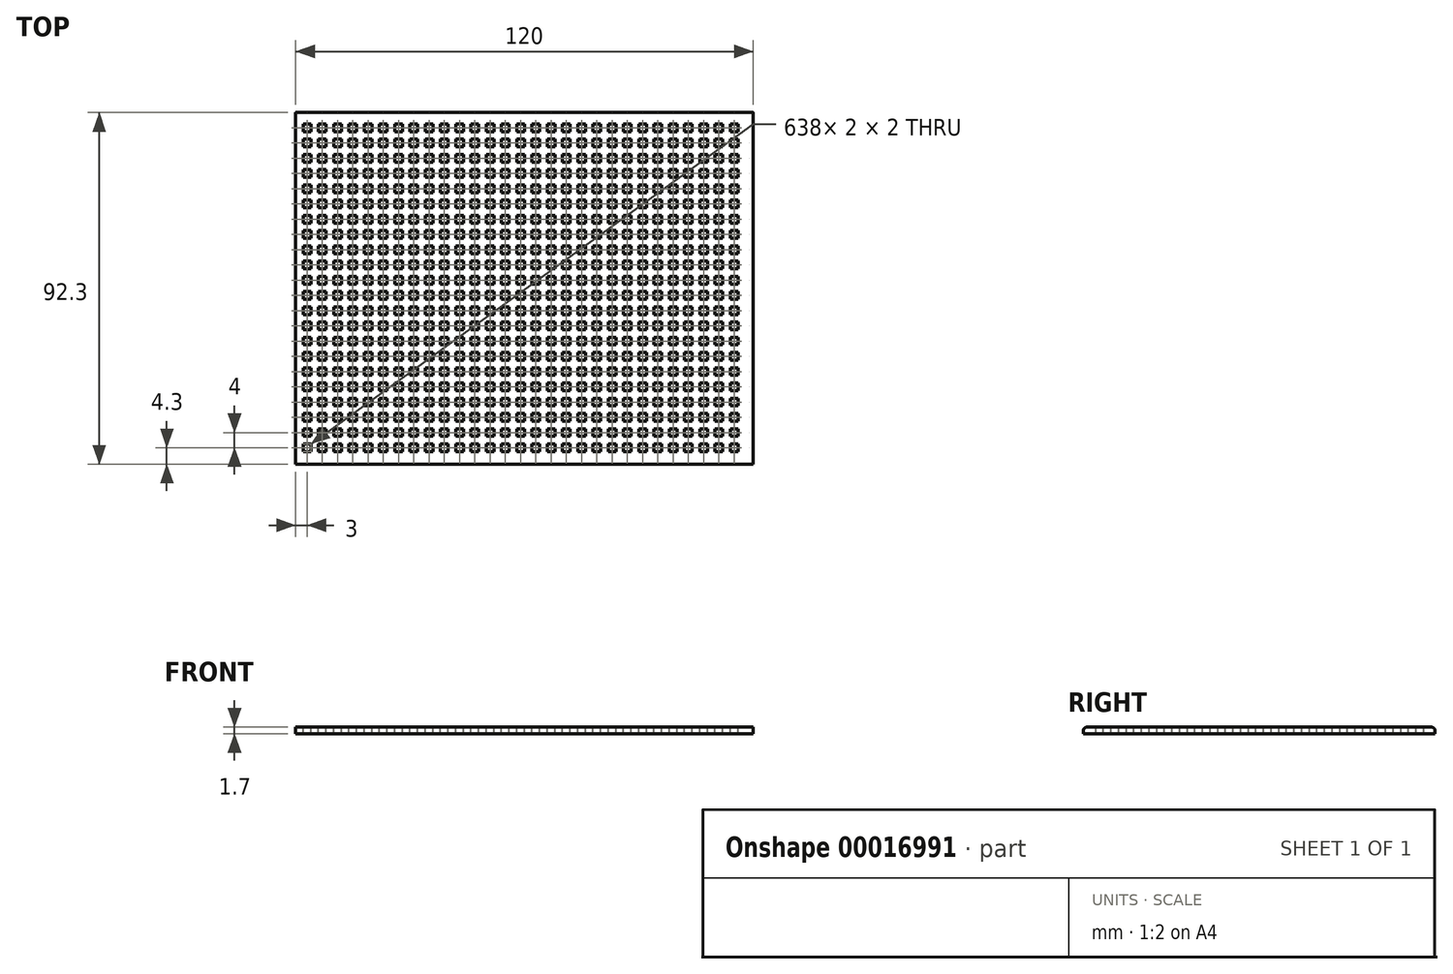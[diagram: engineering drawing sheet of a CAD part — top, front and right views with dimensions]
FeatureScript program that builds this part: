
annotation { "Feature Type Name" : "Feature", "Feature Type Description" : "" }
export const myFeature = defineFeature(function(context is Context, id is Id, definition is map)
    precondition{}
    {
        {
            var Q0;
            Q0=qCreatedBy(makeId("Right.planeOp"),FACE);
            var sketch = newSketch(context, id + "F0", { "sketchPlane" : qUnion([Q0])});
            skLineSegment(sketch, "E0", {"start": v(0, 0) * mm, "end": v(46.15, 0) * mm});
            skLineSegment(sketch, "E1", {"start": v(0, 0) * mm, "end": v(0, 1.7) * mm});
            skLineSegment(sketch, "E2", {"start": v(46.15, 0) * mm, "end": v(46.15, 1.7) * mm});
            skLineSegment(sketch, "E3", {"start": v(0, 1.7) * mm, "end": v(46.15, 1.7) * mm});
            skLineSegment(sketch, "E4.MirrorCS", {"start": v(-46.15, 0) * mm, "end": v(-46.15, 1.7) * mm});
            skLineSegment(sketch, "E5.MirrorCS", {"start": v(0, 1.7) * mm, "end": v(-46.15, 1.7) * mm});
            skLineSegment(sketch, "E6.MirrorCS", {"start": v(0, 0) * mm, "end": v(-46.15, 0) * mm});
            skSolve(sketch);
        }
        {
            var Q0;
            Q0=makeQuery(id+"F0.imprint","IMPRINT",FACE,{"disambiguationData":[TD([[makeQuery(id+"F0.imprint","IMPRINT",EDGE,{"derivedFrom":sQuery(id+"F0.wireOp",EDGE,"E0")}),1.0]])]});
            var Q1;
            Q1=makeQuery(id+"F0.imprint","IMPRINT",FACE,{"disambiguationData":[TD([[makeQuery(id+"F0.imprint","IMPRINT",EDGE,{"derivedFrom":sQuery(id+"F0.wireOp",EDGE,"E1")}),1.0]])]});
            extrude(context, id + "F1", {"entities" : qUnion([Q0, Q1]), "depth" : 60 * mm, "hasSecondDirection" : true, "secondDirectionOppositeDirection" : true, "secondDirectionDepth" : 60 * mm});
        }
        {
            var Q0;
            Q0=makeQuery(id+"F1.opExtrude","SWEPT_EDGE",EDGE,{"disambiguationData":[OSD([sQuery(id+"F0.wireOp",EDGE,"E2"),sQuery(id+"F0.wireOp",EDGE,"E3")])]});
            var Q1;
            Q1=makeQuery(id+"F1.opExtrude","SWEPT_EDGE",EDGE,{"disambiguationData":[OSD([sQuery(id+"F0.wireOp",EDGE,"E4.MirrorCS"),sQuery(id+"F0.wireOp",EDGE,"E5.MirrorCS")])]});
            fillet(context, id + "F2", {"entities" : qUnion([Q0, Q1]), "radius" : 1 * mm, "tangentPropagation" : true, "allowEdgeOverflow" : false});
        }
        {
            var Q0;
            Q0=makeQuery(id+"F1.opExtrude","SWEPT_FACE",FACE,{"disambiguationData":[OSD([sQuery(id+"F0.wireOp",EDGE,"E3"),sQuery(id+"F0.wireOp",EDGE,"E5.MirrorCS")])]});
            var sketch = newSketch(context, id + "F3", { "sketchPlane" : qUnion([Q0])});
            skLineSegment(sketch, "E7.bottom", {"start": v(-58, 43.15) * mm, "end": v(-56, 43.15) * mm});
            skLineSegment(sketch, "E7.top", {"start": v(-58, 41.15) * mm, "end": v(-56, 41.15) * mm});
            skLineSegment(sketch, "E7.left", {"start": v(-58, 43.15) * mm, "end": v(-58, 41.15) * mm});
            skLineSegment(sketch, "E7.right", {"start": v(-56, 43.15) * mm, "end": v(-56, 41.15) * mm});
            skLineSegment(sketch, "E8.0.1.0", {"start": v(-56, 39.15) * mm, "end": v(-56, 37.15) * mm});
            skLineSegment(sketch, "E8.0.1.1", {"start": v(-58, 39.15) * mm, "end": v(-58, 37.15) * mm});
            skLineSegment(sketch, "E8.0.1.2", {"start": v(-58, 37.15) * mm, "end": v(-56, 37.15) * mm});
            skLineSegment(sketch, "E8.0.1.3", {"start": v(-58, 39.15) * mm, "end": v(-56, 39.15) * mm});
            skLineSegment(sketch, "E8.0.2.0", {"start": v(-56, 35.15) * mm, "end": v(-56, 33.15) * mm});
            skLineSegment(sketch, "E8.0.2.1", {"start": v(-58, 35.15) * mm, "end": v(-58, 33.15) * mm});
            skLineSegment(sketch, "E8.0.2.2", {"start": v(-58, 33.15) * mm, "end": v(-56, 33.15) * mm});
            skLineSegment(sketch, "E8.0.2.3", {"start": v(-58, 35.15) * mm, "end": v(-56, 35.15) * mm});
            skLineSegment(sketch, "E8.0.3.0", {"start": v(-56, 31.15) * mm, "end": v(-56, 29.15) * mm});
            skLineSegment(sketch, "E8.0.3.1", {"start": v(-58, 31.15) * mm, "end": v(-58, 29.15) * mm});
            skLineSegment(sketch, "E8.0.3.2", {"start": v(-58, 29.15) * mm, "end": v(-56, 29.15) * mm});
            skLineSegment(sketch, "E8.0.3.3", {"start": v(-58, 31.15) * mm, "end": v(-56, 31.15) * mm});
            skLineSegment(sketch, "E8.0.4.0", {"start": v(-56, 27.15) * mm, "end": v(-56, 25.15) * mm});
            skLineSegment(sketch, "E8.0.4.1", {"start": v(-58, 27.15) * mm, "end": v(-58, 25.15) * mm});
            skLineSegment(sketch, "E8.0.4.2", {"start": v(-58, 25.15) * mm, "end": v(-56, 25.15) * mm});
            skLineSegment(sketch, "E8.0.4.3", {"start": v(-58, 27.15) * mm, "end": v(-56, 27.15) * mm});
            skLineSegment(sketch, "E8.0.5.0", {"start": v(-56, 23.15) * mm, "end": v(-56, 21.15) * mm});
            skLineSegment(sketch, "E8.0.5.1", {"start": v(-58, 23.15) * mm, "end": v(-58, 21.15) * mm});
            skLineSegment(sketch, "E8.0.5.2", {"start": v(-58, 21.15) * mm, "end": v(-56, 21.15) * mm});
            skLineSegment(sketch, "E8.0.5.3", {"start": v(-58, 23.15) * mm, "end": v(-56, 23.15) * mm});
            skLineSegment(sketch, "E8.0.6.0", {"start": v(-56, 19.15) * mm, "end": v(-56, 17.15) * mm});
            skLineSegment(sketch, "E8.0.6.1", {"start": v(-58, 19.15) * mm, "end": v(-58, 17.15) * mm});
            skLineSegment(sketch, "E8.0.6.2", {"start": v(-58, 17.15) * mm, "end": v(-56, 17.15) * mm});
            skLineSegment(sketch, "E8.0.6.3", {"start": v(-58, 19.15) * mm, "end": v(-56, 19.15) * mm});
            skLineSegment(sketch, "E8.0.7.0", {"start": v(-56, 15.15) * mm, "end": v(-56, 13.15) * mm});
            skLineSegment(sketch, "E8.0.7.1", {"start": v(-58, 15.15) * mm, "end": v(-58, 13.15) * mm});
            skLineSegment(sketch, "E8.0.7.2", {"start": v(-58, 13.15) * mm, "end": v(-56, 13.15) * mm});
            skLineSegment(sketch, "E8.0.7.3", {"start": v(-58, 15.15) * mm, "end": v(-56, 15.15) * mm});
            skLineSegment(sketch, "E8.0.8.0", {"start": v(-56, 11.15) * mm, "end": v(-56, 9.15) * mm});
            skLineSegment(sketch, "E8.0.8.1", {"start": v(-58, 11.15) * mm, "end": v(-58, 9.15) * mm});
            skLineSegment(sketch, "E8.0.8.2", {"start": v(-58, 9.15) * mm, "end": v(-56, 9.15) * mm});
            skLineSegment(sketch, "E8.0.8.3", {"start": v(-58, 11.15) * mm, "end": v(-56, 11.15) * mm});
            skLineSegment(sketch, "E8.0.9.0", {"start": v(-56, 7.15) * mm, "end": v(-56, 5.15) * mm});
            skLineSegment(sketch, "E8.0.9.1", {"start": v(-58, 7.15) * mm, "end": v(-58, 5.15) * mm});
            skLineSegment(sketch, "E8.0.9.2", {"start": v(-58, 5.15) * mm, "end": v(-56, 5.15) * mm});
            skLineSegment(sketch, "E8.0.9.3", {"start": v(-58, 7.15) * mm, "end": v(-56, 7.15) * mm});
            skLineSegment(sketch, "E8.0.10.0", {"start": v(-56, 3.15) * mm, "end": v(-56, 1.15) * mm});
            skLineSegment(sketch, "E8.0.10.1", {"start": v(-58, 3.15) * mm, "end": v(-58, 1.15) * mm});
            skLineSegment(sketch, "E8.0.10.2", {"start": v(-58, 1.15) * mm, "end": v(-56, 1.15) * mm});
            skLineSegment(sketch, "E8.0.10.3", {"start": v(-58, 3.15) * mm, "end": v(-56, 3.15) * mm});
            skLineSegment(sketch, "E8.0.11.0", {"start": v(-56, -0.85) * mm, "end": v(-56, -2.85) * mm});
            skLineSegment(sketch, "E8.0.11.1", {"start": v(-58, -0.85) * mm, "end": v(-58, -2.85) * mm});
            skLineSegment(sketch, "E8.0.11.2", {"start": v(-58, -2.85) * mm, "end": v(-56, -2.85) * mm});
            skLineSegment(sketch, "E8.0.11.3", {"start": v(-58, -0.85) * mm, "end": v(-56, -0.85) * mm});
            skLineSegment(sketch, "E8.0.12.0", {"start": v(-56, -4.85) * mm, "end": v(-56, -6.85) * mm});
            skLineSegment(sketch, "E8.0.12.1", {"start": v(-58, -4.85) * mm, "end": v(-58, -6.85) * mm});
            skLineSegment(sketch, "E8.0.12.2", {"start": v(-58, -6.85) * mm, "end": v(-56, -6.85) * mm});
            skLineSegment(sketch, "E8.0.12.3", {"start": v(-58, -4.85) * mm, "end": v(-56, -4.85) * mm});
            skLineSegment(sketch, "E8.0.13.0", {"start": v(-56, -8.85) * mm, "end": v(-56, -10.85) * mm});
            skLineSegment(sketch, "E8.0.13.1", {"start": v(-58, -8.85) * mm, "end": v(-58, -10.85) * mm});
            skLineSegment(sketch, "E8.0.13.2", {"start": v(-58, -10.85) * mm, "end": v(-56, -10.85) * mm});
            skLineSegment(sketch, "E8.0.13.3", {"start": v(-58, -8.85) * mm, "end": v(-56, -8.85) * mm});
            skLineSegment(sketch, "E8.0.14.0", {"start": v(-56, -12.85) * mm, "end": v(-56, -14.85) * mm});
            skLineSegment(sketch, "E8.0.14.1", {"start": v(-58, -12.85) * mm, "end": v(-58, -14.85) * mm});
            skLineSegment(sketch, "E8.0.14.2", {"start": v(-58, -14.85) * mm, "end": v(-56, -14.85) * mm});
            skLineSegment(sketch, "E8.0.14.3", {"start": v(-58, -12.85) * mm, "end": v(-56, -12.85) * mm});
            skLineSegment(sketch, "E8.0.15.0", {"start": v(-56, -16.85) * mm, "end": v(-56, -18.85) * mm});
            skLineSegment(sketch, "E8.0.15.1", {"start": v(-58, -16.85) * mm, "end": v(-58, -18.85) * mm});
            skLineSegment(sketch, "E8.0.15.2", {"start": v(-58, -18.85) * mm, "end": v(-56, -18.85) * mm});
            skLineSegment(sketch, "E8.0.15.3", {"start": v(-58, -16.85) * mm, "end": v(-56, -16.85) * mm});
            skLineSegment(sketch, "E8.0.16.0", {"start": v(-56, -20.85) * mm, "end": v(-56, -22.85) * mm});
            skLineSegment(sketch, "E8.0.16.1", {"start": v(-58, -20.85) * mm, "end": v(-58, -22.85) * mm});
            skLineSegment(sketch, "E8.0.16.2", {"start": v(-58, -22.85) * mm, "end": v(-56, -22.85) * mm});
            skLineSegment(sketch, "E8.0.16.3", {"start": v(-58, -20.85) * mm, "end": v(-56, -20.85) * mm});
            skLineSegment(sketch, "E8.0.17.0", {"start": v(-56, -24.85) * mm, "end": v(-56, -26.85) * mm});
            skLineSegment(sketch, "E8.0.17.1", {"start": v(-58, -24.85) * mm, "end": v(-58, -26.85) * mm});
            skLineSegment(sketch, "E8.0.17.2", {"start": v(-58, -26.85) * mm, "end": v(-56, -26.85) * mm});
            skLineSegment(sketch, "E8.0.17.3", {"start": v(-58, -24.85) * mm, "end": v(-56, -24.85) * mm});
            skLineSegment(sketch, "E8.0.18.0", {"start": v(-56, -28.85) * mm, "end": v(-56, -30.85) * mm});
            skLineSegment(sketch, "E8.0.18.1", {"start": v(-58, -28.85) * mm, "end": v(-58, -30.85) * mm});
            skLineSegment(sketch, "E8.0.18.2", {"start": v(-58, -30.85) * mm, "end": v(-56, -30.85) * mm});
            skLineSegment(sketch, "E8.0.18.3", {"start": v(-58, -28.85) * mm, "end": v(-56, -28.85) * mm});
            skLineSegment(sketch, "E8.0.19.0", {"start": v(-56, -32.85) * mm, "end": v(-56, -34.85) * mm});
            skLineSegment(sketch, "E8.0.19.1", {"start": v(-58, -32.85) * mm, "end": v(-58, -34.85) * mm});
            skLineSegment(sketch, "E8.0.19.2", {"start": v(-58, -34.85) * mm, "end": v(-56, -34.85) * mm});
            skLineSegment(sketch, "E8.0.19.3", {"start": v(-58, -32.85) * mm, "end": v(-56, -32.85) * mm});
            skLineSegment(sketch, "E8.0.20.0", {"start": v(-56, -36.85) * mm, "end": v(-56, -38.85) * mm});
            skLineSegment(sketch, "E8.0.20.1", {"start": v(-58, -36.85) * mm, "end": v(-58, -38.85) * mm});
            skLineSegment(sketch, "E8.0.20.2", {"start": v(-58, -38.85) * mm, "end": v(-56, -38.85) * mm});
            skLineSegment(sketch, "E8.0.20.3", {"start": v(-58, -36.85) * mm, "end": v(-56, -36.85) * mm});
            skLineSegment(sketch, "E8.0.21.0", {"start": v(-56, -40.85) * mm, "end": v(-56, -42.85) * mm});
            skLineSegment(sketch, "E8.0.21.1", {"start": v(-58, -40.85) * mm, "end": v(-58, -42.85) * mm});
            skLineSegment(sketch, "E8.0.21.2", {"start": v(-58, -42.85) * mm, "end": v(-56, -42.85) * mm});
            skLineSegment(sketch, "E8.0.21.3", {"start": v(-58, -40.85) * mm, "end": v(-56, -40.85) * mm});
            skLineSegment(sketch, "E8.1.0.0", {"start": v(-52, 43.15) * mm, "end": v(-52, 41.15) * mm});
            skLineSegment(sketch, "E8.1.0.1", {"start": v(-54, 43.15) * mm, "end": v(-54, 41.15) * mm});
            skLineSegment(sketch, "E8.1.0.2", {"start": v(-54, 41.15) * mm, "end": v(-52, 41.15) * mm});
            skLineSegment(sketch, "E8.1.0.3", {"start": v(-54, 43.15) * mm, "end": v(-52, 43.15) * mm});
            skLineSegment(sketch, "E8.1.1.0", {"start": v(-52, 39.15) * mm, "end": v(-52, 37.15) * mm});
            skLineSegment(sketch, "E8.1.1.1", {"start": v(-54, 39.15) * mm, "end": v(-54, 37.15) * mm});
            skLineSegment(sketch, "E8.1.1.2", {"start": v(-54, 37.15) * mm, "end": v(-52, 37.15) * mm});
            skLineSegment(sketch, "E8.1.1.3", {"start": v(-54, 39.15) * mm, "end": v(-52, 39.15) * mm});
            skLineSegment(sketch, "E8.1.2.0", {"start": v(-52, 35.15) * mm, "end": v(-52, 33.15) * mm});
            skLineSegment(sketch, "E8.1.2.1", {"start": v(-54, 35.15) * mm, "end": v(-54, 33.15) * mm});
            skLineSegment(sketch, "E8.1.2.2", {"start": v(-54, 33.15) * mm, "end": v(-52, 33.15) * mm});
            skLineSegment(sketch, "E8.1.2.3", {"start": v(-54, 35.15) * mm, "end": v(-52, 35.15) * mm});
            skLineSegment(sketch, "E8.1.3.0", {"start": v(-52, 31.15) * mm, "end": v(-52, 29.15) * mm});
            skLineSegment(sketch, "E8.1.3.1", {"start": v(-54, 31.15) * mm, "end": v(-54, 29.15) * mm});
            skLineSegment(sketch, "E8.1.3.2", {"start": v(-54, 29.15) * mm, "end": v(-52, 29.15) * mm});
            skLineSegment(sketch, "E8.1.3.3", {"start": v(-54, 31.15) * mm, "end": v(-52, 31.15) * mm});
            skLineSegment(sketch, "E8.1.4.0", {"start": v(-52, 27.15) * mm, "end": v(-52, 25.15) * mm});
            skLineSegment(sketch, "E8.1.4.1", {"start": v(-54, 27.15) * mm, "end": v(-54, 25.15) * mm});
            skLineSegment(sketch, "E8.1.4.2", {"start": v(-54, 25.15) * mm, "end": v(-52, 25.15) * mm});
            skLineSegment(sketch, "E8.1.4.3", {"start": v(-54, 27.15) * mm, "end": v(-52, 27.15) * mm});
            skLineSegment(sketch, "E8.1.5.0", {"start": v(-52, 23.15) * mm, "end": v(-52, 21.15) * mm});
            skLineSegment(sketch, "E8.1.5.1", {"start": v(-54, 23.15) * mm, "end": v(-54, 21.15) * mm});
            skLineSegment(sketch, "E8.1.5.2", {"start": v(-54, 21.15) * mm, "end": v(-52, 21.15) * mm});
            skLineSegment(sketch, "E8.1.5.3", {"start": v(-54, 23.15) * mm, "end": v(-52, 23.15) * mm});
            skLineSegment(sketch, "E8.1.6.0", {"start": v(-52, 19.15) * mm, "end": v(-52, 17.15) * mm});
            skLineSegment(sketch, "E8.1.6.1", {"start": v(-54, 19.15) * mm, "end": v(-54, 17.15) * mm});
            skLineSegment(sketch, "E8.1.6.2", {"start": v(-54, 17.15) * mm, "end": v(-52, 17.15) * mm});
            skLineSegment(sketch, "E8.1.6.3", {"start": v(-54, 19.15) * mm, "end": v(-52, 19.15) * mm});
            skLineSegment(sketch, "E8.1.7.0", {"start": v(-52, 15.15) * mm, "end": v(-52, 13.15) * mm});
            skLineSegment(sketch, "E8.1.7.1", {"start": v(-54, 15.15) * mm, "end": v(-54, 13.15) * mm});
            skLineSegment(sketch, "E8.1.7.2", {"start": v(-54, 13.15) * mm, "end": v(-52, 13.15) * mm});
            skLineSegment(sketch, "E8.1.7.3", {"start": v(-54, 15.15) * mm, "end": v(-52, 15.15) * mm});
            skLineSegment(sketch, "E8.1.8.0", {"start": v(-52, 11.15) * mm, "end": v(-52, 9.15) * mm});
            skLineSegment(sketch, "E8.1.8.1", {"start": v(-54, 11.15) * mm, "end": v(-54, 9.15) * mm});
            skLineSegment(sketch, "E8.1.8.2", {"start": v(-54, 9.15) * mm, "end": v(-52, 9.15) * mm});
            skLineSegment(sketch, "E8.1.8.3", {"start": v(-54, 11.15) * mm, "end": v(-52, 11.15) * mm});
            skLineSegment(sketch, "E8.1.9.0", {"start": v(-52, 7.15) * mm, "end": v(-52, 5.15) * mm});
            skLineSegment(sketch, "E8.1.9.1", {"start": v(-54, 7.15) * mm, "end": v(-54, 5.15) * mm});
            skLineSegment(sketch, "E8.1.9.2", {"start": v(-54, 5.15) * mm, "end": v(-52, 5.15) * mm});
            skLineSegment(sketch, "E8.1.9.3", {"start": v(-54, 7.15) * mm, "end": v(-52, 7.15) * mm});
            skLineSegment(sketch, "E8.1.10.0", {"start": v(-52, 3.15) * mm, "end": v(-52, 1.15) * mm});
            skLineSegment(sketch, "E8.1.10.1", {"start": v(-54, 3.15) * mm, "end": v(-54, 1.15) * mm});
            skLineSegment(sketch, "E8.1.10.2", {"start": v(-54, 1.15) * mm, "end": v(-52, 1.15) * mm});
            skLineSegment(sketch, "E8.1.10.3", {"start": v(-54, 3.15) * mm, "end": v(-52, 3.15) * mm});
            skLineSegment(sketch, "E8.1.11.0", {"start": v(-52, -0.85) * mm, "end": v(-52, -2.85) * mm});
            skLineSegment(sketch, "E8.1.11.1", {"start": v(-54, -0.85) * mm, "end": v(-54, -2.85) * mm});
            skLineSegment(sketch, "E8.1.11.2", {"start": v(-54, -2.85) * mm, "end": v(-52, -2.85) * mm});
            skLineSegment(sketch, "E8.1.11.3", {"start": v(-54, -0.85) * mm, "end": v(-52, -0.85) * mm});
            skLineSegment(sketch, "E8.1.12.0", {"start": v(-52, -4.85) * mm, "end": v(-52, -6.85) * mm});
            skLineSegment(sketch, "E8.1.12.1", {"start": v(-54, -4.85) * mm, "end": v(-54, -6.85) * mm});
            skLineSegment(sketch, "E8.1.12.2", {"start": v(-54, -6.85) * mm, "end": v(-52, -6.85) * mm});
            skLineSegment(sketch, "E8.1.12.3", {"start": v(-54, -4.85) * mm, "end": v(-52, -4.85) * mm});
            skLineSegment(sketch, "E8.1.13.0", {"start": v(-52, -8.85) * mm, "end": v(-52, -10.85) * mm});
            skLineSegment(sketch, "E8.1.13.1", {"start": v(-54, -8.85) * mm, "end": v(-54, -10.85) * mm});
            skLineSegment(sketch, "E8.1.13.2", {"start": v(-54, -10.85) * mm, "end": v(-52, -10.85) * mm});
            skLineSegment(sketch, "E8.1.13.3", {"start": v(-54, -8.85) * mm, "end": v(-52, -8.85) * mm});
            skLineSegment(sketch, "E8.1.14.0", {"start": v(-52, -12.85) * mm, "end": v(-52, -14.85) * mm});
            skLineSegment(sketch, "E8.1.14.1", {"start": v(-54, -12.85) * mm, "end": v(-54, -14.85) * mm});
            skLineSegment(sketch, "E8.1.14.2", {"start": v(-54, -14.85) * mm, "end": v(-52, -14.85) * mm});
            skLineSegment(sketch, "E8.1.14.3", {"start": v(-54, -12.85) * mm, "end": v(-52, -12.85) * mm});
            skLineSegment(sketch, "E8.1.15.0", {"start": v(-52, -16.85) * mm, "end": v(-52, -18.85) * mm});
            skLineSegment(sketch, "E8.1.15.1", {"start": v(-54, -16.85) * mm, "end": v(-54, -18.85) * mm});
            skLineSegment(sketch, "E8.1.15.2", {"start": v(-54, -18.85) * mm, "end": v(-52, -18.85) * mm});
            skLineSegment(sketch, "E8.1.15.3", {"start": v(-54, -16.85) * mm, "end": v(-52, -16.85) * mm});
            skLineSegment(sketch, "E8.1.16.0", {"start": v(-52, -20.85) * mm, "end": v(-52, -22.85) * mm});
            skLineSegment(sketch, "E8.1.16.1", {"start": v(-54, -20.85) * mm, "end": v(-54, -22.85) * mm});
            skLineSegment(sketch, "E8.1.16.2", {"start": v(-54, -22.85) * mm, "end": v(-52, -22.85) * mm});
            skLineSegment(sketch, "E8.1.16.3", {"start": v(-54, -20.85) * mm, "end": v(-52, -20.85) * mm});
            skLineSegment(sketch, "E8.1.17.0", {"start": v(-52, -24.85) * mm, "end": v(-52, -26.85) * mm});
            skLineSegment(sketch, "E8.1.17.1", {"start": v(-54, -24.85) * mm, "end": v(-54, -26.85) * mm});
            skLineSegment(sketch, "E8.1.17.2", {"start": v(-54, -26.85) * mm, "end": v(-52, -26.85) * mm});
            skLineSegment(sketch, "E8.1.17.3", {"start": v(-54, -24.85) * mm, "end": v(-52, -24.85) * mm});
            skLineSegment(sketch, "E8.1.18.0", {"start": v(-52, -28.85) * mm, "end": v(-52, -30.85) * mm});
            skLineSegment(sketch, "E8.1.18.1", {"start": v(-54, -28.85) * mm, "end": v(-54, -30.85) * mm});
            skLineSegment(sketch, "E8.1.18.2", {"start": v(-54, -30.85) * mm, "end": v(-52, -30.85) * mm});
            skLineSegment(sketch, "E8.1.18.3", {"start": v(-54, -28.85) * mm, "end": v(-52, -28.85) * mm});
            skLineSegment(sketch, "E8.1.19.0", {"start": v(-52, -32.85) * mm, "end": v(-52, -34.85) * mm});
            skLineSegment(sketch, "E8.1.19.1", {"start": v(-54, -32.85) * mm, "end": v(-54, -34.85) * mm});
            skLineSegment(sketch, "E8.1.19.2", {"start": v(-54, -34.85) * mm, "end": v(-52, -34.85) * mm});
            skLineSegment(sketch, "E8.1.19.3", {"start": v(-54, -32.85) * mm, "end": v(-52, -32.85) * mm});
            skLineSegment(sketch, "E8.1.20.0", {"start": v(-52, -36.85) * mm, "end": v(-52, -38.85) * mm});
            skLineSegment(sketch, "E8.1.20.1", {"start": v(-54, -36.85) * mm, "end": v(-54, -38.85) * mm});
            skLineSegment(sketch, "E8.1.20.2", {"start": v(-54, -38.85) * mm, "end": v(-52, -38.85) * mm});
            skLineSegment(sketch, "E8.1.20.3", {"start": v(-54, -36.85) * mm, "end": v(-52, -36.85) * mm});
            skLineSegment(sketch, "E8.1.21.0", {"start": v(-52, -40.85) * mm, "end": v(-52, -42.85) * mm});
            skLineSegment(sketch, "E8.1.21.1", {"start": v(-54, -40.85) * mm, "end": v(-54, -42.85) * mm});
            skLineSegment(sketch, "E8.1.21.2", {"start": v(-54, -42.85) * mm, "end": v(-52, -42.85) * mm});
            skLineSegment(sketch, "E8.1.21.3", {"start": v(-54, -40.85) * mm, "end": v(-52, -40.85) * mm});
            skLineSegment(sketch, "E8.2.0.0", {"start": v(-48, 43.15) * mm, "end": v(-48, 41.15) * mm});
            skLineSegment(sketch, "E8.2.0.1", {"start": v(-50, 43.15) * mm, "end": v(-50, 41.15) * mm});
            skLineSegment(sketch, "E8.2.0.2", {"start": v(-50, 41.15) * mm, "end": v(-48, 41.15) * mm});
            skLineSegment(sketch, "E8.2.0.3", {"start": v(-50, 43.15) * mm, "end": v(-48, 43.15) * mm});
            skLineSegment(sketch, "E8.2.1.0", {"start": v(-48, 39.15) * mm, "end": v(-48, 37.15) * mm});
            skLineSegment(sketch, "E8.2.1.1", {"start": v(-50, 39.15) * mm, "end": v(-50, 37.15) * mm});
            skLineSegment(sketch, "E8.2.1.2", {"start": v(-50, 37.15) * mm, "end": v(-48, 37.15) * mm});
            skLineSegment(sketch, "E8.2.1.3", {"start": v(-50, 39.15) * mm, "end": v(-48, 39.15) * mm});
            skLineSegment(sketch, "E8.2.2.0", {"start": v(-48, 35.15) * mm, "end": v(-48, 33.15) * mm});
            skLineSegment(sketch, "E8.2.2.1", {"start": v(-50, 35.15) * mm, "end": v(-50, 33.15) * mm});
            skLineSegment(sketch, "E8.2.2.2", {"start": v(-50, 33.15) * mm, "end": v(-48, 33.15) * mm});
            skLineSegment(sketch, "E8.2.2.3", {"start": v(-50, 35.15) * mm, "end": v(-48, 35.15) * mm});
            skLineSegment(sketch, "E8.2.3.0", {"start": v(-48, 31.15) * mm, "end": v(-48, 29.15) * mm});
            skLineSegment(sketch, "E8.2.3.1", {"start": v(-50, 31.15) * mm, "end": v(-50, 29.15) * mm});
            skLineSegment(sketch, "E8.2.3.2", {"start": v(-50, 29.15) * mm, "end": v(-48, 29.15) * mm});
            skLineSegment(sketch, "E8.2.3.3", {"start": v(-50, 31.15) * mm, "end": v(-48, 31.15) * mm});
            skLineSegment(sketch, "E8.2.4.0", {"start": v(-48, 27.15) * mm, "end": v(-48, 25.15) * mm});
            skLineSegment(sketch, "E8.2.4.1", {"start": v(-50, 27.15) * mm, "end": v(-50, 25.15) * mm});
            skLineSegment(sketch, "E8.2.4.2", {"start": v(-50, 25.15) * mm, "end": v(-48, 25.15) * mm});
            skLineSegment(sketch, "E8.2.4.3", {"start": v(-50, 27.15) * mm, "end": v(-48, 27.15) * mm});
            skLineSegment(sketch, "E8.2.5.0", {"start": v(-48, 23.15) * mm, "end": v(-48, 21.15) * mm});
            skLineSegment(sketch, "E8.2.5.1", {"start": v(-50, 23.15) * mm, "end": v(-50, 21.15) * mm});
            skLineSegment(sketch, "E8.2.5.2", {"start": v(-50, 21.15) * mm, "end": v(-48, 21.15) * mm});
            skLineSegment(sketch, "E8.2.5.3", {"start": v(-50, 23.15) * mm, "end": v(-48, 23.15) * mm});
            skLineSegment(sketch, "E8.2.6.0", {"start": v(-48, 19.15) * mm, "end": v(-48, 17.15) * mm});
            skLineSegment(sketch, "E8.2.6.1", {"start": v(-50, 19.15) * mm, "end": v(-50, 17.15) * mm});
            skLineSegment(sketch, "E8.2.6.2", {"start": v(-50, 17.15) * mm, "end": v(-48, 17.15) * mm});
            skLineSegment(sketch, "E8.2.6.3", {"start": v(-50, 19.15) * mm, "end": v(-48, 19.15) * mm});
            skLineSegment(sketch, "E8.2.7.0", {"start": v(-48, 15.15) * mm, "end": v(-48, 13.15) * mm});
            skLineSegment(sketch, "E8.2.7.1", {"start": v(-50, 15.15) * mm, "end": v(-50, 13.15) * mm});
            skLineSegment(sketch, "E8.2.7.2", {"start": v(-50, 13.15) * mm, "end": v(-48, 13.15) * mm});
            skLineSegment(sketch, "E8.2.7.3", {"start": v(-50, 15.15) * mm, "end": v(-48, 15.15) * mm});
            skLineSegment(sketch, "E8.2.8.0", {"start": v(-48, 11.15) * mm, "end": v(-48, 9.15) * mm});
            skLineSegment(sketch, "E8.2.8.1", {"start": v(-50, 11.15) * mm, "end": v(-50, 9.15) * mm});
            skLineSegment(sketch, "E8.2.8.2", {"start": v(-50, 9.15) * mm, "end": v(-48, 9.15) * mm});
            skLineSegment(sketch, "E8.2.8.3", {"start": v(-50, 11.15) * mm, "end": v(-48, 11.15) * mm});
            skLineSegment(sketch, "E8.2.9.0", {"start": v(-48, 7.15) * mm, "end": v(-48, 5.15) * mm});
            skLineSegment(sketch, "E8.2.9.1", {"start": v(-50, 7.15) * mm, "end": v(-50, 5.15) * mm});
            skLineSegment(sketch, "E8.2.9.2", {"start": v(-50, 5.15) * mm, "end": v(-48, 5.15) * mm});
            skLineSegment(sketch, "E8.2.9.3", {"start": v(-50, 7.15) * mm, "end": v(-48, 7.15) * mm});
            skLineSegment(sketch, "E8.2.10.0", {"start": v(-48, 3.15) * mm, "end": v(-48, 1.15) * mm});
            skLineSegment(sketch, "E8.2.10.1", {"start": v(-50, 3.15) * mm, "end": v(-50, 1.15) * mm});
            skLineSegment(sketch, "E8.2.10.2", {"start": v(-50, 1.15) * mm, "end": v(-48, 1.15) * mm});
            skLineSegment(sketch, "E8.2.10.3", {"start": v(-50, 3.15) * mm, "end": v(-48, 3.15) * mm});
            skLineSegment(sketch, "E8.2.11.0", {"start": v(-48, -0.85) * mm, "end": v(-48, -2.85) * mm});
            skLineSegment(sketch, "E8.2.11.1", {"start": v(-50, -0.85) * mm, "end": v(-50, -2.85) * mm});
            skLineSegment(sketch, "E8.2.11.2", {"start": v(-50, -2.85) * mm, "end": v(-48, -2.85) * mm});
            skLineSegment(sketch, "E8.2.11.3", {"start": v(-50, -0.85) * mm, "end": v(-48, -0.85) * mm});
            skLineSegment(sketch, "E8.2.12.0", {"start": v(-48, -4.85) * mm, "end": v(-48, -6.85) * mm});
            skLineSegment(sketch, "E8.2.12.1", {"start": v(-50, -4.85) * mm, "end": v(-50, -6.85) * mm});
            skLineSegment(sketch, "E8.2.12.2", {"start": v(-50, -6.85) * mm, "end": v(-48, -6.85) * mm});
            skLineSegment(sketch, "E8.2.12.3", {"start": v(-50, -4.85) * mm, "end": v(-48, -4.85) * mm});
            skLineSegment(sketch, "E8.2.13.0", {"start": v(-48, -8.85) * mm, "end": v(-48, -10.85) * mm});
            skLineSegment(sketch, "E8.2.13.1", {"start": v(-50, -8.85) * mm, "end": v(-50, -10.85) * mm});
            skLineSegment(sketch, "E8.2.13.2", {"start": v(-50, -10.85) * mm, "end": v(-48, -10.85) * mm});
            skLineSegment(sketch, "E8.2.13.3", {"start": v(-50, -8.85) * mm, "end": v(-48, -8.85) * mm});
            skLineSegment(sketch, "E8.2.14.0", {"start": v(-48, -12.85) * mm, "end": v(-48, -14.85) * mm});
            skLineSegment(sketch, "E8.2.14.1", {"start": v(-50, -12.85) * mm, "end": v(-50, -14.85) * mm});
            skLineSegment(sketch, "E8.2.14.2", {"start": v(-50, -14.85) * mm, "end": v(-48, -14.85) * mm});
            skLineSegment(sketch, "E8.2.14.3", {"start": v(-50, -12.85) * mm, "end": v(-48, -12.85) * mm});
            skLineSegment(sketch, "E8.2.15.0", {"start": v(-48, -16.85) * mm, "end": v(-48, -18.85) * mm});
            skLineSegment(sketch, "E8.2.15.1", {"start": v(-50, -16.85) * mm, "end": v(-50, -18.85) * mm});
            skLineSegment(sketch, "E8.2.15.2", {"start": v(-50, -18.85) * mm, "end": v(-48, -18.85) * mm});
            skLineSegment(sketch, "E8.2.15.3", {"start": v(-50, -16.85) * mm, "end": v(-48, -16.85) * mm});
            skLineSegment(sketch, "E8.2.16.0", {"start": v(-48, -20.85) * mm, "end": v(-48, -22.85) * mm});
            skLineSegment(sketch, "E8.2.16.1", {"start": v(-50, -20.85) * mm, "end": v(-50, -22.85) * mm});
            skLineSegment(sketch, "E8.2.16.2", {"start": v(-50, -22.85) * mm, "end": v(-48, -22.85) * mm});
            skLineSegment(sketch, "E8.2.16.3", {"start": v(-50, -20.85) * mm, "end": v(-48, -20.85) * mm});
            skLineSegment(sketch, "E8.2.17.0", {"start": v(-48, -24.85) * mm, "end": v(-48, -26.85) * mm});
            skLineSegment(sketch, "E8.2.17.1", {"start": v(-50, -24.85) * mm, "end": v(-50, -26.85) * mm});
            skLineSegment(sketch, "E8.2.17.2", {"start": v(-50, -26.85) * mm, "end": v(-48, -26.85) * mm});
            skLineSegment(sketch, "E8.2.17.3", {"start": v(-50, -24.85) * mm, "end": v(-48, -24.85) * mm});
            skLineSegment(sketch, "E8.2.18.0", {"start": v(-48, -28.85) * mm, "end": v(-48, -30.85) * mm});
            skLineSegment(sketch, "E8.2.18.1", {"start": v(-50, -28.85) * mm, "end": v(-50, -30.85) * mm});
            skLineSegment(sketch, "E8.2.18.2", {"start": v(-50, -30.85) * mm, "end": v(-48, -30.85) * mm});
            skLineSegment(sketch, "E8.2.18.3", {"start": v(-50, -28.85) * mm, "end": v(-48, -28.85) * mm});
            skLineSegment(sketch, "E8.2.19.0", {"start": v(-48, -32.85) * mm, "end": v(-48, -34.85) * mm});
            skLineSegment(sketch, "E8.2.19.1", {"start": v(-50, -32.85) * mm, "end": v(-50, -34.85) * mm});
            skLineSegment(sketch, "E8.2.19.2", {"start": v(-50, -34.85) * mm, "end": v(-48, -34.85) * mm});
            skLineSegment(sketch, "E8.2.19.3", {"start": v(-50, -32.85) * mm, "end": v(-48, -32.85) * mm});
            skLineSegment(sketch, "E8.2.20.0", {"start": v(-48, -36.85) * mm, "end": v(-48, -38.85) * mm});
            skLineSegment(sketch, "E8.2.20.1", {"start": v(-50, -36.85) * mm, "end": v(-50, -38.85) * mm});
            skLineSegment(sketch, "E8.2.20.2", {"start": v(-50, -38.85) * mm, "end": v(-48, -38.85) * mm});
            skLineSegment(sketch, "E8.2.20.3", {"start": v(-50, -36.85) * mm, "end": v(-48, -36.85) * mm});
            skLineSegment(sketch, "E8.2.21.0", {"start": v(-48, -40.85) * mm, "end": v(-48, -42.85) * mm});
            skLineSegment(sketch, "E8.2.21.1", {"start": v(-50, -40.85) * mm, "end": v(-50, -42.85) * mm});
            skLineSegment(sketch, "E8.2.21.2", {"start": v(-50, -42.85) * mm, "end": v(-48, -42.85) * mm});
            skLineSegment(sketch, "E8.2.21.3", {"start": v(-50, -40.85) * mm, "end": v(-48, -40.85) * mm});
            skLineSegment(sketch, "E8.3.0.0", {"start": v(-44, 43.15) * mm, "end": v(-44, 41.15) * mm});
            skLineSegment(sketch, "E8.3.0.1", {"start": v(-46, 43.15) * mm, "end": v(-46, 41.15) * mm});
            skLineSegment(sketch, "E8.3.0.2", {"start": v(-46, 41.15) * mm, "end": v(-44, 41.15) * mm});
            skLineSegment(sketch, "E8.3.0.3", {"start": v(-46, 43.15) * mm, "end": v(-44, 43.15) * mm});
            skLineSegment(sketch, "E8.3.1.0", {"start": v(-44, 39.15) * mm, "end": v(-44, 37.15) * mm});
            skLineSegment(sketch, "E8.3.1.1", {"start": v(-46, 39.15) * mm, "end": v(-46, 37.15) * mm});
            skLineSegment(sketch, "E8.3.1.2", {"start": v(-46, 37.15) * mm, "end": v(-44, 37.15) * mm});
            skLineSegment(sketch, "E8.3.1.3", {"start": v(-46, 39.15) * mm, "end": v(-44, 39.15) * mm});
            skLineSegment(sketch, "E8.3.2.0", {"start": v(-44, 35.15) * mm, "end": v(-44, 33.15) * mm});
            skLineSegment(sketch, "E8.3.2.1", {"start": v(-46, 35.15) * mm, "end": v(-46, 33.15) * mm});
            skLineSegment(sketch, "E8.3.2.2", {"start": v(-46, 33.15) * mm, "end": v(-44, 33.15) * mm});
            skLineSegment(sketch, "E8.3.2.3", {"start": v(-46, 35.15) * mm, "end": v(-44, 35.15) * mm});
            skLineSegment(sketch, "E8.3.3.0", {"start": v(-44, 31.15) * mm, "end": v(-44, 29.15) * mm});
            skLineSegment(sketch, "E8.3.3.1", {"start": v(-46, 31.15) * mm, "end": v(-46, 29.15) * mm});
            skLineSegment(sketch, "E8.3.3.2", {"start": v(-46, 29.15) * mm, "end": v(-44, 29.15) * mm});
            skLineSegment(sketch, "E8.3.3.3", {"start": v(-46, 31.15) * mm, "end": v(-44, 31.15) * mm});
            skLineSegment(sketch, "E8.3.4.0", {"start": v(-44, 27.15) * mm, "end": v(-44, 25.15) * mm});
            skLineSegment(sketch, "E8.3.4.1", {"start": v(-46, 27.15) * mm, "end": v(-46, 25.15) * mm});
            skLineSegment(sketch, "E8.3.4.2", {"start": v(-46, 25.15) * mm, "end": v(-44, 25.15) * mm});
            skLineSegment(sketch, "E8.3.4.3", {"start": v(-46, 27.15) * mm, "end": v(-44, 27.15) * mm});
            skLineSegment(sketch, "E8.3.5.0", {"start": v(-44, 23.15) * mm, "end": v(-44, 21.15) * mm});
            skLineSegment(sketch, "E8.3.5.1", {"start": v(-46, 23.15) * mm, "end": v(-46, 21.15) * mm});
            skLineSegment(sketch, "E8.3.5.2", {"start": v(-46, 21.15) * mm, "end": v(-44, 21.15) * mm});
            skLineSegment(sketch, "E8.3.5.3", {"start": v(-46, 23.15) * mm, "end": v(-44, 23.15) * mm});
            skLineSegment(sketch, "E8.3.6.0", {"start": v(-44, 19.15) * mm, "end": v(-44, 17.15) * mm});
            skLineSegment(sketch, "E8.3.6.1", {"start": v(-46, 19.15) * mm, "end": v(-46, 17.15) * mm});
            skLineSegment(sketch, "E8.3.6.2", {"start": v(-46, 17.15) * mm, "end": v(-44, 17.15) * mm});
            skLineSegment(sketch, "E8.3.6.3", {"start": v(-46, 19.15) * mm, "end": v(-44, 19.15) * mm});
            skLineSegment(sketch, "E8.3.7.0", {"start": v(-44, 15.15) * mm, "end": v(-44, 13.15) * mm});
            skLineSegment(sketch, "E8.3.7.1", {"start": v(-46, 15.15) * mm, "end": v(-46, 13.15) * mm});
            skLineSegment(sketch, "E8.3.7.2", {"start": v(-46, 13.15) * mm, "end": v(-44, 13.15) * mm});
            skLineSegment(sketch, "E8.3.7.3", {"start": v(-46, 15.15) * mm, "end": v(-44, 15.15) * mm});
            skLineSegment(sketch, "E8.3.8.0", {"start": v(-44, 11.15) * mm, "end": v(-44, 9.15) * mm});
            skLineSegment(sketch, "E8.3.8.1", {"start": v(-46, 11.15) * mm, "end": v(-46, 9.15) * mm});
            skLineSegment(sketch, "E8.3.8.2", {"start": v(-46, 9.15) * mm, "end": v(-44, 9.15) * mm});
            skLineSegment(sketch, "E8.3.8.3", {"start": v(-46, 11.15) * mm, "end": v(-44, 11.15) * mm});
            skLineSegment(sketch, "E8.3.9.0", {"start": v(-44, 7.15) * mm, "end": v(-44, 5.15) * mm});
            skLineSegment(sketch, "E8.3.9.1", {"start": v(-46, 7.15) * mm, "end": v(-46, 5.15) * mm});
            skLineSegment(sketch, "E8.3.9.2", {"start": v(-46, 5.15) * mm, "end": v(-44, 5.15) * mm});
            skLineSegment(sketch, "E8.3.9.3", {"start": v(-46, 7.15) * mm, "end": v(-44, 7.15) * mm});
            skLineSegment(sketch, "E8.3.10.0", {"start": v(-44, 3.15) * mm, "end": v(-44, 1.15) * mm});
            skLineSegment(sketch, "E8.3.10.1", {"start": v(-46, 3.15) * mm, "end": v(-46, 1.15) * mm});
            skLineSegment(sketch, "E8.3.10.2", {"start": v(-46, 1.15) * mm, "end": v(-44, 1.15) * mm});
            skLineSegment(sketch, "E8.3.10.3", {"start": v(-46, 3.15) * mm, "end": v(-44, 3.15) * mm});
            skLineSegment(sketch, "E8.3.11.0", {"start": v(-44, -0.85) * mm, "end": v(-44, -2.85) * mm});
            skLineSegment(sketch, "E8.3.11.1", {"start": v(-46, -0.85) * mm, "end": v(-46, -2.85) * mm});
            skLineSegment(sketch, "E8.3.11.2", {"start": v(-46, -2.85) * mm, "end": v(-44, -2.85) * mm});
            skLineSegment(sketch, "E8.3.11.3", {"start": v(-46, -0.85) * mm, "end": v(-44, -0.85) * mm});
            skLineSegment(sketch, "E8.3.12.0", {"start": v(-44, -4.85) * mm, "end": v(-44, -6.85) * mm});
            skLineSegment(sketch, "E8.3.12.1", {"start": v(-46, -4.85) * mm, "end": v(-46, -6.85) * mm});
            skLineSegment(sketch, "E8.3.12.2", {"start": v(-46, -6.85) * mm, "end": v(-44, -6.85) * mm});
            skLineSegment(sketch, "E8.3.12.3", {"start": v(-46, -4.85) * mm, "end": v(-44, -4.85) * mm});
            skLineSegment(sketch, "E8.3.13.0", {"start": v(-44, -8.85) * mm, "end": v(-44, -10.85) * mm});
            skLineSegment(sketch, "E8.3.13.1", {"start": v(-46, -8.85) * mm, "end": v(-46, -10.85) * mm});
            skLineSegment(sketch, "E8.3.13.2", {"start": v(-46, -10.85) * mm, "end": v(-44, -10.85) * mm});
            skLineSegment(sketch, "E8.3.13.3", {"start": v(-46, -8.85) * mm, "end": v(-44, -8.85) * mm});
            skLineSegment(sketch, "E8.3.14.0", {"start": v(-44, -12.85) * mm, "end": v(-44, -14.85) * mm});
            skLineSegment(sketch, "E8.3.14.1", {"start": v(-46, -12.85) * mm, "end": v(-46, -14.85) * mm});
            skLineSegment(sketch, "E8.3.14.2", {"start": v(-46, -14.85) * mm, "end": v(-44, -14.85) * mm});
            skLineSegment(sketch, "E8.3.14.3", {"start": v(-46, -12.85) * mm, "end": v(-44, -12.85) * mm});
            skLineSegment(sketch, "E8.3.15.0", {"start": v(-44, -16.85) * mm, "end": v(-44, -18.85) * mm});
            skLineSegment(sketch, "E8.3.15.1", {"start": v(-46, -16.85) * mm, "end": v(-46, -18.85) * mm});
            skLineSegment(sketch, "E8.3.15.2", {"start": v(-46, -18.85) * mm, "end": v(-44, -18.85) * mm});
            skLineSegment(sketch, "E8.3.15.3", {"start": v(-46, -16.85) * mm, "end": v(-44, -16.85) * mm});
            skLineSegment(sketch, "E8.3.16.0", {"start": v(-44, -20.85) * mm, "end": v(-44, -22.85) * mm});
            skLineSegment(sketch, "E8.3.16.1", {"start": v(-46, -20.85) * mm, "end": v(-46, -22.85) * mm});
            skLineSegment(sketch, "E8.3.16.2", {"start": v(-46, -22.85) * mm, "end": v(-44, -22.85) * mm});
            skLineSegment(sketch, "E8.3.16.3", {"start": v(-46, -20.85) * mm, "end": v(-44, -20.85) * mm});
            skLineSegment(sketch, "E8.3.17.0", {"start": v(-44, -24.85) * mm, "end": v(-44, -26.85) * mm});
            skLineSegment(sketch, "E8.3.17.1", {"start": v(-46, -24.85) * mm, "end": v(-46, -26.85) * mm});
            skLineSegment(sketch, "E8.3.17.2", {"start": v(-46, -26.85) * mm, "end": v(-44, -26.85) * mm});
            skLineSegment(sketch, "E8.3.17.3", {"start": v(-46, -24.85) * mm, "end": v(-44, -24.85) * mm});
            skLineSegment(sketch, "E8.3.18.0", {"start": v(-44, -28.85) * mm, "end": v(-44, -30.85) * mm});
            skLineSegment(sketch, "E8.3.18.1", {"start": v(-46, -28.85) * mm, "end": v(-46, -30.85) * mm});
            skLineSegment(sketch, "E8.3.18.2", {"start": v(-46, -30.85) * mm, "end": v(-44, -30.85) * mm});
            skLineSegment(sketch, "E8.3.18.3", {"start": v(-46, -28.85) * mm, "end": v(-44, -28.85) * mm});
            skLineSegment(sketch, "E8.3.19.0", {"start": v(-44, -32.85) * mm, "end": v(-44, -34.85) * mm});
            skLineSegment(sketch, "E8.3.19.1", {"start": v(-46, -32.85) * mm, "end": v(-46, -34.85) * mm});
            skLineSegment(sketch, "E8.3.19.2", {"start": v(-46, -34.85) * mm, "end": v(-44, -34.85) * mm});
            skLineSegment(sketch, "E8.3.19.3", {"start": v(-46, -32.85) * mm, "end": v(-44, -32.85) * mm});
            skLineSegment(sketch, "E8.3.20.0", {"start": v(-44, -36.85) * mm, "end": v(-44, -38.85) * mm});
            skLineSegment(sketch, "E8.3.20.1", {"start": v(-46, -36.85) * mm, "end": v(-46, -38.85) * mm});
            skLineSegment(sketch, "E8.3.20.2", {"start": v(-46, -38.85) * mm, "end": v(-44, -38.85) * mm});
            skLineSegment(sketch, "E8.3.20.3", {"start": v(-46, -36.85) * mm, "end": v(-44, -36.85) * mm});
            skLineSegment(sketch, "E8.3.21.0", {"start": v(-44, -40.85) * mm, "end": v(-44, -42.85) * mm});
            skLineSegment(sketch, "E8.3.21.1", {"start": v(-46, -40.85) * mm, "end": v(-46, -42.85) * mm});
            skLineSegment(sketch, "E8.3.21.2", {"start": v(-46, -42.85) * mm, "end": v(-44, -42.85) * mm});
            skLineSegment(sketch, "E8.3.21.3", {"start": v(-46, -40.85) * mm, "end": v(-44, -40.85) * mm});
            skLineSegment(sketch, "E8.4.0.0", {"start": v(-40, 43.15) * mm, "end": v(-40, 41.15) * mm});
            skLineSegment(sketch, "E8.4.0.1", {"start": v(-42, 43.15) * mm, "end": v(-42, 41.15) * mm});
            skLineSegment(sketch, "E8.4.0.2", {"start": v(-42, 41.15) * mm, "end": v(-40, 41.15) * mm});
            skLineSegment(sketch, "E8.4.0.3", {"start": v(-42, 43.15) * mm, "end": v(-40, 43.15) * mm});
            skLineSegment(sketch, "E8.4.1.0", {"start": v(-40, 39.15) * mm, "end": v(-40, 37.15) * mm});
            skLineSegment(sketch, "E8.4.1.1", {"start": v(-42, 39.15) * mm, "end": v(-42, 37.15) * mm});
            skLineSegment(sketch, "E8.4.1.2", {"start": v(-42, 37.15) * mm, "end": v(-40, 37.15) * mm});
            skLineSegment(sketch, "E8.4.1.3", {"start": v(-42, 39.15) * mm, "end": v(-40, 39.15) * mm});
            skLineSegment(sketch, "E8.4.2.0", {"start": v(-40, 35.15) * mm, "end": v(-40, 33.15) * mm});
            skLineSegment(sketch, "E8.4.2.1", {"start": v(-42, 35.15) * mm, "end": v(-42, 33.15) * mm});
            skLineSegment(sketch, "E8.4.2.2", {"start": v(-42, 33.15) * mm, "end": v(-40, 33.15) * mm});
            skLineSegment(sketch, "E8.4.2.3", {"start": v(-42, 35.15) * mm, "end": v(-40, 35.15) * mm});
            skLineSegment(sketch, "E8.4.3.0", {"start": v(-40, 31.15) * mm, "end": v(-40, 29.15) * mm});
            skLineSegment(sketch, "E8.4.3.1", {"start": v(-42, 31.15) * mm, "end": v(-42, 29.15) * mm});
            skLineSegment(sketch, "E8.4.3.2", {"start": v(-42, 29.15) * mm, "end": v(-40, 29.15) * mm});
            skLineSegment(sketch, "E8.4.3.3", {"start": v(-42, 31.15) * mm, "end": v(-40, 31.15) * mm});
            skLineSegment(sketch, "E8.4.4.0", {"start": v(-40, 27.15) * mm, "end": v(-40, 25.15) * mm});
            skLineSegment(sketch, "E8.4.4.1", {"start": v(-42, 27.15) * mm, "end": v(-42, 25.15) * mm});
            skLineSegment(sketch, "E8.4.4.2", {"start": v(-42, 25.15) * mm, "end": v(-40, 25.15) * mm});
            skLineSegment(sketch, "E8.4.4.3", {"start": v(-42, 27.15) * mm, "end": v(-40, 27.15) * mm});
            skLineSegment(sketch, "E8.4.5.0", {"start": v(-40, 23.15) * mm, "end": v(-40, 21.15) * mm});
            skLineSegment(sketch, "E8.4.5.1", {"start": v(-42, 23.15) * mm, "end": v(-42, 21.15) * mm});
            skLineSegment(sketch, "E8.4.5.2", {"start": v(-42, 21.15) * mm, "end": v(-40, 21.15) * mm});
            skLineSegment(sketch, "E8.4.5.3", {"start": v(-42, 23.15) * mm, "end": v(-40, 23.15) * mm});
            skLineSegment(sketch, "E8.4.6.0", {"start": v(-40, 19.15) * mm, "end": v(-40, 17.15) * mm});
            skLineSegment(sketch, "E8.4.6.1", {"start": v(-42, 19.15) * mm, "end": v(-42, 17.15) * mm});
            skLineSegment(sketch, "E8.4.6.2", {"start": v(-42, 17.15) * mm, "end": v(-40, 17.15) * mm});
            skLineSegment(sketch, "E8.4.6.3", {"start": v(-42, 19.15) * mm, "end": v(-40, 19.15) * mm});
            skLineSegment(sketch, "E8.4.7.0", {"start": v(-40, 15.15) * mm, "end": v(-40, 13.15) * mm});
            skLineSegment(sketch, "E8.4.7.1", {"start": v(-42, 15.15) * mm, "end": v(-42, 13.15) * mm});
            skLineSegment(sketch, "E8.4.7.2", {"start": v(-42, 13.15) * mm, "end": v(-40, 13.15) * mm});
            skLineSegment(sketch, "E8.4.7.3", {"start": v(-42, 15.15) * mm, "end": v(-40, 15.15) * mm});
            skLineSegment(sketch, "E8.4.8.0", {"start": v(-40, 11.15) * mm, "end": v(-40, 9.15) * mm});
            skLineSegment(sketch, "E8.4.8.1", {"start": v(-42, 11.15) * mm, "end": v(-42, 9.15) * mm});
            skLineSegment(sketch, "E8.4.8.2", {"start": v(-42, 9.15) * mm, "end": v(-40, 9.15) * mm});
            skLineSegment(sketch, "E8.4.8.3", {"start": v(-42, 11.15) * mm, "end": v(-40, 11.15) * mm});
            skLineSegment(sketch, "E8.4.9.0", {"start": v(-40, 7.15) * mm, "end": v(-40, 5.15) * mm});
            skLineSegment(sketch, "E8.4.9.1", {"start": v(-42, 7.15) * mm, "end": v(-42, 5.15) * mm});
            skLineSegment(sketch, "E8.4.9.2", {"start": v(-42, 5.15) * mm, "end": v(-40, 5.15) * mm});
            skLineSegment(sketch, "E8.4.9.3", {"start": v(-42, 7.15) * mm, "end": v(-40, 7.15) * mm});
            skLineSegment(sketch, "E8.4.10.0", {"start": v(-40, 3.15) * mm, "end": v(-40, 1.15) * mm});
            skLineSegment(sketch, "E8.4.10.1", {"start": v(-42, 3.15) * mm, "end": v(-42, 1.15) * mm});
            skLineSegment(sketch, "E8.4.10.2", {"start": v(-42, 1.15) * mm, "end": v(-40, 1.15) * mm});
            skLineSegment(sketch, "E8.4.10.3", {"start": v(-42, 3.15) * mm, "end": v(-40, 3.15) * mm});
            skLineSegment(sketch, "E8.4.11.0", {"start": v(-40, -0.85) * mm, "end": v(-40, -2.85) * mm});
            skLineSegment(sketch, "E8.4.11.1", {"start": v(-42, -0.85) * mm, "end": v(-42, -2.85) * mm});
            skLineSegment(sketch, "E8.4.11.2", {"start": v(-42, -2.85) * mm, "end": v(-40, -2.85) * mm});
            skLineSegment(sketch, "E8.4.11.3", {"start": v(-42, -0.85) * mm, "end": v(-40, -0.85) * mm});
            skLineSegment(sketch, "E8.4.12.0", {"start": v(-40, -4.85) * mm, "end": v(-40, -6.85) * mm});
            skLineSegment(sketch, "E8.4.12.1", {"start": v(-42, -4.85) * mm, "end": v(-42, -6.85) * mm});
            skLineSegment(sketch, "E8.4.12.2", {"start": v(-42, -6.85) * mm, "end": v(-40, -6.85) * mm});
            skLineSegment(sketch, "E8.4.12.3", {"start": v(-42, -4.85) * mm, "end": v(-40, -4.85) * mm});
            skLineSegment(sketch, "E8.4.13.0", {"start": v(-40, -8.85) * mm, "end": v(-40, -10.85) * mm});
            skLineSegment(sketch, "E8.4.13.1", {"start": v(-42, -8.85) * mm, "end": v(-42, -10.85) * mm});
            skLineSegment(sketch, "E8.4.13.2", {"start": v(-42, -10.85) * mm, "end": v(-40, -10.85) * mm});
            skLineSegment(sketch, "E8.4.13.3", {"start": v(-42, -8.85) * mm, "end": v(-40, -8.85) * mm});
            skLineSegment(sketch, "E8.4.14.0", {"start": v(-40, -12.85) * mm, "end": v(-40, -14.85) * mm});
            skLineSegment(sketch, "E8.4.14.1", {"start": v(-42, -12.85) * mm, "end": v(-42, -14.85) * mm});
            skLineSegment(sketch, "E8.4.14.2", {"start": v(-42, -14.85) * mm, "end": v(-40, -14.85) * mm});
            skLineSegment(sketch, "E8.4.14.3", {"start": v(-42, -12.85) * mm, "end": v(-40, -12.85) * mm});
            skLineSegment(sketch, "E8.4.15.0", {"start": v(-40, -16.85) * mm, "end": v(-40, -18.85) * mm});
            skLineSegment(sketch, "E8.4.15.1", {"start": v(-42, -16.85) * mm, "end": v(-42, -18.85) * mm});
            skLineSegment(sketch, "E8.4.15.2", {"start": v(-42, -18.85) * mm, "end": v(-40, -18.85) * mm});
            skLineSegment(sketch, "E8.4.15.3", {"start": v(-42, -16.85) * mm, "end": v(-40, -16.85) * mm});
            skLineSegment(sketch, "E8.4.16.0", {"start": v(-40, -20.85) * mm, "end": v(-40, -22.85) * mm});
            skLineSegment(sketch, "E8.4.16.1", {"start": v(-42, -20.85) * mm, "end": v(-42, -22.85) * mm});
            skLineSegment(sketch, "E8.4.16.2", {"start": v(-42, -22.85) * mm, "end": v(-40, -22.85) * mm});
            skLineSegment(sketch, "E8.4.16.3", {"start": v(-42, -20.85) * mm, "end": v(-40, -20.85) * mm});
            skLineSegment(sketch, "E8.4.17.0", {"start": v(-40, -24.85) * mm, "end": v(-40, -26.85) * mm});
            skLineSegment(sketch, "E8.4.17.1", {"start": v(-42, -24.85) * mm, "end": v(-42, -26.85) * mm});
            skLineSegment(sketch, "E8.4.17.2", {"start": v(-42, -26.85) * mm, "end": v(-40, -26.85) * mm});
            skLineSegment(sketch, "E8.4.17.3", {"start": v(-42, -24.85) * mm, "end": v(-40, -24.85) * mm});
            skLineSegment(sketch, "E8.4.18.0", {"start": v(-40, -28.85) * mm, "end": v(-40, -30.85) * mm});
            skLineSegment(sketch, "E8.4.18.1", {"start": v(-42, -28.85) * mm, "end": v(-42, -30.85) * mm});
            skLineSegment(sketch, "E8.4.18.2", {"start": v(-42, -30.85) * mm, "end": v(-40, -30.85) * mm});
            skLineSegment(sketch, "E8.4.18.3", {"start": v(-42, -28.85) * mm, "end": v(-40, -28.85) * mm});
            skLineSegment(sketch, "E8.4.19.0", {"start": v(-40, -32.85) * mm, "end": v(-40, -34.85) * mm});
            skLineSegment(sketch, "E8.4.19.1", {"start": v(-42, -32.85) * mm, "end": v(-42, -34.85) * mm});
            skLineSegment(sketch, "E8.4.19.2", {"start": v(-42, -34.85) * mm, "end": v(-40, -34.85) * mm});
            skLineSegment(sketch, "E8.4.19.3", {"start": v(-42, -32.85) * mm, "end": v(-40, -32.85) * mm});
            skLineSegment(sketch, "E8.4.20.0", {"start": v(-40, -36.85) * mm, "end": v(-40, -38.85) * mm});
            skLineSegment(sketch, "E8.4.20.1", {"start": v(-42, -36.85) * mm, "end": v(-42, -38.85) * mm});
            skLineSegment(sketch, "E8.4.20.2", {"start": v(-42, -38.85) * mm, "end": v(-40, -38.85) * mm});
            skLineSegment(sketch, "E8.4.20.3", {"start": v(-42, -36.85) * mm, "end": v(-40, -36.85) * mm});
            skLineSegment(sketch, "E8.4.21.0", {"start": v(-40, -40.85) * mm, "end": v(-40, -42.85) * mm});
            skLineSegment(sketch, "E8.4.21.1", {"start": v(-42, -40.85) * mm, "end": v(-42, -42.85) * mm});
            skLineSegment(sketch, "E8.4.21.2", {"start": v(-42, -42.85) * mm, "end": v(-40, -42.85) * mm});
            skLineSegment(sketch, "E8.4.21.3", {"start": v(-42, -40.85) * mm, "end": v(-40, -40.85) * mm});
            skLineSegment(sketch, "E8.5.0.0", {"start": v(-36, 43.15) * mm, "end": v(-36, 41.15) * mm});
            skLineSegment(sketch, "E8.5.0.1", {"start": v(-38, 43.15) * mm, "end": v(-38, 41.15) * mm});
            skLineSegment(sketch, "E8.5.0.2", {"start": v(-38, 41.15) * mm, "end": v(-36, 41.15) * mm});
            skLineSegment(sketch, "E8.5.0.3", {"start": v(-38, 43.15) * mm, "end": v(-36, 43.15) * mm});
            skLineSegment(sketch, "E8.5.1.0", {"start": v(-36, 39.15) * mm, "end": v(-36, 37.15) * mm});
            skLineSegment(sketch, "E8.5.1.1", {"start": v(-38, 39.15) * mm, "end": v(-38, 37.15) * mm});
            skLineSegment(sketch, "E8.5.1.2", {"start": v(-38, 37.15) * mm, "end": v(-36, 37.15) * mm});
            skLineSegment(sketch, "E8.5.1.3", {"start": v(-38, 39.15) * mm, "end": v(-36, 39.15) * mm});
            skLineSegment(sketch, "E8.5.2.0", {"start": v(-36, 35.15) * mm, "end": v(-36, 33.15) * mm});
            skLineSegment(sketch, "E8.5.2.1", {"start": v(-38, 35.15) * mm, "end": v(-38, 33.15) * mm});
            skLineSegment(sketch, "E8.5.2.2", {"start": v(-38, 33.15) * mm, "end": v(-36, 33.15) * mm});
            skLineSegment(sketch, "E8.5.2.3", {"start": v(-38, 35.15) * mm, "end": v(-36, 35.15) * mm});
            skLineSegment(sketch, "E8.5.3.0", {"start": v(-36, 31.15) * mm, "end": v(-36, 29.15) * mm});
            skLineSegment(sketch, "E8.5.3.1", {"start": v(-38, 31.15) * mm, "end": v(-38, 29.15) * mm});
            skLineSegment(sketch, "E8.5.3.2", {"start": v(-38, 29.15) * mm, "end": v(-36, 29.15) * mm});
            skLineSegment(sketch, "E8.5.3.3", {"start": v(-38, 31.15) * mm, "end": v(-36, 31.15) * mm});
            skLineSegment(sketch, "E8.5.4.0", {"start": v(-36, 27.15) * mm, "end": v(-36, 25.15) * mm});
            skLineSegment(sketch, "E8.5.4.1", {"start": v(-38, 27.15) * mm, "end": v(-38, 25.15) * mm});
            skLineSegment(sketch, "E8.5.4.2", {"start": v(-38, 25.15) * mm, "end": v(-36, 25.15) * mm});
            skLineSegment(sketch, "E8.5.4.3", {"start": v(-38, 27.15) * mm, "end": v(-36, 27.15) * mm});
            skLineSegment(sketch, "E8.5.5.0", {"start": v(-36, 23.15) * mm, "end": v(-36, 21.15) * mm});
            skLineSegment(sketch, "E8.5.5.1", {"start": v(-38, 23.15) * mm, "end": v(-38, 21.15) * mm});
            skLineSegment(sketch, "E8.5.5.2", {"start": v(-38, 21.15) * mm, "end": v(-36, 21.15) * mm});
            skLineSegment(sketch, "E8.5.5.3", {"start": v(-38, 23.15) * mm, "end": v(-36, 23.15) * mm});
            skLineSegment(sketch, "E8.5.6.0", {"start": v(-36, 19.15) * mm, "end": v(-36, 17.15) * mm});
            skLineSegment(sketch, "E8.5.6.1", {"start": v(-38, 19.15) * mm, "end": v(-38, 17.15) * mm});
            skLineSegment(sketch, "E8.5.6.2", {"start": v(-38, 17.15) * mm, "end": v(-36, 17.15) * mm});
            skLineSegment(sketch, "E8.5.6.3", {"start": v(-38, 19.15) * mm, "end": v(-36, 19.15) * mm});
            skLineSegment(sketch, "E8.5.7.0", {"start": v(-36, 15.15) * mm, "end": v(-36, 13.15) * mm});
            skLineSegment(sketch, "E8.5.7.1", {"start": v(-38, 15.15) * mm, "end": v(-38, 13.15) * mm});
            skLineSegment(sketch, "E8.5.7.2", {"start": v(-38, 13.15) * mm, "end": v(-36, 13.15) * mm});
            skLineSegment(sketch, "E8.5.7.3", {"start": v(-38, 15.15) * mm, "end": v(-36, 15.15) * mm});
            skLineSegment(sketch, "E8.5.8.0", {"start": v(-36, 11.15) * mm, "end": v(-36, 9.15) * mm});
            skLineSegment(sketch, "E8.5.8.1", {"start": v(-38, 11.15) * mm, "end": v(-38, 9.15) * mm});
            skLineSegment(sketch, "E8.5.8.2", {"start": v(-38, 9.15) * mm, "end": v(-36, 9.15) * mm});
            skLineSegment(sketch, "E8.5.8.3", {"start": v(-38, 11.15) * mm, "end": v(-36, 11.15) * mm});
            skLineSegment(sketch, "E8.5.9.0", {"start": v(-36, 7.15) * mm, "end": v(-36, 5.15) * mm});
            skLineSegment(sketch, "E8.5.9.1", {"start": v(-38, 7.15) * mm, "end": v(-38, 5.15) * mm});
            skLineSegment(sketch, "E8.5.9.2", {"start": v(-38, 5.15) * mm, "end": v(-36, 5.15) * mm});
            skLineSegment(sketch, "E8.5.9.3", {"start": v(-38, 7.15) * mm, "end": v(-36, 7.15) * mm});
            skLineSegment(sketch, "E8.5.10.0", {"start": v(-36, 3.15) * mm, "end": v(-36, 1.15) * mm});
            skLineSegment(sketch, "E8.5.10.1", {"start": v(-38, 3.15) * mm, "end": v(-38, 1.15) * mm});
            skLineSegment(sketch, "E8.5.10.2", {"start": v(-38, 1.15) * mm, "end": v(-36, 1.15) * mm});
            skLineSegment(sketch, "E8.5.10.3", {"start": v(-38, 3.15) * mm, "end": v(-36, 3.15) * mm});
            skLineSegment(sketch, "E8.5.11.0", {"start": v(-36, -0.85) * mm, "end": v(-36, -2.85) * mm});
            skLineSegment(sketch, "E8.5.11.1", {"start": v(-38, -0.85) * mm, "end": v(-38, -2.85) * mm});
            skLineSegment(sketch, "E8.5.11.2", {"start": v(-38, -2.85) * mm, "end": v(-36, -2.85) * mm});
            skLineSegment(sketch, "E8.5.11.3", {"start": v(-38, -0.85) * mm, "end": v(-36, -0.85) * mm});
            skLineSegment(sketch, "E8.5.12.0", {"start": v(-36, -4.85) * mm, "end": v(-36, -6.85) * mm});
            skLineSegment(sketch, "E8.5.12.1", {"start": v(-38, -4.85) * mm, "end": v(-38, -6.85) * mm});
            skLineSegment(sketch, "E8.5.12.2", {"start": v(-38, -6.85) * mm, "end": v(-36, -6.85) * mm});
            skLineSegment(sketch, "E8.5.12.3", {"start": v(-38, -4.85) * mm, "end": v(-36, -4.85) * mm});
            skLineSegment(sketch, "E8.5.13.0", {"start": v(-36, -8.85) * mm, "end": v(-36, -10.85) * mm});
            skLineSegment(sketch, "E8.5.13.1", {"start": v(-38, -8.85) * mm, "end": v(-38, -10.85) * mm});
            skLineSegment(sketch, "E8.5.13.2", {"start": v(-38, -10.85) * mm, "end": v(-36, -10.85) * mm});
            skLineSegment(sketch, "E8.5.13.3", {"start": v(-38, -8.85) * mm, "end": v(-36, -8.85) * mm});
            skLineSegment(sketch, "E8.5.14.0", {"start": v(-36, -12.85) * mm, "end": v(-36, -14.85) * mm});
            skLineSegment(sketch, "E8.5.14.1", {"start": v(-38, -12.85) * mm, "end": v(-38, -14.85) * mm});
            skLineSegment(sketch, "E8.5.14.2", {"start": v(-38, -14.85) * mm, "end": v(-36, -14.85) * mm});
            skLineSegment(sketch, "E8.5.14.3", {"start": v(-38, -12.85) * mm, "end": v(-36, -12.85) * mm});
            skLineSegment(sketch, "E8.5.15.0", {"start": v(-36, -16.85) * mm, "end": v(-36, -18.85) * mm});
            skLineSegment(sketch, "E8.5.15.1", {"start": v(-38, -16.85) * mm, "end": v(-38, -18.85) * mm});
            skLineSegment(sketch, "E8.5.15.2", {"start": v(-38, -18.85) * mm, "end": v(-36, -18.85) * mm});
            skLineSegment(sketch, "E8.5.15.3", {"start": v(-38, -16.85) * mm, "end": v(-36, -16.85) * mm});
            skLineSegment(sketch, "E8.5.16.0", {"start": v(-36, -20.85) * mm, "end": v(-36, -22.85) * mm});
            skLineSegment(sketch, "E8.5.16.1", {"start": v(-38, -20.85) * mm, "end": v(-38, -22.85) * mm});
            skLineSegment(sketch, "E8.5.16.2", {"start": v(-38, -22.85) * mm, "end": v(-36, -22.85) * mm});
            skLineSegment(sketch, "E8.5.16.3", {"start": v(-38, -20.85) * mm, "end": v(-36, -20.85) * mm});
            skLineSegment(sketch, "E8.5.17.0", {"start": v(-36, -24.85) * mm, "end": v(-36, -26.85) * mm});
            skLineSegment(sketch, "E8.5.17.1", {"start": v(-38, -24.85) * mm, "end": v(-38, -26.85) * mm});
            skLineSegment(sketch, "E8.5.17.2", {"start": v(-38, -26.85) * mm, "end": v(-36, -26.85) * mm});
            skLineSegment(sketch, "E8.5.17.3", {"start": v(-38, -24.85) * mm, "end": v(-36, -24.85) * mm});
            skLineSegment(sketch, "E8.5.18.0", {"start": v(-36, -28.85) * mm, "end": v(-36, -30.85) * mm});
            skLineSegment(sketch, "E8.5.18.1", {"start": v(-38, -28.85) * mm, "end": v(-38, -30.85) * mm});
            skLineSegment(sketch, "E8.5.18.2", {"start": v(-38, -30.85) * mm, "end": v(-36, -30.85) * mm});
            skLineSegment(sketch, "E8.5.18.3", {"start": v(-38, -28.85) * mm, "end": v(-36, -28.85) * mm});
            skLineSegment(sketch, "E8.5.19.0", {"start": v(-36, -32.85) * mm, "end": v(-36, -34.85) * mm});
            skLineSegment(sketch, "E8.5.19.1", {"start": v(-38, -32.85) * mm, "end": v(-38, -34.85) * mm});
            skLineSegment(sketch, "E8.5.19.2", {"start": v(-38, -34.85) * mm, "end": v(-36, -34.85) * mm});
            skLineSegment(sketch, "E8.5.19.3", {"start": v(-38, -32.85) * mm, "end": v(-36, -32.85) * mm});
            skLineSegment(sketch, "E8.5.20.0", {"start": v(-36, -36.85) * mm, "end": v(-36, -38.85) * mm});
            skLineSegment(sketch, "E8.5.20.1", {"start": v(-38, -36.85) * mm, "end": v(-38, -38.85) * mm});
            skLineSegment(sketch, "E8.5.20.2", {"start": v(-38, -38.85) * mm, "end": v(-36, -38.85) * mm});
            skLineSegment(sketch, "E8.5.20.3", {"start": v(-38, -36.85) * mm, "end": v(-36, -36.85) * mm});
            skLineSegment(sketch, "E8.5.21.0", {"start": v(-36, -40.85) * mm, "end": v(-36, -42.85) * mm});
            skLineSegment(sketch, "E8.5.21.1", {"start": v(-38, -40.85) * mm, "end": v(-38, -42.85) * mm});
            skLineSegment(sketch, "E8.5.21.2", {"start": v(-38, -42.85) * mm, "end": v(-36, -42.85) * mm});
            skLineSegment(sketch, "E8.5.21.3", {"start": v(-38, -40.85) * mm, "end": v(-36, -40.85) * mm});
            skLineSegment(sketch, "E8.6.0.0", {"start": v(-32, 43.15) * mm, "end": v(-32, 41.15) * mm});
            skLineSegment(sketch, "E8.6.0.1", {"start": v(-34, 43.15) * mm, "end": v(-34, 41.15) * mm});
            skLineSegment(sketch, "E8.6.0.2", {"start": v(-34, 41.15) * mm, "end": v(-32, 41.15) * mm});
            skLineSegment(sketch, "E8.6.0.3", {"start": v(-34, 43.15) * mm, "end": v(-32, 43.15) * mm});
            skLineSegment(sketch, "E8.6.1.0", {"start": v(-32, 39.15) * mm, "end": v(-32, 37.15) * mm});
            skLineSegment(sketch, "E8.6.1.1", {"start": v(-34, 39.15) * mm, "end": v(-34, 37.15) * mm});
            skLineSegment(sketch, "E8.6.1.2", {"start": v(-34, 37.15) * mm, "end": v(-32, 37.15) * mm});
            skLineSegment(sketch, "E8.6.1.3", {"start": v(-34, 39.15) * mm, "end": v(-32, 39.15) * mm});
            skLineSegment(sketch, "E8.6.2.0", {"start": v(-32, 35.15) * mm, "end": v(-32, 33.15) * mm});
            skLineSegment(sketch, "E8.6.2.1", {"start": v(-34, 35.15) * mm, "end": v(-34, 33.15) * mm});
            skLineSegment(sketch, "E8.6.2.2", {"start": v(-34, 33.15) * mm, "end": v(-32, 33.15) * mm});
            skLineSegment(sketch, "E8.6.2.3", {"start": v(-34, 35.15) * mm, "end": v(-32, 35.15) * mm});
            skLineSegment(sketch, "E8.6.3.0", {"start": v(-32, 31.15) * mm, "end": v(-32, 29.15) * mm});
            skLineSegment(sketch, "E8.6.3.1", {"start": v(-34, 31.15) * mm, "end": v(-34, 29.15) * mm});
            skLineSegment(sketch, "E8.6.3.2", {"start": v(-34, 29.15) * mm, "end": v(-32, 29.15) * mm});
            skLineSegment(sketch, "E8.6.3.3", {"start": v(-34, 31.15) * mm, "end": v(-32, 31.15) * mm});
            skLineSegment(sketch, "E8.6.4.0", {"start": v(-32, 27.15) * mm, "end": v(-32, 25.15) * mm});
            skLineSegment(sketch, "E8.6.4.1", {"start": v(-34, 27.15) * mm, "end": v(-34, 25.15) * mm});
            skLineSegment(sketch, "E8.6.4.2", {"start": v(-34, 25.15) * mm, "end": v(-32, 25.15) * mm});
            skLineSegment(sketch, "E8.6.4.3", {"start": v(-34, 27.15) * mm, "end": v(-32, 27.15) * mm});
            skLineSegment(sketch, "E8.6.5.0", {"start": v(-32, 23.15) * mm, "end": v(-32, 21.15) * mm});
            skLineSegment(sketch, "E8.6.5.1", {"start": v(-34, 23.15) * mm, "end": v(-34, 21.15) * mm});
            skLineSegment(sketch, "E8.6.5.2", {"start": v(-34, 21.15) * mm, "end": v(-32, 21.15) * mm});
            skLineSegment(sketch, "E8.6.5.3", {"start": v(-34, 23.15) * mm, "end": v(-32, 23.15) * mm});
            skLineSegment(sketch, "E8.6.6.0", {"start": v(-32, 19.15) * mm, "end": v(-32, 17.15) * mm});
            skLineSegment(sketch, "E8.6.6.1", {"start": v(-34, 19.15) * mm, "end": v(-34, 17.15) * mm});
            skLineSegment(sketch, "E8.6.6.2", {"start": v(-34, 17.15) * mm, "end": v(-32, 17.15) * mm});
            skLineSegment(sketch, "E8.6.6.3", {"start": v(-34, 19.15) * mm, "end": v(-32, 19.15) * mm});
            skLineSegment(sketch, "E8.6.7.0", {"start": v(-32, 15.15) * mm, "end": v(-32, 13.15) * mm});
            skLineSegment(sketch, "E8.6.7.1", {"start": v(-34, 15.15) * mm, "end": v(-34, 13.15) * mm});
            skLineSegment(sketch, "E8.6.7.2", {"start": v(-34, 13.15) * mm, "end": v(-32, 13.15) * mm});
            skLineSegment(sketch, "E8.6.7.3", {"start": v(-34, 15.15) * mm, "end": v(-32, 15.15) * mm});
            skLineSegment(sketch, "E8.6.8.0", {"start": v(-32, 11.15) * mm, "end": v(-32, 9.15) * mm});
            skLineSegment(sketch, "E8.6.8.1", {"start": v(-34, 11.15) * mm, "end": v(-34, 9.15) * mm});
            skLineSegment(sketch, "E8.6.8.2", {"start": v(-34, 9.15) * mm, "end": v(-32, 9.15) * mm});
            skLineSegment(sketch, "E8.6.8.3", {"start": v(-34, 11.15) * mm, "end": v(-32, 11.15) * mm});
            skLineSegment(sketch, "E8.6.9.0", {"start": v(-32, 7.15) * mm, "end": v(-32, 5.15) * mm});
            skLineSegment(sketch, "E8.6.9.1", {"start": v(-34, 7.15) * mm, "end": v(-34, 5.15) * mm});
            skLineSegment(sketch, "E8.6.9.2", {"start": v(-34, 5.15) * mm, "end": v(-32, 5.15) * mm});
            skLineSegment(sketch, "E8.6.9.3", {"start": v(-34, 7.15) * mm, "end": v(-32, 7.15) * mm});
            skLineSegment(sketch, "E8.6.10.0", {"start": v(-32, 3.15) * mm, "end": v(-32, 1.15) * mm});
            skLineSegment(sketch, "E8.6.10.1", {"start": v(-34, 3.15) * mm, "end": v(-34, 1.15) * mm});
            skLineSegment(sketch, "E8.6.10.2", {"start": v(-34, 1.15) * mm, "end": v(-32, 1.15) * mm});
            skLineSegment(sketch, "E8.6.10.3", {"start": v(-34, 3.15) * mm, "end": v(-32, 3.15) * mm});
            skLineSegment(sketch, "E8.6.11.0", {"start": v(-32, -0.85) * mm, "end": v(-32, -2.85) * mm});
            skLineSegment(sketch, "E8.6.11.1", {"start": v(-34, -0.85) * mm, "end": v(-34, -2.85) * mm});
            skLineSegment(sketch, "E8.6.11.2", {"start": v(-34, -2.85) * mm, "end": v(-32, -2.85) * mm});
            skLineSegment(sketch, "E8.6.11.3", {"start": v(-34, -0.85) * mm, "end": v(-32, -0.85) * mm});
            skLineSegment(sketch, "E8.6.12.0", {"start": v(-32, -4.85) * mm, "end": v(-32, -6.85) * mm});
            skLineSegment(sketch, "E8.6.12.1", {"start": v(-34, -4.85) * mm, "end": v(-34, -6.85) * mm});
            skLineSegment(sketch, "E8.6.12.2", {"start": v(-34, -6.85) * mm, "end": v(-32, -6.85) * mm});
            skLineSegment(sketch, "E8.6.12.3", {"start": v(-34, -4.85) * mm, "end": v(-32, -4.85) * mm});
            skLineSegment(sketch, "E8.6.13.0", {"start": v(-32, -8.85) * mm, "end": v(-32, -10.85) * mm});
            skLineSegment(sketch, "E8.6.13.1", {"start": v(-34, -8.85) * mm, "end": v(-34, -10.85) * mm});
            skLineSegment(sketch, "E8.6.13.2", {"start": v(-34, -10.85) * mm, "end": v(-32, -10.85) * mm});
            skLineSegment(sketch, "E8.6.13.3", {"start": v(-34, -8.85) * mm, "end": v(-32, -8.85) * mm});
            skLineSegment(sketch, "E8.6.14.0", {"start": v(-32, -12.85) * mm, "end": v(-32, -14.85) * mm});
            skLineSegment(sketch, "E8.6.14.1", {"start": v(-34, -12.85) * mm, "end": v(-34, -14.85) * mm});
            skLineSegment(sketch, "E8.6.14.2", {"start": v(-34, -14.85) * mm, "end": v(-32, -14.85) * mm});
            skLineSegment(sketch, "E8.6.14.3", {"start": v(-34, -12.85) * mm, "end": v(-32, -12.85) * mm});
            skLineSegment(sketch, "E8.6.15.0", {"start": v(-32, -16.85) * mm, "end": v(-32, -18.85) * mm});
            skLineSegment(sketch, "E8.6.15.1", {"start": v(-34, -16.85) * mm, "end": v(-34, -18.85) * mm});
            skLineSegment(sketch, "E8.6.15.2", {"start": v(-34, -18.85) * mm, "end": v(-32, -18.85) * mm});
            skLineSegment(sketch, "E8.6.15.3", {"start": v(-34, -16.85) * mm, "end": v(-32, -16.85) * mm});
            skLineSegment(sketch, "E8.6.16.0", {"start": v(-32, -20.85) * mm, "end": v(-32, -22.85) * mm});
            skLineSegment(sketch, "E8.6.16.1", {"start": v(-34, -20.85) * mm, "end": v(-34, -22.85) * mm});
            skLineSegment(sketch, "E8.6.16.2", {"start": v(-34, -22.85) * mm, "end": v(-32, -22.85) * mm});
            skLineSegment(sketch, "E8.6.16.3", {"start": v(-34, -20.85) * mm, "end": v(-32, -20.85) * mm});
            skLineSegment(sketch, "E8.6.17.0", {"start": v(-32, -24.85) * mm, "end": v(-32, -26.85) * mm});
            skLineSegment(sketch, "E8.6.17.1", {"start": v(-34, -24.85) * mm, "end": v(-34, -26.85) * mm});
            skLineSegment(sketch, "E8.6.17.2", {"start": v(-34, -26.85) * mm, "end": v(-32, -26.85) * mm});
            skLineSegment(sketch, "E8.6.17.3", {"start": v(-34, -24.85) * mm, "end": v(-32, -24.85) * mm});
            skLineSegment(sketch, "E8.6.18.0", {"start": v(-32, -28.85) * mm, "end": v(-32, -30.85) * mm});
            skLineSegment(sketch, "E8.6.18.1", {"start": v(-34, -28.85) * mm, "end": v(-34, -30.85) * mm});
            skLineSegment(sketch, "E8.6.18.2", {"start": v(-34, -30.85) * mm, "end": v(-32, -30.85) * mm});
            skLineSegment(sketch, "E8.6.18.3", {"start": v(-34, -28.85) * mm, "end": v(-32, -28.85) * mm});
            skLineSegment(sketch, "E8.6.19.0", {"start": v(-32, -32.85) * mm, "end": v(-32, -34.85) * mm});
            skLineSegment(sketch, "E8.6.19.1", {"start": v(-34, -32.85) * mm, "end": v(-34, -34.85) * mm});
            skLineSegment(sketch, "E8.6.19.2", {"start": v(-34, -34.85) * mm, "end": v(-32, -34.85) * mm});
            skLineSegment(sketch, "E8.6.19.3", {"start": v(-34, -32.85) * mm, "end": v(-32, -32.85) * mm});
            skLineSegment(sketch, "E8.6.20.0", {"start": v(-32, -36.85) * mm, "end": v(-32, -38.85) * mm});
            skLineSegment(sketch, "E8.6.20.1", {"start": v(-34, -36.85) * mm, "end": v(-34, -38.85) * mm});
            skLineSegment(sketch, "E8.6.20.2", {"start": v(-34, -38.85) * mm, "end": v(-32, -38.85) * mm});
            skLineSegment(sketch, "E8.6.20.3", {"start": v(-34, -36.85) * mm, "end": v(-32, -36.85) * mm});
            skLineSegment(sketch, "E8.6.21.0", {"start": v(-32, -40.85) * mm, "end": v(-32, -42.85) * mm});
            skLineSegment(sketch, "E8.6.21.1", {"start": v(-34, -40.85) * mm, "end": v(-34, -42.85) * mm});
            skLineSegment(sketch, "E8.6.21.2", {"start": v(-34, -42.85) * mm, "end": v(-32, -42.85) * mm});
            skLineSegment(sketch, "E8.6.21.3", {"start": v(-34, -40.85) * mm, "end": v(-32, -40.85) * mm});
            skLineSegment(sketch, "E8.7.0.0", {"start": v(-28, 43.15) * mm, "end": v(-28, 41.15) * mm});
            skLineSegment(sketch, "E8.7.0.1", {"start": v(-30, 43.15) * mm, "end": v(-30, 41.15) * mm});
            skLineSegment(sketch, "E8.7.0.2", {"start": v(-30, 41.15) * mm, "end": v(-28, 41.15) * mm});
            skLineSegment(sketch, "E8.7.0.3", {"start": v(-30, 43.15) * mm, "end": v(-28, 43.15) * mm});
            skLineSegment(sketch, "E8.7.1.0", {"start": v(-28, 39.15) * mm, "end": v(-28, 37.15) * mm});
            skLineSegment(sketch, "E8.7.1.1", {"start": v(-30, 39.15) * mm, "end": v(-30, 37.15) * mm});
            skLineSegment(sketch, "E8.7.1.2", {"start": v(-30, 37.15) * mm, "end": v(-28, 37.15) * mm});
            skLineSegment(sketch, "E8.7.1.3", {"start": v(-30, 39.15) * mm, "end": v(-28, 39.15) * mm});
            skLineSegment(sketch, "E8.7.2.0", {"start": v(-28, 35.15) * mm, "end": v(-28, 33.15) * mm});
            skLineSegment(sketch, "E8.7.2.1", {"start": v(-30, 35.15) * mm, "end": v(-30, 33.15) * mm});
            skLineSegment(sketch, "E8.7.2.2", {"start": v(-30, 33.15) * mm, "end": v(-28, 33.15) * mm});
            skLineSegment(sketch, "E8.7.2.3", {"start": v(-30, 35.15) * mm, "end": v(-28, 35.15) * mm});
            skLineSegment(sketch, "E8.7.3.0", {"start": v(-28, 31.15) * mm, "end": v(-28, 29.15) * mm});
            skLineSegment(sketch, "E8.7.3.1", {"start": v(-30, 31.15) * mm, "end": v(-30, 29.15) * mm});
            skLineSegment(sketch, "E8.7.3.2", {"start": v(-30, 29.15) * mm, "end": v(-28, 29.15) * mm});
            skLineSegment(sketch, "E8.7.3.3", {"start": v(-30, 31.15) * mm, "end": v(-28, 31.15) * mm});
            skLineSegment(sketch, "E8.7.4.0", {"start": v(-28, 27.15) * mm, "end": v(-28, 25.15) * mm});
            skLineSegment(sketch, "E8.7.4.1", {"start": v(-30, 27.15) * mm, "end": v(-30, 25.15) * mm});
            skLineSegment(sketch, "E8.7.4.2", {"start": v(-30, 25.15) * mm, "end": v(-28, 25.15) * mm});
            skLineSegment(sketch, "E8.7.4.3", {"start": v(-30, 27.15) * mm, "end": v(-28, 27.15) * mm});
            skLineSegment(sketch, "E8.7.5.0", {"start": v(-28, 23.15) * mm, "end": v(-28, 21.15) * mm});
            skLineSegment(sketch, "E8.7.5.1", {"start": v(-30, 23.15) * mm, "end": v(-30, 21.15) * mm});
            skLineSegment(sketch, "E8.7.5.2", {"start": v(-30, 21.15) * mm, "end": v(-28, 21.15) * mm});
            skLineSegment(sketch, "E8.7.5.3", {"start": v(-30, 23.15) * mm, "end": v(-28, 23.15) * mm});
            skLineSegment(sketch, "E8.7.6.0", {"start": v(-28, 19.15) * mm, "end": v(-28, 17.15) * mm});
            skLineSegment(sketch, "E8.7.6.1", {"start": v(-30, 19.15) * mm, "end": v(-30, 17.15) * mm});
            skLineSegment(sketch, "E8.7.6.2", {"start": v(-30, 17.15) * mm, "end": v(-28, 17.15) * mm});
            skLineSegment(sketch, "E8.7.6.3", {"start": v(-30, 19.15) * mm, "end": v(-28, 19.15) * mm});
            skLineSegment(sketch, "E8.7.7.0", {"start": v(-28, 15.15) * mm, "end": v(-28, 13.15) * mm});
            skLineSegment(sketch, "E8.7.7.1", {"start": v(-30, 15.15) * mm, "end": v(-30, 13.15) * mm});
            skLineSegment(sketch, "E8.7.7.2", {"start": v(-30, 13.15) * mm, "end": v(-28, 13.15) * mm});
            skLineSegment(sketch, "E8.7.7.3", {"start": v(-30, 15.15) * mm, "end": v(-28, 15.15) * mm});
            skLineSegment(sketch, "E8.7.8.0", {"start": v(-28, 11.15) * mm, "end": v(-28, 9.15) * mm});
            skLineSegment(sketch, "E8.7.8.1", {"start": v(-30, 11.15) * mm, "end": v(-30, 9.15) * mm});
            skLineSegment(sketch, "E8.7.8.2", {"start": v(-30, 9.15) * mm, "end": v(-28, 9.15) * mm});
            skLineSegment(sketch, "E8.7.8.3", {"start": v(-30, 11.15) * mm, "end": v(-28, 11.15) * mm});
            skLineSegment(sketch, "E8.7.9.0", {"start": v(-28, 7.15) * mm, "end": v(-28, 5.15) * mm});
            skLineSegment(sketch, "E8.7.9.1", {"start": v(-30, 7.15) * mm, "end": v(-30, 5.15) * mm});
            skLineSegment(sketch, "E8.7.9.2", {"start": v(-30, 5.15) * mm, "end": v(-28, 5.15) * mm});
            skLineSegment(sketch, "E8.7.9.3", {"start": v(-30, 7.15) * mm, "end": v(-28, 7.15) * mm});
            skLineSegment(sketch, "E8.7.10.0", {"start": v(-28, 3.15) * mm, "end": v(-28, 1.15) * mm});
            skLineSegment(sketch, "E8.7.10.1", {"start": v(-30, 3.15) * mm, "end": v(-30, 1.15) * mm});
            skLineSegment(sketch, "E8.7.10.2", {"start": v(-30, 1.15) * mm, "end": v(-28, 1.15) * mm});
            skLineSegment(sketch, "E8.7.10.3", {"start": v(-30, 3.15) * mm, "end": v(-28, 3.15) * mm});
            skLineSegment(sketch, "E8.7.11.0", {"start": v(-28, -0.85) * mm, "end": v(-28, -2.85) * mm});
            skLineSegment(sketch, "E8.7.11.1", {"start": v(-30, -0.85) * mm, "end": v(-30, -2.85) * mm});
            skLineSegment(sketch, "E8.7.11.2", {"start": v(-30, -2.85) * mm, "end": v(-28, -2.85) * mm});
            skLineSegment(sketch, "E8.7.11.3", {"start": v(-30, -0.85) * mm, "end": v(-28, -0.85) * mm});
            skLineSegment(sketch, "E8.7.12.0", {"start": v(-28, -4.85) * mm, "end": v(-28, -6.85) * mm});
            skLineSegment(sketch, "E8.7.12.1", {"start": v(-30, -4.85) * mm, "end": v(-30, -6.85) * mm});
            skLineSegment(sketch, "E8.7.12.2", {"start": v(-30, -6.85) * mm, "end": v(-28, -6.85) * mm});
            skLineSegment(sketch, "E8.7.12.3", {"start": v(-30, -4.85) * mm, "end": v(-28, -4.85) * mm});
            skLineSegment(sketch, "E8.7.13.0", {"start": v(-28, -8.85) * mm, "end": v(-28, -10.85) * mm});
            skLineSegment(sketch, "E8.7.13.1", {"start": v(-30, -8.85) * mm, "end": v(-30, -10.85) * mm});
            skLineSegment(sketch, "E8.7.13.2", {"start": v(-30, -10.85) * mm, "end": v(-28, -10.85) * mm});
            skLineSegment(sketch, "E8.7.13.3", {"start": v(-30, -8.85) * mm, "end": v(-28, -8.85) * mm});
            skLineSegment(sketch, "E8.7.14.0", {"start": v(-28, -12.85) * mm, "end": v(-28, -14.85) * mm});
            skLineSegment(sketch, "E8.7.14.1", {"start": v(-30, -12.85) * mm, "end": v(-30, -14.85) * mm});
            skLineSegment(sketch, "E8.7.14.2", {"start": v(-30, -14.85) * mm, "end": v(-28, -14.85) * mm});
            skLineSegment(sketch, "E8.7.14.3", {"start": v(-30, -12.85) * mm, "end": v(-28, -12.85) * mm});
            skLineSegment(sketch, "E8.7.15.0", {"start": v(-28, -16.85) * mm, "end": v(-28, -18.85) * mm});
            skLineSegment(sketch, "E8.7.15.1", {"start": v(-30, -16.85) * mm, "end": v(-30, -18.85) * mm});
            skLineSegment(sketch, "E8.7.15.2", {"start": v(-30, -18.85) * mm, "end": v(-28, -18.85) * mm});
            skLineSegment(sketch, "E8.7.15.3", {"start": v(-30, -16.85) * mm, "end": v(-28, -16.85) * mm});
            skLineSegment(sketch, "E8.7.16.0", {"start": v(-28, -20.85) * mm, "end": v(-28, -22.85) * mm});
            skLineSegment(sketch, "E8.7.16.1", {"start": v(-30, -20.85) * mm, "end": v(-30, -22.85) * mm});
            skLineSegment(sketch, "E8.7.16.2", {"start": v(-30, -22.85) * mm, "end": v(-28, -22.85) * mm});
            skLineSegment(sketch, "E8.7.16.3", {"start": v(-30, -20.85) * mm, "end": v(-28, -20.85) * mm});
            skLineSegment(sketch, "E8.7.17.0", {"start": v(-28, -24.85) * mm, "end": v(-28, -26.85) * mm});
            skLineSegment(sketch, "E8.7.17.1", {"start": v(-30, -24.85) * mm, "end": v(-30, -26.85) * mm});
            skLineSegment(sketch, "E8.7.17.2", {"start": v(-30, -26.85) * mm, "end": v(-28, -26.85) * mm});
            skLineSegment(sketch, "E8.7.17.3", {"start": v(-30, -24.85) * mm, "end": v(-28, -24.85) * mm});
            skLineSegment(sketch, "E8.7.18.0", {"start": v(-28, -28.85) * mm, "end": v(-28, -30.85) * mm});
            skLineSegment(sketch, "E8.7.18.1", {"start": v(-30, -28.85) * mm, "end": v(-30, -30.85) * mm});
            skLineSegment(sketch, "E8.7.18.2", {"start": v(-30, -30.85) * mm, "end": v(-28, -30.85) * mm});
            skLineSegment(sketch, "E8.7.18.3", {"start": v(-30, -28.85) * mm, "end": v(-28, -28.85) * mm});
            skLineSegment(sketch, "E8.7.19.0", {"start": v(-28, -32.85) * mm, "end": v(-28, -34.85) * mm});
            skLineSegment(sketch, "E8.7.19.1", {"start": v(-30, -32.85) * mm, "end": v(-30, -34.85) * mm});
            skLineSegment(sketch, "E8.7.19.2", {"start": v(-30, -34.85) * mm, "end": v(-28, -34.85) * mm});
            skLineSegment(sketch, "E8.7.19.3", {"start": v(-30, -32.85) * mm, "end": v(-28, -32.85) * mm});
            skLineSegment(sketch, "E8.7.20.0", {"start": v(-28, -36.85) * mm, "end": v(-28, -38.85) * mm});
            skLineSegment(sketch, "E8.7.20.1", {"start": v(-30, -36.85) * mm, "end": v(-30, -38.85) * mm});
            skLineSegment(sketch, "E8.7.20.2", {"start": v(-30, -38.85) * mm, "end": v(-28, -38.85) * mm});
            skLineSegment(sketch, "E8.7.20.3", {"start": v(-30, -36.85) * mm, "end": v(-28, -36.85) * mm});
            skLineSegment(sketch, "E8.7.21.0", {"start": v(-28, -40.85) * mm, "end": v(-28, -42.85) * mm});
            skLineSegment(sketch, "E8.7.21.1", {"start": v(-30, -40.85) * mm, "end": v(-30, -42.85) * mm});
            skLineSegment(sketch, "E8.7.21.2", {"start": v(-30, -42.85) * mm, "end": v(-28, -42.85) * mm});
            skLineSegment(sketch, "E8.7.21.3", {"start": v(-30, -40.85) * mm, "end": v(-28, -40.85) * mm});
            skLineSegment(sketch, "E8.8.0.0", {"start": v(-24, 43.15) * mm, "end": v(-24, 41.15) * mm});
            skLineSegment(sketch, "E8.8.0.1", {"start": v(-26, 43.15) * mm, "end": v(-26, 41.15) * mm});
            skLineSegment(sketch, "E8.8.0.2", {"start": v(-26, 41.15) * mm, "end": v(-24, 41.15) * mm});
            skLineSegment(sketch, "E8.8.0.3", {"start": v(-26, 43.15) * mm, "end": v(-24, 43.15) * mm});
            skLineSegment(sketch, "E8.8.1.0", {"start": v(-24, 39.15) * mm, "end": v(-24, 37.15) * mm});
            skLineSegment(sketch, "E8.8.1.1", {"start": v(-26, 39.15) * mm, "end": v(-26, 37.15) * mm});
            skLineSegment(sketch, "E8.8.1.2", {"start": v(-26, 37.15) * mm, "end": v(-24, 37.15) * mm});
            skLineSegment(sketch, "E8.8.1.3", {"start": v(-26, 39.15) * mm, "end": v(-24, 39.15) * mm});
            skLineSegment(sketch, "E8.8.2.0", {"start": v(-24, 35.15) * mm, "end": v(-24, 33.15) * mm});
            skLineSegment(sketch, "E8.8.2.1", {"start": v(-26, 35.15) * mm, "end": v(-26, 33.15) * mm});
            skLineSegment(sketch, "E8.8.2.2", {"start": v(-26, 33.15) * mm, "end": v(-24, 33.15) * mm});
            skLineSegment(sketch, "E8.8.2.3", {"start": v(-26, 35.15) * mm, "end": v(-24, 35.15) * mm});
            skLineSegment(sketch, "E8.8.3.0", {"start": v(-24, 31.15) * mm, "end": v(-24, 29.15) * mm});
            skLineSegment(sketch, "E8.8.3.1", {"start": v(-26, 31.15) * mm, "end": v(-26, 29.15) * mm});
            skLineSegment(sketch, "E8.8.3.2", {"start": v(-26, 29.15) * mm, "end": v(-24, 29.15) * mm});
            skLineSegment(sketch, "E8.8.3.3", {"start": v(-26, 31.15) * mm, "end": v(-24, 31.15) * mm});
            skLineSegment(sketch, "E8.8.4.0", {"start": v(-24, 27.15) * mm, "end": v(-24, 25.15) * mm});
            skLineSegment(sketch, "E8.8.4.1", {"start": v(-26, 27.15) * mm, "end": v(-26, 25.15) * mm});
            skLineSegment(sketch, "E8.8.4.2", {"start": v(-26, 25.15) * mm, "end": v(-24, 25.15) * mm});
            skLineSegment(sketch, "E8.8.4.3", {"start": v(-26, 27.15) * mm, "end": v(-24, 27.15) * mm});
            skLineSegment(sketch, "E8.8.5.0", {"start": v(-24, 23.15) * mm, "end": v(-24, 21.15) * mm});
            skLineSegment(sketch, "E8.8.5.1", {"start": v(-26, 23.15) * mm, "end": v(-26, 21.15) * mm});
            skLineSegment(sketch, "E8.8.5.2", {"start": v(-26, 21.15) * mm, "end": v(-24, 21.15) * mm});
            skLineSegment(sketch, "E8.8.5.3", {"start": v(-26, 23.15) * mm, "end": v(-24, 23.15) * mm});
            skLineSegment(sketch, "E8.8.6.0", {"start": v(-24, 19.15) * mm, "end": v(-24, 17.15) * mm});
            skLineSegment(sketch, "E8.8.6.1", {"start": v(-26, 19.15) * mm, "end": v(-26, 17.15) * mm});
            skLineSegment(sketch, "E8.8.6.2", {"start": v(-26, 17.15) * mm, "end": v(-24, 17.15) * mm});
            skLineSegment(sketch, "E8.8.6.3", {"start": v(-26, 19.15) * mm, "end": v(-24, 19.15) * mm});
            skLineSegment(sketch, "E8.8.7.0", {"start": v(-24, 15.15) * mm, "end": v(-24, 13.15) * mm});
            skLineSegment(sketch, "E8.8.7.1", {"start": v(-26, 15.15) * mm, "end": v(-26, 13.15) * mm});
            skLineSegment(sketch, "E8.8.7.2", {"start": v(-26, 13.15) * mm, "end": v(-24, 13.15) * mm});
            skLineSegment(sketch, "E8.8.7.3", {"start": v(-26, 15.15) * mm, "end": v(-24, 15.15) * mm});
            skLineSegment(sketch, "E8.8.8.0", {"start": v(-24, 11.15) * mm, "end": v(-24, 9.15) * mm});
            skLineSegment(sketch, "E8.8.8.1", {"start": v(-26, 11.15) * mm, "end": v(-26, 9.15) * mm});
            skLineSegment(sketch, "E8.8.8.2", {"start": v(-26, 9.15) * mm, "end": v(-24, 9.15) * mm});
            skLineSegment(sketch, "E8.8.8.3", {"start": v(-26, 11.15) * mm, "end": v(-24, 11.15) * mm});
            skLineSegment(sketch, "E8.8.9.0", {"start": v(-24, 7.15) * mm, "end": v(-24, 5.15) * mm});
            skLineSegment(sketch, "E8.8.9.1", {"start": v(-26, 7.15) * mm, "end": v(-26, 5.15) * mm});
            skLineSegment(sketch, "E8.8.9.2", {"start": v(-26, 5.15) * mm, "end": v(-24, 5.15) * mm});
            skLineSegment(sketch, "E8.8.9.3", {"start": v(-26, 7.15) * mm, "end": v(-24, 7.15) * mm});
            skLineSegment(sketch, "E8.8.10.0", {"start": v(-24, 3.15) * mm, "end": v(-24, 1.15) * mm});
            skLineSegment(sketch, "E8.8.10.1", {"start": v(-26, 3.15) * mm, "end": v(-26, 1.15) * mm});
            skLineSegment(sketch, "E8.8.10.2", {"start": v(-26, 1.15) * mm, "end": v(-24, 1.15) * mm});
            skLineSegment(sketch, "E8.8.10.3", {"start": v(-26, 3.15) * mm, "end": v(-24, 3.15) * mm});
            skLineSegment(sketch, "E8.8.11.0", {"start": v(-24, -0.85) * mm, "end": v(-24, -2.85) * mm});
            skLineSegment(sketch, "E8.8.11.1", {"start": v(-26, -0.85) * mm, "end": v(-26, -2.85) * mm});
            skLineSegment(sketch, "E8.8.11.2", {"start": v(-26, -2.85) * mm, "end": v(-24, -2.85) * mm});
            skLineSegment(sketch, "E8.8.11.3", {"start": v(-26, -0.85) * mm, "end": v(-24, -0.85) * mm});
            skLineSegment(sketch, "E8.8.12.0", {"start": v(-24, -4.85) * mm, "end": v(-24, -6.85) * mm});
            skLineSegment(sketch, "E8.8.12.1", {"start": v(-26, -4.85) * mm, "end": v(-26, -6.85) * mm});
            skLineSegment(sketch, "E8.8.12.2", {"start": v(-26, -6.85) * mm, "end": v(-24, -6.85) * mm});
            skLineSegment(sketch, "E8.8.12.3", {"start": v(-26, -4.85) * mm, "end": v(-24, -4.85) * mm});
            skLineSegment(sketch, "E8.8.13.0", {"start": v(-24, -8.85) * mm, "end": v(-24, -10.85) * mm});
            skLineSegment(sketch, "E8.8.13.1", {"start": v(-26, -8.85) * mm, "end": v(-26, -10.85) * mm});
            skLineSegment(sketch, "E8.8.13.2", {"start": v(-26, -10.85) * mm, "end": v(-24, -10.85) * mm});
            skLineSegment(sketch, "E8.8.13.3", {"start": v(-26, -8.85) * mm, "end": v(-24, -8.85) * mm});
            skLineSegment(sketch, "E8.8.14.0", {"start": v(-24, -12.85) * mm, "end": v(-24, -14.85) * mm});
            skLineSegment(sketch, "E8.8.14.1", {"start": v(-26, -12.85) * mm, "end": v(-26, -14.85) * mm});
            skLineSegment(sketch, "E8.8.14.2", {"start": v(-26, -14.85) * mm, "end": v(-24, -14.85) * mm});
            skLineSegment(sketch, "E8.8.14.3", {"start": v(-26, -12.85) * mm, "end": v(-24, -12.85) * mm});
            skLineSegment(sketch, "E8.8.15.0", {"start": v(-24, -16.85) * mm, "end": v(-24, -18.85) * mm});
            skLineSegment(sketch, "E8.8.15.1", {"start": v(-26, -16.85) * mm, "end": v(-26, -18.85) * mm});
            skLineSegment(sketch, "E8.8.15.2", {"start": v(-26, -18.85) * mm, "end": v(-24, -18.85) * mm});
            skLineSegment(sketch, "E8.8.15.3", {"start": v(-26, -16.85) * mm, "end": v(-24, -16.85) * mm});
            skLineSegment(sketch, "E8.8.16.0", {"start": v(-24, -20.85) * mm, "end": v(-24, -22.85) * mm});
            skLineSegment(sketch, "E8.8.16.1", {"start": v(-26, -20.85) * mm, "end": v(-26, -22.85) * mm});
            skLineSegment(sketch, "E8.8.16.2", {"start": v(-26, -22.85) * mm, "end": v(-24, -22.85) * mm});
            skLineSegment(sketch, "E8.8.16.3", {"start": v(-26, -20.85) * mm, "end": v(-24, -20.85) * mm});
            skLineSegment(sketch, "E8.8.17.0", {"start": v(-24, -24.85) * mm, "end": v(-24, -26.85) * mm});
            skLineSegment(sketch, "E8.8.17.1", {"start": v(-26, -24.85) * mm, "end": v(-26, -26.85) * mm});
            skLineSegment(sketch, "E8.8.17.2", {"start": v(-26, -26.85) * mm, "end": v(-24, -26.85) * mm});
            skLineSegment(sketch, "E8.8.17.3", {"start": v(-26, -24.85) * mm, "end": v(-24, -24.85) * mm});
            skLineSegment(sketch, "E8.8.18.0", {"start": v(-24, -28.85) * mm, "end": v(-24, -30.85) * mm});
            skLineSegment(sketch, "E8.8.18.1", {"start": v(-26, -28.85) * mm, "end": v(-26, -30.85) * mm});
            skLineSegment(sketch, "E8.8.18.2", {"start": v(-26, -30.85) * mm, "end": v(-24, -30.85) * mm});
            skLineSegment(sketch, "E8.8.18.3", {"start": v(-26, -28.85) * mm, "end": v(-24, -28.85) * mm});
            skLineSegment(sketch, "E8.8.19.0", {"start": v(-24, -32.85) * mm, "end": v(-24, -34.85) * mm});
            skLineSegment(sketch, "E8.8.19.1", {"start": v(-26, -32.85) * mm, "end": v(-26, -34.85) * mm});
            skLineSegment(sketch, "E8.8.19.2", {"start": v(-26, -34.85) * mm, "end": v(-24, -34.85) * mm});
            skLineSegment(sketch, "E8.8.19.3", {"start": v(-26, -32.85) * mm, "end": v(-24, -32.85) * mm});
            skLineSegment(sketch, "E8.8.20.0", {"start": v(-24, -36.85) * mm, "end": v(-24, -38.85) * mm});
            skLineSegment(sketch, "E8.8.20.1", {"start": v(-26, -36.85) * mm, "end": v(-26, -38.85) * mm});
            skLineSegment(sketch, "E8.8.20.2", {"start": v(-26, -38.85) * mm, "end": v(-24, -38.85) * mm});
            skLineSegment(sketch, "E8.8.20.3", {"start": v(-26, -36.85) * mm, "end": v(-24, -36.85) * mm});
            skLineSegment(sketch, "E8.8.21.0", {"start": v(-24, -40.85) * mm, "end": v(-24, -42.85) * mm});
            skLineSegment(sketch, "E8.8.21.1", {"start": v(-26, -40.85) * mm, "end": v(-26, -42.85) * mm});
            skLineSegment(sketch, "E8.8.21.2", {"start": v(-26, -42.85) * mm, "end": v(-24, -42.85) * mm});
            skLineSegment(sketch, "E8.8.21.3", {"start": v(-26, -40.85) * mm, "end": v(-24, -40.85) * mm});
            skLineSegment(sketch, "E8.9.0.0", {"start": v(-20, 43.15) * mm, "end": v(-20, 41.15) * mm});
            skLineSegment(sketch, "E8.9.0.1", {"start": v(-22, 43.15) * mm, "end": v(-22, 41.15) * mm});
            skLineSegment(sketch, "E8.9.0.2", {"start": v(-22, 41.15) * mm, "end": v(-20, 41.15) * mm});
            skLineSegment(sketch, "E8.9.0.3", {"start": v(-22, 43.15) * mm, "end": v(-20, 43.15) * mm});
            skLineSegment(sketch, "E8.9.1.0", {"start": v(-20, 39.15) * mm, "end": v(-20, 37.15) * mm});
            skLineSegment(sketch, "E8.9.1.1", {"start": v(-22, 39.15) * mm, "end": v(-22, 37.15) * mm});
            skLineSegment(sketch, "E8.9.1.2", {"start": v(-22, 37.15) * mm, "end": v(-20, 37.15) * mm});
            skLineSegment(sketch, "E8.9.1.3", {"start": v(-22, 39.15) * mm, "end": v(-20, 39.15) * mm});
            skLineSegment(sketch, "E8.9.2.0", {"start": v(-20, 35.15) * mm, "end": v(-20, 33.15) * mm});
            skLineSegment(sketch, "E8.9.2.1", {"start": v(-22, 35.15) * mm, "end": v(-22, 33.15) * mm});
            skLineSegment(sketch, "E8.9.2.2", {"start": v(-22, 33.15) * mm, "end": v(-20, 33.15) * mm});
            skLineSegment(sketch, "E8.9.2.3", {"start": v(-22, 35.15) * mm, "end": v(-20, 35.15) * mm});
            skLineSegment(sketch, "E8.9.3.0", {"start": v(-20, 31.15) * mm, "end": v(-20, 29.15) * mm});
            skLineSegment(sketch, "E8.9.3.1", {"start": v(-22, 31.15) * mm, "end": v(-22, 29.15) * mm});
            skLineSegment(sketch, "E8.9.3.2", {"start": v(-22, 29.15) * mm, "end": v(-20, 29.15) * mm});
            skLineSegment(sketch, "E8.9.3.3", {"start": v(-22, 31.15) * mm, "end": v(-20, 31.15) * mm});
            skLineSegment(sketch, "E8.9.4.0", {"start": v(-20, 27.15) * mm, "end": v(-20, 25.15) * mm});
            skLineSegment(sketch, "E8.9.4.1", {"start": v(-22, 27.15) * mm, "end": v(-22, 25.15) * mm});
            skLineSegment(sketch, "E8.9.4.2", {"start": v(-22, 25.15) * mm, "end": v(-20, 25.15) * mm});
            skLineSegment(sketch, "E8.9.4.3", {"start": v(-22, 27.15) * mm, "end": v(-20, 27.15) * mm});
            skLineSegment(sketch, "E8.9.5.0", {"start": v(-20, 23.15) * mm, "end": v(-20, 21.15) * mm});
            skLineSegment(sketch, "E8.9.5.1", {"start": v(-22, 23.15) * mm, "end": v(-22, 21.15) * mm});
            skLineSegment(sketch, "E8.9.5.2", {"start": v(-22, 21.15) * mm, "end": v(-20, 21.15) * mm});
            skLineSegment(sketch, "E8.9.5.3", {"start": v(-22, 23.15) * mm, "end": v(-20, 23.15) * mm});
            skLineSegment(sketch, "E8.9.6.0", {"start": v(-20, 19.15) * mm, "end": v(-20, 17.15) * mm});
            skLineSegment(sketch, "E8.9.6.1", {"start": v(-22, 19.15) * mm, "end": v(-22, 17.15) * mm});
            skLineSegment(sketch, "E8.9.6.2", {"start": v(-22, 17.15) * mm, "end": v(-20, 17.15) * mm});
            skLineSegment(sketch, "E8.9.6.3", {"start": v(-22, 19.15) * mm, "end": v(-20, 19.15) * mm});
            skLineSegment(sketch, "E8.9.7.0", {"start": v(-20, 15.15) * mm, "end": v(-20, 13.15) * mm});
            skLineSegment(sketch, "E8.9.7.1", {"start": v(-22, 15.15) * mm, "end": v(-22, 13.15) * mm});
            skLineSegment(sketch, "E8.9.7.2", {"start": v(-22, 13.15) * mm, "end": v(-20, 13.15) * mm});
            skLineSegment(sketch, "E8.9.7.3", {"start": v(-22, 15.15) * mm, "end": v(-20, 15.15) * mm});
            skLineSegment(sketch, "E8.9.8.0", {"start": v(-20, 11.15) * mm, "end": v(-20, 9.15) * mm});
            skLineSegment(sketch, "E8.9.8.1", {"start": v(-22, 11.15) * mm, "end": v(-22, 9.15) * mm});
            skLineSegment(sketch, "E8.9.8.2", {"start": v(-22, 9.15) * mm, "end": v(-20, 9.15) * mm});
            skLineSegment(sketch, "E8.9.8.3", {"start": v(-22, 11.15) * mm, "end": v(-20, 11.15) * mm});
            skLineSegment(sketch, "E8.9.9.0", {"start": v(-20, 7.15) * mm, "end": v(-20, 5.15) * mm});
            skLineSegment(sketch, "E8.9.9.1", {"start": v(-22, 7.15) * mm, "end": v(-22, 5.15) * mm});
            skLineSegment(sketch, "E8.9.9.2", {"start": v(-22, 5.15) * mm, "end": v(-20, 5.15) * mm});
            skLineSegment(sketch, "E8.9.9.3", {"start": v(-22, 7.15) * mm, "end": v(-20, 7.15) * mm});
            skLineSegment(sketch, "E8.9.10.0", {"start": v(-20, 3.15) * mm, "end": v(-20, 1.15) * mm});
            skLineSegment(sketch, "E8.9.10.1", {"start": v(-22, 3.15) * mm, "end": v(-22, 1.15) * mm});
            skLineSegment(sketch, "E8.9.10.2", {"start": v(-22, 1.15) * mm, "end": v(-20, 1.15) * mm});
            skLineSegment(sketch, "E8.9.10.3", {"start": v(-22, 3.15) * mm, "end": v(-20, 3.15) * mm});
            skLineSegment(sketch, "E8.9.11.0", {"start": v(-20, -0.85) * mm, "end": v(-20, -2.85) * mm});
            skLineSegment(sketch, "E8.9.11.1", {"start": v(-22, -0.85) * mm, "end": v(-22, -2.85) * mm});
            skLineSegment(sketch, "E8.9.11.2", {"start": v(-22, -2.85) * mm, "end": v(-20, -2.85) * mm});
            skLineSegment(sketch, "E8.9.11.3", {"start": v(-22, -0.85) * mm, "end": v(-20, -0.85) * mm});
            skLineSegment(sketch, "E8.9.12.0", {"start": v(-20, -4.85) * mm, "end": v(-20, -6.85) * mm});
            skLineSegment(sketch, "E8.9.12.1", {"start": v(-22, -4.85) * mm, "end": v(-22, -6.85) * mm});
            skLineSegment(sketch, "E8.9.12.2", {"start": v(-22, -6.85) * mm, "end": v(-20, -6.85) * mm});
            skLineSegment(sketch, "E8.9.12.3", {"start": v(-22, -4.85) * mm, "end": v(-20, -4.85) * mm});
            skLineSegment(sketch, "E8.9.13.0", {"start": v(-20, -8.85) * mm, "end": v(-20, -10.85) * mm});
            skLineSegment(sketch, "E8.9.13.1", {"start": v(-22, -8.85) * mm, "end": v(-22, -10.85) * mm});
            skLineSegment(sketch, "E8.9.13.2", {"start": v(-22, -10.85) * mm, "end": v(-20, -10.85) * mm});
            skLineSegment(sketch, "E8.9.13.3", {"start": v(-22, -8.85) * mm, "end": v(-20, -8.85) * mm});
            skLineSegment(sketch, "E8.9.14.0", {"start": v(-20, -12.85) * mm, "end": v(-20, -14.85) * mm});
            skLineSegment(sketch, "E8.9.14.1", {"start": v(-22, -12.85) * mm, "end": v(-22, -14.85) * mm});
            skLineSegment(sketch, "E8.9.14.2", {"start": v(-22, -14.85) * mm, "end": v(-20, -14.85) * mm});
            skLineSegment(sketch, "E8.9.14.3", {"start": v(-22, -12.85) * mm, "end": v(-20, -12.85) * mm});
            skLineSegment(sketch, "E8.9.15.0", {"start": v(-20, -16.85) * mm, "end": v(-20, -18.85) * mm});
            skLineSegment(sketch, "E8.9.15.1", {"start": v(-22, -16.85) * mm, "end": v(-22, -18.85) * mm});
            skLineSegment(sketch, "E8.9.15.2", {"start": v(-22, -18.85) * mm, "end": v(-20, -18.85) * mm});
            skLineSegment(sketch, "E8.9.15.3", {"start": v(-22, -16.85) * mm, "end": v(-20, -16.85) * mm});
            skLineSegment(sketch, "E8.9.16.0", {"start": v(-20, -20.85) * mm, "end": v(-20, -22.85) * mm});
            skLineSegment(sketch, "E8.9.16.1", {"start": v(-22, -20.85) * mm, "end": v(-22, -22.85) * mm});
            skLineSegment(sketch, "E8.9.16.2", {"start": v(-22, -22.85) * mm, "end": v(-20, -22.85) * mm});
            skLineSegment(sketch, "E8.9.16.3", {"start": v(-22, -20.85) * mm, "end": v(-20, -20.85) * mm});
            skLineSegment(sketch, "E8.9.17.0", {"start": v(-20, -24.85) * mm, "end": v(-20, -26.85) * mm});
            skLineSegment(sketch, "E8.9.17.1", {"start": v(-22, -24.85) * mm, "end": v(-22, -26.85) * mm});
            skLineSegment(sketch, "E8.9.17.2", {"start": v(-22, -26.85) * mm, "end": v(-20, -26.85) * mm});
            skLineSegment(sketch, "E8.9.17.3", {"start": v(-22, -24.85) * mm, "end": v(-20, -24.85) * mm});
            skLineSegment(sketch, "E8.9.18.0", {"start": v(-20, -28.85) * mm, "end": v(-20, -30.85) * mm});
            skLineSegment(sketch, "E8.9.18.1", {"start": v(-22, -28.85) * mm, "end": v(-22, -30.85) * mm});
            skLineSegment(sketch, "E8.9.18.2", {"start": v(-22, -30.85) * mm, "end": v(-20, -30.85) * mm});
            skLineSegment(sketch, "E8.9.18.3", {"start": v(-22, -28.85) * mm, "end": v(-20, -28.85) * mm});
            skLineSegment(sketch, "E8.9.19.0", {"start": v(-20, -32.85) * mm, "end": v(-20, -34.85) * mm});
            skLineSegment(sketch, "E8.9.19.1", {"start": v(-22, -32.85) * mm, "end": v(-22, -34.85) * mm});
            skLineSegment(sketch, "E8.9.19.2", {"start": v(-22, -34.85) * mm, "end": v(-20, -34.85) * mm});
            skLineSegment(sketch, "E8.9.19.3", {"start": v(-22, -32.85) * mm, "end": v(-20, -32.85) * mm});
            skLineSegment(sketch, "E8.9.20.0", {"start": v(-20, -36.85) * mm, "end": v(-20, -38.85) * mm});
            skLineSegment(sketch, "E8.9.20.1", {"start": v(-22, -36.85) * mm, "end": v(-22, -38.85) * mm});
            skLineSegment(sketch, "E8.9.20.2", {"start": v(-22, -38.85) * mm, "end": v(-20, -38.85) * mm});
            skLineSegment(sketch, "E8.9.20.3", {"start": v(-22, -36.85) * mm, "end": v(-20, -36.85) * mm});
            skLineSegment(sketch, "E8.9.21.0", {"start": v(-20, -40.85) * mm, "end": v(-20, -42.85) * mm});
            skLineSegment(sketch, "E8.9.21.1", {"start": v(-22, -40.85) * mm, "end": v(-22, -42.85) * mm});
            skLineSegment(sketch, "E8.9.21.2", {"start": v(-22, -42.85) * mm, "end": v(-20, -42.85) * mm});
            skLineSegment(sketch, "E8.9.21.3", {"start": v(-22, -40.85) * mm, "end": v(-20, -40.85) * mm});
            skLineSegment(sketch, "E8.10.0.0", {"start": v(-16, 43.15) * mm, "end": v(-16, 41.15) * mm});
            skLineSegment(sketch, "E8.10.0.1", {"start": v(-18, 43.15) * mm, "end": v(-18, 41.15) * mm});
            skLineSegment(sketch, "E8.10.0.2", {"start": v(-18, 41.15) * mm, "end": v(-16, 41.15) * mm});
            skLineSegment(sketch, "E8.10.0.3", {"start": v(-18, 43.15) * mm, "end": v(-16, 43.15) * mm});
            skLineSegment(sketch, "E8.10.1.0", {"start": v(-16, 39.15) * mm, "end": v(-16, 37.15) * mm});
            skLineSegment(sketch, "E8.10.1.1", {"start": v(-18, 39.15) * mm, "end": v(-18, 37.15) * mm});
            skLineSegment(sketch, "E8.10.1.2", {"start": v(-18, 37.15) * mm, "end": v(-16, 37.15) * mm});
            skLineSegment(sketch, "E8.10.1.3", {"start": v(-18, 39.15) * mm, "end": v(-16, 39.15) * mm});
            skLineSegment(sketch, "E8.10.2.0", {"start": v(-16, 35.15) * mm, "end": v(-16, 33.15) * mm});
            skLineSegment(sketch, "E8.10.2.1", {"start": v(-18, 35.15) * mm, "end": v(-18, 33.15) * mm});
            skLineSegment(sketch, "E8.10.2.2", {"start": v(-18, 33.15) * mm, "end": v(-16, 33.15) * mm});
            skLineSegment(sketch, "E8.10.2.3", {"start": v(-18, 35.15) * mm, "end": v(-16, 35.15) * mm});
            skLineSegment(sketch, "E8.10.3.0", {"start": v(-16, 31.15) * mm, "end": v(-16, 29.15) * mm});
            skLineSegment(sketch, "E8.10.3.1", {"start": v(-18, 31.15) * mm, "end": v(-18, 29.15) * mm});
            skLineSegment(sketch, "E8.10.3.2", {"start": v(-18, 29.15) * mm, "end": v(-16, 29.15) * mm});
            skLineSegment(sketch, "E8.10.3.3", {"start": v(-18, 31.15) * mm, "end": v(-16, 31.15) * mm});
            skLineSegment(sketch, "E8.10.4.0", {"start": v(-16, 27.15) * mm, "end": v(-16, 25.15) * mm});
            skLineSegment(sketch, "E8.10.4.1", {"start": v(-18, 27.15) * mm, "end": v(-18, 25.15) * mm});
            skLineSegment(sketch, "E8.10.4.2", {"start": v(-18, 25.15) * mm, "end": v(-16, 25.15) * mm});
            skLineSegment(sketch, "E8.10.4.3", {"start": v(-18, 27.15) * mm, "end": v(-16, 27.15) * mm});
            skLineSegment(sketch, "E8.10.5.0", {"start": v(-16, 23.15) * mm, "end": v(-16, 21.15) * mm});
            skLineSegment(sketch, "E8.10.5.1", {"start": v(-18, 23.15) * mm, "end": v(-18, 21.15) * mm});
            skLineSegment(sketch, "E8.10.5.2", {"start": v(-18, 21.15) * mm, "end": v(-16, 21.15) * mm});
            skLineSegment(sketch, "E8.10.5.3", {"start": v(-18, 23.15) * mm, "end": v(-16, 23.15) * mm});
            skLineSegment(sketch, "E8.10.6.0", {"start": v(-16, 19.15) * mm, "end": v(-16, 17.15) * mm});
            skLineSegment(sketch, "E8.10.6.1", {"start": v(-18, 19.15) * mm, "end": v(-18, 17.15) * mm});
            skLineSegment(sketch, "E8.10.6.2", {"start": v(-18, 17.15) * mm, "end": v(-16, 17.15) * mm});
            skLineSegment(sketch, "E8.10.6.3", {"start": v(-18, 19.15) * mm, "end": v(-16, 19.15) * mm});
            skLineSegment(sketch, "E8.10.7.0", {"start": v(-16, 15.15) * mm, "end": v(-16, 13.15) * mm});
            skLineSegment(sketch, "E8.10.7.1", {"start": v(-18, 15.15) * mm, "end": v(-18, 13.15) * mm});
            skLineSegment(sketch, "E8.10.7.2", {"start": v(-18, 13.15) * mm, "end": v(-16, 13.15) * mm});
            skLineSegment(sketch, "E8.10.7.3", {"start": v(-18, 15.15) * mm, "end": v(-16, 15.15) * mm});
            skLineSegment(sketch, "E8.10.8.0", {"start": v(-16, 11.15) * mm, "end": v(-16, 9.15) * mm});
            skLineSegment(sketch, "E8.10.8.1", {"start": v(-18, 11.15) * mm, "end": v(-18, 9.15) * mm});
            skLineSegment(sketch, "E8.10.8.2", {"start": v(-18, 9.15) * mm, "end": v(-16, 9.15) * mm});
            skLineSegment(sketch, "E8.10.8.3", {"start": v(-18, 11.15) * mm, "end": v(-16, 11.15) * mm});
            skLineSegment(sketch, "E8.10.9.0", {"start": v(-16, 7.15) * mm, "end": v(-16, 5.15) * mm});
            skLineSegment(sketch, "E8.10.9.1", {"start": v(-18, 7.15) * mm, "end": v(-18, 5.15) * mm});
            skLineSegment(sketch, "E8.10.9.2", {"start": v(-18, 5.15) * mm, "end": v(-16, 5.15) * mm});
            skLineSegment(sketch, "E8.10.9.3", {"start": v(-18, 7.15) * mm, "end": v(-16, 7.15) * mm});
            skLineSegment(sketch, "E8.10.10.0", {"start": v(-16, 3.15) * mm, "end": v(-16, 1.15) * mm});
            skLineSegment(sketch, "E8.10.10.1", {"start": v(-18, 3.15) * mm, "end": v(-18, 1.15) * mm});
            skLineSegment(sketch, "E8.10.10.2", {"start": v(-18, 1.15) * mm, "end": v(-16, 1.15) * mm});
            skLineSegment(sketch, "E8.10.10.3", {"start": v(-18, 3.15) * mm, "end": v(-16, 3.15) * mm});
            skLineSegment(sketch, "E8.10.11.0", {"start": v(-16, -0.85) * mm, "end": v(-16, -2.85) * mm});
            skLineSegment(sketch, "E8.10.11.1", {"start": v(-18, -0.85) * mm, "end": v(-18, -2.85) * mm});
            skLineSegment(sketch, "E8.10.11.2", {"start": v(-18, -2.85) * mm, "end": v(-16, -2.85) * mm});
            skLineSegment(sketch, "E8.10.11.3", {"start": v(-18, -0.85) * mm, "end": v(-16, -0.85) * mm});
            skLineSegment(sketch, "E8.10.12.0", {"start": v(-16, -4.85) * mm, "end": v(-16, -6.85) * mm});
            skLineSegment(sketch, "E8.10.12.1", {"start": v(-18, -4.85) * mm, "end": v(-18, -6.85) * mm});
            skLineSegment(sketch, "E8.10.12.2", {"start": v(-18, -6.85) * mm, "end": v(-16, -6.85) * mm});
            skLineSegment(sketch, "E8.10.12.3", {"start": v(-18, -4.85) * mm, "end": v(-16, -4.85) * mm});
            skLineSegment(sketch, "E8.10.13.0", {"start": v(-16, -8.85) * mm, "end": v(-16, -10.85) * mm});
            skLineSegment(sketch, "E8.10.13.1", {"start": v(-18, -8.85) * mm, "end": v(-18, -10.85) * mm});
            skLineSegment(sketch, "E8.10.13.2", {"start": v(-18, -10.85) * mm, "end": v(-16, -10.85) * mm});
            skLineSegment(sketch, "E8.10.13.3", {"start": v(-18, -8.85) * mm, "end": v(-16, -8.85) * mm});
            skLineSegment(sketch, "E8.10.14.0", {"start": v(-16, -12.85) * mm, "end": v(-16, -14.85) * mm});
            skLineSegment(sketch, "E8.10.14.1", {"start": v(-18, -12.85) * mm, "end": v(-18, -14.85) * mm});
            skLineSegment(sketch, "E8.10.14.2", {"start": v(-18, -14.85) * mm, "end": v(-16, -14.85) * mm});
            skLineSegment(sketch, "E8.10.14.3", {"start": v(-18, -12.85) * mm, "end": v(-16, -12.85) * mm});
            skLineSegment(sketch, "E8.10.15.0", {"start": v(-16, -16.85) * mm, "end": v(-16, -18.85) * mm});
            skLineSegment(sketch, "E8.10.15.1", {"start": v(-18, -16.85) * mm, "end": v(-18, -18.85) * mm});
            skLineSegment(sketch, "E8.10.15.2", {"start": v(-18, -18.85) * mm, "end": v(-16, -18.85) * mm});
            skLineSegment(sketch, "E8.10.15.3", {"start": v(-18, -16.85) * mm, "end": v(-16, -16.85) * mm});
            skLineSegment(sketch, "E8.10.16.0", {"start": v(-16, -20.85) * mm, "end": v(-16, -22.85) * mm});
            skLineSegment(sketch, "E8.10.16.1", {"start": v(-18, -20.85) * mm, "end": v(-18, -22.85) * mm});
            skLineSegment(sketch, "E8.10.16.2", {"start": v(-18, -22.85) * mm, "end": v(-16, -22.85) * mm});
            skLineSegment(sketch, "E8.10.16.3", {"start": v(-18, -20.85) * mm, "end": v(-16, -20.85) * mm});
            skLineSegment(sketch, "E8.10.17.0", {"start": v(-16, -24.85) * mm, "end": v(-16, -26.85) * mm});
            skLineSegment(sketch, "E8.10.17.1", {"start": v(-18, -24.85) * mm, "end": v(-18, -26.85) * mm});
            skLineSegment(sketch, "E8.10.17.2", {"start": v(-18, -26.85) * mm, "end": v(-16, -26.85) * mm});
            skLineSegment(sketch, "E8.10.17.3", {"start": v(-18, -24.85) * mm, "end": v(-16, -24.85) * mm});
            skLineSegment(sketch, "E8.10.18.0", {"start": v(-16, -28.85) * mm, "end": v(-16, -30.85) * mm});
            skLineSegment(sketch, "E8.10.18.1", {"start": v(-18, -28.85) * mm, "end": v(-18, -30.85) * mm});
            skLineSegment(sketch, "E8.10.18.2", {"start": v(-18, -30.85) * mm, "end": v(-16, -30.85) * mm});
            skLineSegment(sketch, "E8.10.18.3", {"start": v(-18, -28.85) * mm, "end": v(-16, -28.85) * mm});
            skLineSegment(sketch, "E8.10.19.0", {"start": v(-16, -32.85) * mm, "end": v(-16, -34.85) * mm});
            skLineSegment(sketch, "E8.10.19.1", {"start": v(-18, -32.85) * mm, "end": v(-18, -34.85) * mm});
            skLineSegment(sketch, "E8.10.19.2", {"start": v(-18, -34.85) * mm, "end": v(-16, -34.85) * mm});
            skLineSegment(sketch, "E8.10.19.3", {"start": v(-18, -32.85) * mm, "end": v(-16, -32.85) * mm});
            skLineSegment(sketch, "E8.10.20.0", {"start": v(-16, -36.85) * mm, "end": v(-16, -38.85) * mm});
            skLineSegment(sketch, "E8.10.20.1", {"start": v(-18, -36.85) * mm, "end": v(-18, -38.85) * mm});
            skLineSegment(sketch, "E8.10.20.2", {"start": v(-18, -38.85) * mm, "end": v(-16, -38.85) * mm});
            skLineSegment(sketch, "E8.10.20.3", {"start": v(-18, -36.85) * mm, "end": v(-16, -36.85) * mm});
            skLineSegment(sketch, "E8.10.21.0", {"start": v(-16, -40.85) * mm, "end": v(-16, -42.85) * mm});
            skLineSegment(sketch, "E8.10.21.1", {"start": v(-18, -40.85) * mm, "end": v(-18, -42.85) * mm});
            skLineSegment(sketch, "E8.10.21.2", {"start": v(-18, -42.85) * mm, "end": v(-16, -42.85) * mm});
            skLineSegment(sketch, "E8.10.21.3", {"start": v(-18, -40.85) * mm, "end": v(-16, -40.85) * mm});
            skLineSegment(sketch, "E8.11.0.0", {"start": v(-12, 43.15) * mm, "end": v(-12, 41.15) * mm});
            skLineSegment(sketch, "E8.11.0.1", {"start": v(-14, 43.15) * mm, "end": v(-14, 41.15) * mm});
            skLineSegment(sketch, "E8.11.0.2", {"start": v(-14, 41.15) * mm, "end": v(-12, 41.15) * mm});
            skLineSegment(sketch, "E8.11.0.3", {"start": v(-14, 43.15) * mm, "end": v(-12, 43.15) * mm});
            skLineSegment(sketch, "E8.11.1.0", {"start": v(-12, 39.15) * mm, "end": v(-12, 37.15) * mm});
            skLineSegment(sketch, "E8.11.1.1", {"start": v(-14, 39.15) * mm, "end": v(-14, 37.15) * mm});
            skLineSegment(sketch, "E8.11.1.2", {"start": v(-14, 37.15) * mm, "end": v(-12, 37.15) * mm});
            skLineSegment(sketch, "E8.11.1.3", {"start": v(-14, 39.15) * mm, "end": v(-12, 39.15) * mm});
            skLineSegment(sketch, "E8.11.2.0", {"start": v(-12, 35.15) * mm, "end": v(-12, 33.15) * mm});
            skLineSegment(sketch, "E8.11.2.1", {"start": v(-14, 35.15) * mm, "end": v(-14, 33.15) * mm});
            skLineSegment(sketch, "E8.11.2.2", {"start": v(-14, 33.15) * mm, "end": v(-12, 33.15) * mm});
            skLineSegment(sketch, "E8.11.2.3", {"start": v(-14, 35.15) * mm, "end": v(-12, 35.15) * mm});
            skLineSegment(sketch, "E8.11.3.0", {"start": v(-12, 31.15) * mm, "end": v(-12, 29.15) * mm});
            skLineSegment(sketch, "E8.11.3.1", {"start": v(-14, 31.15) * mm, "end": v(-14, 29.15) * mm});
            skLineSegment(sketch, "E8.11.3.2", {"start": v(-14, 29.15) * mm, "end": v(-12, 29.15) * mm});
            skLineSegment(sketch, "E8.11.3.3", {"start": v(-14, 31.15) * mm, "end": v(-12, 31.15) * mm});
            skLineSegment(sketch, "E8.11.4.0", {"start": v(-12, 27.15) * mm, "end": v(-12, 25.15) * mm});
            skLineSegment(sketch, "E8.11.4.1", {"start": v(-14, 27.15) * mm, "end": v(-14, 25.15) * mm});
            skLineSegment(sketch, "E8.11.4.2", {"start": v(-14, 25.15) * mm, "end": v(-12, 25.15) * mm});
            skLineSegment(sketch, "E8.11.4.3", {"start": v(-14, 27.15) * mm, "end": v(-12, 27.15) * mm});
            skLineSegment(sketch, "E8.11.5.0", {"start": v(-12, 23.15) * mm, "end": v(-12, 21.15) * mm});
            skLineSegment(sketch, "E8.11.5.1", {"start": v(-14, 23.15) * mm, "end": v(-14, 21.15) * mm});
            skLineSegment(sketch, "E8.11.5.2", {"start": v(-14, 21.15) * mm, "end": v(-12, 21.15) * mm});
            skLineSegment(sketch, "E8.11.5.3", {"start": v(-14, 23.15) * mm, "end": v(-12, 23.15) * mm});
            skLineSegment(sketch, "E8.11.6.0", {"start": v(-12, 19.15) * mm, "end": v(-12, 17.15) * mm});
            skLineSegment(sketch, "E8.11.6.1", {"start": v(-14, 19.15) * mm, "end": v(-14, 17.15) * mm});
            skLineSegment(sketch, "E8.11.6.2", {"start": v(-14, 17.15) * mm, "end": v(-12, 17.15) * mm});
            skLineSegment(sketch, "E8.11.6.3", {"start": v(-14, 19.15) * mm, "end": v(-12, 19.15) * mm});
            skLineSegment(sketch, "E8.11.7.0", {"start": v(-12, 15.15) * mm, "end": v(-12, 13.15) * mm});
            skLineSegment(sketch, "E8.11.7.1", {"start": v(-14, 15.15) * mm, "end": v(-14, 13.15) * mm});
            skLineSegment(sketch, "E8.11.7.2", {"start": v(-14, 13.15) * mm, "end": v(-12, 13.15) * mm});
            skLineSegment(sketch, "E8.11.7.3", {"start": v(-14, 15.15) * mm, "end": v(-12, 15.15) * mm});
            skLineSegment(sketch, "E8.11.8.0", {"start": v(-12, 11.15) * mm, "end": v(-12, 9.15) * mm});
            skLineSegment(sketch, "E8.11.8.1", {"start": v(-14, 11.15) * mm, "end": v(-14, 9.15) * mm});
            skLineSegment(sketch, "E8.11.8.2", {"start": v(-14, 9.15) * mm, "end": v(-12, 9.15) * mm});
            skLineSegment(sketch, "E8.11.8.3", {"start": v(-14, 11.15) * mm, "end": v(-12, 11.15) * mm});
            skLineSegment(sketch, "E8.11.9.0", {"start": v(-12, 7.15) * mm, "end": v(-12, 5.15) * mm});
            skLineSegment(sketch, "E8.11.9.1", {"start": v(-14, 7.15) * mm, "end": v(-14, 5.15) * mm});
            skLineSegment(sketch, "E8.11.9.2", {"start": v(-14, 5.15) * mm, "end": v(-12, 5.15) * mm});
            skLineSegment(sketch, "E8.11.9.3", {"start": v(-14, 7.15) * mm, "end": v(-12, 7.15) * mm});
            skLineSegment(sketch, "E8.11.10.0", {"start": v(-12, 3.15) * mm, "end": v(-12, 1.15) * mm});
            skLineSegment(sketch, "E8.11.10.1", {"start": v(-14, 3.15) * mm, "end": v(-14, 1.15) * mm});
            skLineSegment(sketch, "E8.11.10.2", {"start": v(-14, 1.15) * mm, "end": v(-12, 1.15) * mm});
            skLineSegment(sketch, "E8.11.10.3", {"start": v(-14, 3.15) * mm, "end": v(-12, 3.15) * mm});
            skLineSegment(sketch, "E8.11.11.0", {"start": v(-12, -0.85) * mm, "end": v(-12, -2.85) * mm});
            skLineSegment(sketch, "E8.11.11.1", {"start": v(-14, -0.85) * mm, "end": v(-14, -2.85) * mm});
            skLineSegment(sketch, "E8.11.11.2", {"start": v(-14, -2.85) * mm, "end": v(-12, -2.85) * mm});
            skLineSegment(sketch, "E8.11.11.3", {"start": v(-14, -0.85) * mm, "end": v(-12, -0.85) * mm});
            skLineSegment(sketch, "E8.11.12.0", {"start": v(-12, -4.85) * mm, "end": v(-12, -6.85) * mm});
            skLineSegment(sketch, "E8.11.12.1", {"start": v(-14, -4.85) * mm, "end": v(-14, -6.85) * mm});
            skLineSegment(sketch, "E8.11.12.2", {"start": v(-14, -6.85) * mm, "end": v(-12, -6.85) * mm});
            skLineSegment(sketch, "E8.11.12.3", {"start": v(-14, -4.85) * mm, "end": v(-12, -4.85) * mm});
            skLineSegment(sketch, "E8.11.13.0", {"start": v(-12, -8.85) * mm, "end": v(-12, -10.85) * mm});
            skLineSegment(sketch, "E8.11.13.1", {"start": v(-14, -8.85) * mm, "end": v(-14, -10.85) * mm});
            skLineSegment(sketch, "E8.11.13.2", {"start": v(-14, -10.85) * mm, "end": v(-12, -10.85) * mm});
            skLineSegment(sketch, "E8.11.13.3", {"start": v(-14, -8.85) * mm, "end": v(-12, -8.85) * mm});
            skLineSegment(sketch, "E8.11.14.0", {"start": v(-12, -12.85) * mm, "end": v(-12, -14.85) * mm});
            skLineSegment(sketch, "E8.11.14.1", {"start": v(-14, -12.85) * mm, "end": v(-14, -14.85) * mm});
            skLineSegment(sketch, "E8.11.14.2", {"start": v(-14, -14.85) * mm, "end": v(-12, -14.85) * mm});
            skLineSegment(sketch, "E8.11.14.3", {"start": v(-14, -12.85) * mm, "end": v(-12, -12.85) * mm});
            skLineSegment(sketch, "E8.11.15.0", {"start": v(-12, -16.85) * mm, "end": v(-12, -18.85) * mm});
            skLineSegment(sketch, "E8.11.15.1", {"start": v(-14, -16.85) * mm, "end": v(-14, -18.85) * mm});
            skLineSegment(sketch, "E8.11.15.2", {"start": v(-14, -18.85) * mm, "end": v(-12, -18.85) * mm});
            skLineSegment(sketch, "E8.11.15.3", {"start": v(-14, -16.85) * mm, "end": v(-12, -16.85) * mm});
            skLineSegment(sketch, "E8.11.16.0", {"start": v(-12, -20.85) * mm, "end": v(-12, -22.85) * mm});
            skLineSegment(sketch, "E8.11.16.1", {"start": v(-14, -20.85) * mm, "end": v(-14, -22.85) * mm});
            skLineSegment(sketch, "E8.11.16.2", {"start": v(-14, -22.85) * mm, "end": v(-12, -22.85) * mm});
            skLineSegment(sketch, "E8.11.16.3", {"start": v(-14, -20.85) * mm, "end": v(-12, -20.85) * mm});
            skLineSegment(sketch, "E8.11.17.0", {"start": v(-12, -24.85) * mm, "end": v(-12, -26.85) * mm});
            skLineSegment(sketch, "E8.11.17.1", {"start": v(-14, -24.85) * mm, "end": v(-14, -26.85) * mm});
            skLineSegment(sketch, "E8.11.17.2", {"start": v(-14, -26.85) * mm, "end": v(-12, -26.85) * mm});
            skLineSegment(sketch, "E8.11.17.3", {"start": v(-14, -24.85) * mm, "end": v(-12, -24.85) * mm});
            skLineSegment(sketch, "E8.11.18.0", {"start": v(-12, -28.85) * mm, "end": v(-12, -30.85) * mm});
            skLineSegment(sketch, "E8.11.18.1", {"start": v(-14, -28.85) * mm, "end": v(-14, -30.85) * mm});
            skLineSegment(sketch, "E8.11.18.2", {"start": v(-14, -30.85) * mm, "end": v(-12, -30.85) * mm});
            skLineSegment(sketch, "E8.11.18.3", {"start": v(-14, -28.85) * mm, "end": v(-12, -28.85) * mm});
            skLineSegment(sketch, "E8.11.19.0", {"start": v(-12, -32.85) * mm, "end": v(-12, -34.85) * mm});
            skLineSegment(sketch, "E8.11.19.1", {"start": v(-14, -32.85) * mm, "end": v(-14, -34.85) * mm});
            skLineSegment(sketch, "E8.11.19.2", {"start": v(-14, -34.85) * mm, "end": v(-12, -34.85) * mm});
            skLineSegment(sketch, "E8.11.19.3", {"start": v(-14, -32.85) * mm, "end": v(-12, -32.85) * mm});
            skLineSegment(sketch, "E8.11.20.0", {"start": v(-12, -36.85) * mm, "end": v(-12, -38.85) * mm});
            skLineSegment(sketch, "E8.11.20.1", {"start": v(-14, -36.85) * mm, "end": v(-14, -38.85) * mm});
            skLineSegment(sketch, "E8.11.20.2", {"start": v(-14, -38.85) * mm, "end": v(-12, -38.85) * mm});
            skLineSegment(sketch, "E8.11.20.3", {"start": v(-14, -36.85) * mm, "end": v(-12, -36.85) * mm});
            skLineSegment(sketch, "E8.11.21.0", {"start": v(-12, -40.85) * mm, "end": v(-12, -42.85) * mm});
            skLineSegment(sketch, "E8.11.21.1", {"start": v(-14, -40.85) * mm, "end": v(-14, -42.85) * mm});
            skLineSegment(sketch, "E8.11.21.2", {"start": v(-14, -42.85) * mm, "end": v(-12, -42.85) * mm});
            skLineSegment(sketch, "E8.11.21.3", {"start": v(-14, -40.85) * mm, "end": v(-12, -40.85) * mm});
            skLineSegment(sketch, "E8.12.0.0", {"start": v(-8, 43.15) * mm, "end": v(-8, 41.15) * mm});
            skLineSegment(sketch, "E8.12.0.1", {"start": v(-10, 43.15) * mm, "end": v(-10, 41.15) * mm});
            skLineSegment(sketch, "E8.12.0.2", {"start": v(-10, 41.15) * mm, "end": v(-8, 41.15) * mm});
            skLineSegment(sketch, "E8.12.0.3", {"start": v(-10, 43.15) * mm, "end": v(-8, 43.15) * mm});
            skLineSegment(sketch, "E8.12.1.0", {"start": v(-8, 39.15) * mm, "end": v(-8, 37.15) * mm});
            skLineSegment(sketch, "E8.12.1.1", {"start": v(-10, 39.15) * mm, "end": v(-10, 37.15) * mm});
            skLineSegment(sketch, "E8.12.1.2", {"start": v(-10, 37.15) * mm, "end": v(-8, 37.15) * mm});
            skLineSegment(sketch, "E8.12.1.3", {"start": v(-10, 39.15) * mm, "end": v(-8, 39.15) * mm});
            skLineSegment(sketch, "E8.12.2.0", {"start": v(-8, 35.15) * mm, "end": v(-8, 33.15) * mm});
            skLineSegment(sketch, "E8.12.2.1", {"start": v(-10, 35.15) * mm, "end": v(-10, 33.15) * mm});
            skLineSegment(sketch, "E8.12.2.2", {"start": v(-10, 33.15) * mm, "end": v(-8, 33.15) * mm});
            skLineSegment(sketch, "E8.12.2.3", {"start": v(-10, 35.15) * mm, "end": v(-8, 35.15) * mm});
            skLineSegment(sketch, "E8.12.3.0", {"start": v(-8, 31.15) * mm, "end": v(-8, 29.15) * mm});
            skLineSegment(sketch, "E8.12.3.1", {"start": v(-10, 31.15) * mm, "end": v(-10, 29.15) * mm});
            skLineSegment(sketch, "E8.12.3.2", {"start": v(-10, 29.15) * mm, "end": v(-8, 29.15) * mm});
            skLineSegment(sketch, "E8.12.3.3", {"start": v(-10, 31.15) * mm, "end": v(-8, 31.15) * mm});
            skLineSegment(sketch, "E8.12.4.0", {"start": v(-8, 27.15) * mm, "end": v(-8, 25.15) * mm});
            skLineSegment(sketch, "E8.12.4.1", {"start": v(-10, 27.15) * mm, "end": v(-10, 25.15) * mm});
            skLineSegment(sketch, "E8.12.4.2", {"start": v(-10, 25.15) * mm, "end": v(-8, 25.15) * mm});
            skLineSegment(sketch, "E8.12.4.3", {"start": v(-10, 27.15) * mm, "end": v(-8, 27.15) * mm});
            skLineSegment(sketch, "E8.12.5.0", {"start": v(-8, 23.15) * mm, "end": v(-8, 21.15) * mm});
            skLineSegment(sketch, "E8.12.5.1", {"start": v(-10, 23.15) * mm, "end": v(-10, 21.15) * mm});
            skLineSegment(sketch, "E8.12.5.2", {"start": v(-10, 21.15) * mm, "end": v(-8, 21.15) * mm});
            skLineSegment(sketch, "E8.12.5.3", {"start": v(-10, 23.15) * mm, "end": v(-8, 23.15) * mm});
            skLineSegment(sketch, "E8.12.6.0", {"start": v(-8, 19.15) * mm, "end": v(-8, 17.15) * mm});
            skLineSegment(sketch, "E8.12.6.1", {"start": v(-10, 19.15) * mm, "end": v(-10, 17.15) * mm});
            skLineSegment(sketch, "E8.12.6.2", {"start": v(-10, 17.15) * mm, "end": v(-8, 17.15) * mm});
            skLineSegment(sketch, "E8.12.6.3", {"start": v(-10, 19.15) * mm, "end": v(-8, 19.15) * mm});
            skLineSegment(sketch, "E8.12.7.0", {"start": v(-8, 15.15) * mm, "end": v(-8, 13.15) * mm});
            skLineSegment(sketch, "E8.12.7.1", {"start": v(-10, 15.15) * mm, "end": v(-10, 13.15) * mm});
            skLineSegment(sketch, "E8.12.7.2", {"start": v(-10, 13.15) * mm, "end": v(-8, 13.15) * mm});
            skLineSegment(sketch, "E8.12.7.3", {"start": v(-10, 15.15) * mm, "end": v(-8, 15.15) * mm});
            skLineSegment(sketch, "E8.12.8.0", {"start": v(-8, 11.15) * mm, "end": v(-8, 9.15) * mm});
            skLineSegment(sketch, "E8.12.8.1", {"start": v(-10, 11.15) * mm, "end": v(-10, 9.15) * mm});
            skLineSegment(sketch, "E8.12.8.2", {"start": v(-10, 9.15) * mm, "end": v(-8, 9.15) * mm});
            skLineSegment(sketch, "E8.12.8.3", {"start": v(-10, 11.15) * mm, "end": v(-8, 11.15) * mm});
            skLineSegment(sketch, "E8.12.9.0", {"start": v(-8, 7.15) * mm, "end": v(-8, 5.15) * mm});
            skLineSegment(sketch, "E8.12.9.1", {"start": v(-10, 7.15) * mm, "end": v(-10, 5.15) * mm});
            skLineSegment(sketch, "E8.12.9.2", {"start": v(-10, 5.15) * mm, "end": v(-8, 5.15) * mm});
            skLineSegment(sketch, "E8.12.9.3", {"start": v(-10, 7.15) * mm, "end": v(-8, 7.15) * mm});
            skLineSegment(sketch, "E8.12.10.0", {"start": v(-8, 3.15) * mm, "end": v(-8, 1.15) * mm});
            skLineSegment(sketch, "E8.12.10.1", {"start": v(-10, 3.15) * mm, "end": v(-10, 1.15) * mm});
            skLineSegment(sketch, "E8.12.10.2", {"start": v(-10, 1.15) * mm, "end": v(-8, 1.15) * mm});
            skLineSegment(sketch, "E8.12.10.3", {"start": v(-10, 3.15) * mm, "end": v(-8, 3.15) * mm});
            skLineSegment(sketch, "E8.12.11.0", {"start": v(-8, -0.85) * mm, "end": v(-8, -2.85) * mm});
            skLineSegment(sketch, "E8.12.11.1", {"start": v(-10, -0.85) * mm, "end": v(-10, -2.85) * mm});
            skLineSegment(sketch, "E8.12.11.2", {"start": v(-10, -2.85) * mm, "end": v(-8, -2.85) * mm});
            skLineSegment(sketch, "E8.12.11.3", {"start": v(-10, -0.85) * mm, "end": v(-8, -0.85) * mm});
            skLineSegment(sketch, "E8.12.12.0", {"start": v(-8, -4.85) * mm, "end": v(-8, -6.85) * mm});
            skLineSegment(sketch, "E8.12.12.1", {"start": v(-10, -4.85) * mm, "end": v(-10, -6.85) * mm});
            skLineSegment(sketch, "E8.12.12.2", {"start": v(-10, -6.85) * mm, "end": v(-8, -6.85) * mm});
            skLineSegment(sketch, "E8.12.12.3", {"start": v(-10, -4.85) * mm, "end": v(-8, -4.85) * mm});
            skLineSegment(sketch, "E8.12.13.0", {"start": v(-8, -8.85) * mm, "end": v(-8, -10.85) * mm});
            skLineSegment(sketch, "E8.12.13.1", {"start": v(-10, -8.85) * mm, "end": v(-10, -10.85) * mm});
            skLineSegment(sketch, "E8.12.13.2", {"start": v(-10, -10.85) * mm, "end": v(-8, -10.85) * mm});
            skLineSegment(sketch, "E8.12.13.3", {"start": v(-10, -8.85) * mm, "end": v(-8, -8.85) * mm});
            skLineSegment(sketch, "E8.12.14.0", {"start": v(-8, -12.85) * mm, "end": v(-8, -14.85) * mm});
            skLineSegment(sketch, "E8.12.14.1", {"start": v(-10, -12.85) * mm, "end": v(-10, -14.85) * mm});
            skLineSegment(sketch, "E8.12.14.2", {"start": v(-10, -14.85) * mm, "end": v(-8, -14.85) * mm});
            skLineSegment(sketch, "E8.12.14.3", {"start": v(-10, -12.85) * mm, "end": v(-8, -12.85) * mm});
            skLineSegment(sketch, "E8.12.15.0", {"start": v(-8, -16.85) * mm, "end": v(-8, -18.85) * mm});
            skLineSegment(sketch, "E8.12.15.1", {"start": v(-10, -16.85) * mm, "end": v(-10, -18.85) * mm});
            skLineSegment(sketch, "E8.12.15.2", {"start": v(-10, -18.85) * mm, "end": v(-8, -18.85) * mm});
            skLineSegment(sketch, "E8.12.15.3", {"start": v(-10, -16.85) * mm, "end": v(-8, -16.85) * mm});
            skLineSegment(sketch, "E8.12.16.0", {"start": v(-8, -20.85) * mm, "end": v(-8, -22.85) * mm});
            skLineSegment(sketch, "E8.12.16.1", {"start": v(-10, -20.85) * mm, "end": v(-10, -22.85) * mm});
            skLineSegment(sketch, "E8.12.16.2", {"start": v(-10, -22.85) * mm, "end": v(-8, -22.85) * mm});
            skLineSegment(sketch, "E8.12.16.3", {"start": v(-10, -20.85) * mm, "end": v(-8, -20.85) * mm});
            skLineSegment(sketch, "E8.12.17.0", {"start": v(-8, -24.85) * mm, "end": v(-8, -26.85) * mm});
            skLineSegment(sketch, "E8.12.17.1", {"start": v(-10, -24.85) * mm, "end": v(-10, -26.85) * mm});
            skLineSegment(sketch, "E8.12.17.2", {"start": v(-10, -26.85) * mm, "end": v(-8, -26.85) * mm});
            skLineSegment(sketch, "E8.12.17.3", {"start": v(-10, -24.85) * mm, "end": v(-8, -24.85) * mm});
            skLineSegment(sketch, "E8.12.18.0", {"start": v(-8, -28.85) * mm, "end": v(-8, -30.85) * mm});
            skLineSegment(sketch, "E8.12.18.1", {"start": v(-10, -28.85) * mm, "end": v(-10, -30.85) * mm});
            skLineSegment(sketch, "E8.12.18.2", {"start": v(-10, -30.85) * mm, "end": v(-8, -30.85) * mm});
            skLineSegment(sketch, "E8.12.18.3", {"start": v(-10, -28.85) * mm, "end": v(-8, -28.85) * mm});
            skLineSegment(sketch, "E8.12.19.0", {"start": v(-8, -32.85) * mm, "end": v(-8, -34.85) * mm});
            skLineSegment(sketch, "E8.12.19.1", {"start": v(-10, -32.85) * mm, "end": v(-10, -34.85) * mm});
            skLineSegment(sketch, "E8.12.19.2", {"start": v(-10, -34.85) * mm, "end": v(-8, -34.85) * mm});
            skLineSegment(sketch, "E8.12.19.3", {"start": v(-10, -32.85) * mm, "end": v(-8, -32.85) * mm});
            skLineSegment(sketch, "E8.12.20.0", {"start": v(-8, -36.85) * mm, "end": v(-8, -38.85) * mm});
            skLineSegment(sketch, "E8.12.20.1", {"start": v(-10, -36.85) * mm, "end": v(-10, -38.85) * mm});
            skLineSegment(sketch, "E8.12.20.2", {"start": v(-10, -38.85) * mm, "end": v(-8, -38.85) * mm});
            skLineSegment(sketch, "E8.12.20.3", {"start": v(-10, -36.85) * mm, "end": v(-8, -36.85) * mm});
            skLineSegment(sketch, "E8.12.21.0", {"start": v(-8, -40.85) * mm, "end": v(-8, -42.85) * mm});
            skLineSegment(sketch, "E8.12.21.1", {"start": v(-10, -40.85) * mm, "end": v(-10, -42.85) * mm});
            skLineSegment(sketch, "E8.12.21.2", {"start": v(-10, -42.85) * mm, "end": v(-8, -42.85) * mm});
            skLineSegment(sketch, "E8.12.21.3", {"start": v(-10, -40.85) * mm, "end": v(-8, -40.85) * mm});
            skLineSegment(sketch, "E8.13.0.0", {"start": v(-4, 43.15) * mm, "end": v(-4, 41.15) * mm});
            skLineSegment(sketch, "E8.13.0.1", {"start": v(-6, 43.15) * mm, "end": v(-6, 41.15) * mm});
            skLineSegment(sketch, "E8.13.0.2", {"start": v(-6, 41.15) * mm, "end": v(-4, 41.15) * mm});
            skLineSegment(sketch, "E8.13.0.3", {"start": v(-6, 43.15) * mm, "end": v(-4, 43.15) * mm});
            skLineSegment(sketch, "E8.13.1.0", {"start": v(-4, 39.15) * mm, "end": v(-4, 37.15) * mm});
            skLineSegment(sketch, "E8.13.1.1", {"start": v(-6, 39.15) * mm, "end": v(-6, 37.15) * mm});
            skLineSegment(sketch, "E8.13.1.2", {"start": v(-6, 37.15) * mm, "end": v(-4, 37.15) * mm});
            skLineSegment(sketch, "E8.13.1.3", {"start": v(-6, 39.15) * mm, "end": v(-4, 39.15) * mm});
            skLineSegment(sketch, "E8.13.2.0", {"start": v(-4, 35.15) * mm, "end": v(-4, 33.15) * mm});
            skLineSegment(sketch, "E8.13.2.1", {"start": v(-6, 35.15) * mm, "end": v(-6, 33.15) * mm});
            skLineSegment(sketch, "E8.13.2.2", {"start": v(-6, 33.15) * mm, "end": v(-4, 33.15) * mm});
            skLineSegment(sketch, "E8.13.2.3", {"start": v(-6, 35.15) * mm, "end": v(-4, 35.15) * mm});
            skLineSegment(sketch, "E8.13.3.0", {"start": v(-4, 31.15) * mm, "end": v(-4, 29.15) * mm});
            skLineSegment(sketch, "E8.13.3.1", {"start": v(-6, 31.15) * mm, "end": v(-6, 29.15) * mm});
            skLineSegment(sketch, "E8.13.3.2", {"start": v(-6, 29.15) * mm, "end": v(-4, 29.15) * mm});
            skLineSegment(sketch, "E8.13.3.3", {"start": v(-6, 31.15) * mm, "end": v(-4, 31.15) * mm});
            skLineSegment(sketch, "E8.13.4.0", {"start": v(-4, 27.15) * mm, "end": v(-4, 25.15) * mm});
            skLineSegment(sketch, "E8.13.4.1", {"start": v(-6, 27.15) * mm, "end": v(-6, 25.15) * mm});
            skLineSegment(sketch, "E8.13.4.2", {"start": v(-6, 25.15) * mm, "end": v(-4, 25.15) * mm});
            skLineSegment(sketch, "E8.13.4.3", {"start": v(-6, 27.15) * mm, "end": v(-4, 27.15) * mm});
            skLineSegment(sketch, "E8.13.5.0", {"start": v(-4, 23.15) * mm, "end": v(-4, 21.15) * mm});
            skLineSegment(sketch, "E8.13.5.1", {"start": v(-6, 23.15) * mm, "end": v(-6, 21.15) * mm});
            skLineSegment(sketch, "E8.13.5.2", {"start": v(-6, 21.15) * mm, "end": v(-4, 21.15) * mm});
            skLineSegment(sketch, "E8.13.5.3", {"start": v(-6, 23.15) * mm, "end": v(-4, 23.15) * mm});
            skLineSegment(sketch, "E8.13.6.0", {"start": v(-4, 19.15) * mm, "end": v(-4, 17.15) * mm});
            skLineSegment(sketch, "E8.13.6.1", {"start": v(-6, 19.15) * mm, "end": v(-6, 17.15) * mm});
            skLineSegment(sketch, "E8.13.6.2", {"start": v(-6, 17.15) * mm, "end": v(-4, 17.15) * mm});
            skLineSegment(sketch, "E8.13.6.3", {"start": v(-6, 19.15) * mm, "end": v(-4, 19.15) * mm});
            skLineSegment(sketch, "E8.13.7.0", {"start": v(-4, 15.15) * mm, "end": v(-4, 13.15) * mm});
            skLineSegment(sketch, "E8.13.7.1", {"start": v(-6, 15.15) * mm, "end": v(-6, 13.15) * mm});
            skLineSegment(sketch, "E8.13.7.2", {"start": v(-6, 13.15) * mm, "end": v(-4, 13.15) * mm});
            skLineSegment(sketch, "E8.13.7.3", {"start": v(-6, 15.15) * mm, "end": v(-4, 15.15) * mm});
            skLineSegment(sketch, "E8.13.8.0", {"start": v(-4, 11.15) * mm, "end": v(-4, 9.15) * mm});
            skLineSegment(sketch, "E8.13.8.1", {"start": v(-6, 11.15) * mm, "end": v(-6, 9.15) * mm});
            skLineSegment(sketch, "E8.13.8.2", {"start": v(-6, 9.15) * mm, "end": v(-4, 9.15) * mm});
            skLineSegment(sketch, "E8.13.8.3", {"start": v(-6, 11.15) * mm, "end": v(-4, 11.15) * mm});
            skLineSegment(sketch, "E8.13.9.0", {"start": v(-4, 7.15) * mm, "end": v(-4, 5.15) * mm});
            skLineSegment(sketch, "E8.13.9.1", {"start": v(-6, 7.15) * mm, "end": v(-6, 5.15) * mm});
            skLineSegment(sketch, "E8.13.9.2", {"start": v(-6, 5.15) * mm, "end": v(-4, 5.15) * mm});
            skLineSegment(sketch, "E8.13.9.3", {"start": v(-6, 7.15) * mm, "end": v(-4, 7.15) * mm});
            skLineSegment(sketch, "E8.13.10.0", {"start": v(-4, 3.15) * mm, "end": v(-4, 1.15) * mm});
            skLineSegment(sketch, "E8.13.10.1", {"start": v(-6, 3.15) * mm, "end": v(-6, 1.15) * mm});
            skLineSegment(sketch, "E8.13.10.2", {"start": v(-6, 1.15) * mm, "end": v(-4, 1.15) * mm});
            skLineSegment(sketch, "E8.13.10.3", {"start": v(-6, 3.15) * mm, "end": v(-4, 3.15) * mm});
            skLineSegment(sketch, "E8.13.11.0", {"start": v(-4, -0.85) * mm, "end": v(-4, -2.85) * mm});
            skLineSegment(sketch, "E8.13.11.1", {"start": v(-6, -0.85) * mm, "end": v(-6, -2.85) * mm});
            skLineSegment(sketch, "E8.13.11.2", {"start": v(-6, -2.85) * mm, "end": v(-4, -2.85) * mm});
            skLineSegment(sketch, "E8.13.11.3", {"start": v(-6, -0.85) * mm, "end": v(-4, -0.85) * mm});
            skLineSegment(sketch, "E8.13.12.0", {"start": v(-4, -4.85) * mm, "end": v(-4, -6.85) * mm});
            skLineSegment(sketch, "E8.13.12.1", {"start": v(-6, -4.85) * mm, "end": v(-6, -6.85) * mm});
            skLineSegment(sketch, "E8.13.12.2", {"start": v(-6, -6.85) * mm, "end": v(-4, -6.85) * mm});
            skLineSegment(sketch, "E8.13.12.3", {"start": v(-6, -4.85) * mm, "end": v(-4, -4.85) * mm});
            skLineSegment(sketch, "E8.13.13.0", {"start": v(-4, -8.85) * mm, "end": v(-4, -10.85) * mm});
            skLineSegment(sketch, "E8.13.13.1", {"start": v(-6, -8.85) * mm, "end": v(-6, -10.85) * mm});
            skLineSegment(sketch, "E8.13.13.2", {"start": v(-6, -10.85) * mm, "end": v(-4, -10.85) * mm});
            skLineSegment(sketch, "E8.13.13.3", {"start": v(-6, -8.85) * mm, "end": v(-4, -8.85) * mm});
            skLineSegment(sketch, "E8.13.14.0", {"start": v(-4, -12.85) * mm, "end": v(-4, -14.85) * mm});
            skLineSegment(sketch, "E8.13.14.1", {"start": v(-6, -12.85) * mm, "end": v(-6, -14.85) * mm});
            skLineSegment(sketch, "E8.13.14.2", {"start": v(-6, -14.85) * mm, "end": v(-4, -14.85) * mm});
            skLineSegment(sketch, "E8.13.14.3", {"start": v(-6, -12.85) * mm, "end": v(-4, -12.85) * mm});
            skLineSegment(sketch, "E8.13.15.0", {"start": v(-4, -16.85) * mm, "end": v(-4, -18.85) * mm});
            skLineSegment(sketch, "E8.13.15.1", {"start": v(-6, -16.85) * mm, "end": v(-6, -18.85) * mm});
            skLineSegment(sketch, "E8.13.15.2", {"start": v(-6, -18.85) * mm, "end": v(-4, -18.85) * mm});
            skLineSegment(sketch, "E8.13.15.3", {"start": v(-6, -16.85) * mm, "end": v(-4, -16.85) * mm});
            skLineSegment(sketch, "E8.13.16.0", {"start": v(-4, -20.85) * mm, "end": v(-4, -22.85) * mm});
            skLineSegment(sketch, "E8.13.16.1", {"start": v(-6, -20.85) * mm, "end": v(-6, -22.85) * mm});
            skLineSegment(sketch, "E8.13.16.2", {"start": v(-6, -22.85) * mm, "end": v(-4, -22.85) * mm});
            skLineSegment(sketch, "E8.13.16.3", {"start": v(-6, -20.85) * mm, "end": v(-4, -20.85) * mm});
            skLineSegment(sketch, "E8.13.17.0", {"start": v(-4, -24.85) * mm, "end": v(-4, -26.85) * mm});
            skLineSegment(sketch, "E8.13.17.1", {"start": v(-6, -24.85) * mm, "end": v(-6, -26.85) * mm});
            skLineSegment(sketch, "E8.13.17.2", {"start": v(-6, -26.85) * mm, "end": v(-4, -26.85) * mm});
            skLineSegment(sketch, "E8.13.17.3", {"start": v(-6, -24.85) * mm, "end": v(-4, -24.85) * mm});
            skLineSegment(sketch, "E8.13.18.0", {"start": v(-4, -28.85) * mm, "end": v(-4, -30.85) * mm});
            skLineSegment(sketch, "E8.13.18.1", {"start": v(-6, -28.85) * mm, "end": v(-6, -30.85) * mm});
            skLineSegment(sketch, "E8.13.18.2", {"start": v(-6, -30.85) * mm, "end": v(-4, -30.85) * mm});
            skLineSegment(sketch, "E8.13.18.3", {"start": v(-6, -28.85) * mm, "end": v(-4, -28.85) * mm});
            skLineSegment(sketch, "E8.13.19.0", {"start": v(-4, -32.85) * mm, "end": v(-4, -34.85) * mm});
            skLineSegment(sketch, "E8.13.19.1", {"start": v(-6, -32.85) * mm, "end": v(-6, -34.85) * mm});
            skLineSegment(sketch, "E8.13.19.2", {"start": v(-6, -34.85) * mm, "end": v(-4, -34.85) * mm});
            skLineSegment(sketch, "E8.13.19.3", {"start": v(-6, -32.85) * mm, "end": v(-4, -32.85) * mm});
            skLineSegment(sketch, "E8.13.20.0", {"start": v(-4, -36.85) * mm, "end": v(-4, -38.85) * mm});
            skLineSegment(sketch, "E8.13.20.1", {"start": v(-6, -36.85) * mm, "end": v(-6, -38.85) * mm});
            skLineSegment(sketch, "E8.13.20.2", {"start": v(-6, -38.85) * mm, "end": v(-4, -38.85) * mm});
            skLineSegment(sketch, "E8.13.20.3", {"start": v(-6, -36.85) * mm, "end": v(-4, -36.85) * mm});
            skLineSegment(sketch, "E8.13.21.0", {"start": v(-4, -40.85) * mm, "end": v(-4, -42.85) * mm});
            skLineSegment(sketch, "E8.13.21.1", {"start": v(-6, -40.85) * mm, "end": v(-6, -42.85) * mm});
            skLineSegment(sketch, "E8.13.21.2", {"start": v(-6, -42.85) * mm, "end": v(-4, -42.85) * mm});
            skLineSegment(sketch, "E8.13.21.3", {"start": v(-6, -40.85) * mm, "end": v(-4, -40.85) * mm});
            skLineSegment(sketch, "E8.14.0.0", {"start": v(0, 43.15) * mm, "end": v(0, 41.15) * mm});
            skLineSegment(sketch, "E8.14.0.1", {"start": v(-2, 43.15) * mm, "end": v(-2, 41.15) * mm});
            skLineSegment(sketch, "E8.14.0.2", {"start": v(-2, 41.15) * mm, "end": v(0, 41.15) * mm});
            skLineSegment(sketch, "E8.14.0.3", {"start": v(-2, 43.15) * mm, "end": v(0, 43.15) * mm});
            skLineSegment(sketch, "E8.14.1.0", {"start": v(0, 39.15) * mm, "end": v(0, 37.15) * mm});
            skLineSegment(sketch, "E8.14.1.1", {"start": v(-2, 39.15) * mm, "end": v(-2, 37.15) * mm});
            skLineSegment(sketch, "E8.14.1.2", {"start": v(-2, 37.15) * mm, "end": v(0, 37.15) * mm});
            skLineSegment(sketch, "E8.14.1.3", {"start": v(-2, 39.15) * mm, "end": v(0, 39.15) * mm});
            skLineSegment(sketch, "E8.14.2.0", {"start": v(0, 35.15) * mm, "end": v(0, 33.15) * mm});
            skLineSegment(sketch, "E8.14.2.1", {"start": v(-2, 35.15) * mm, "end": v(-2, 33.15) * mm});
            skLineSegment(sketch, "E8.14.2.2", {"start": v(-2, 33.15) * mm, "end": v(0, 33.15) * mm});
            skLineSegment(sketch, "E8.14.2.3", {"start": v(-2, 35.15) * mm, "end": v(0, 35.15) * mm});
            skLineSegment(sketch, "E8.14.3.0", {"start": v(0, 31.15) * mm, "end": v(0, 29.15) * mm});
            skLineSegment(sketch, "E8.14.3.1", {"start": v(-2, 31.15) * mm, "end": v(-2, 29.15) * mm});
            skLineSegment(sketch, "E8.14.3.2", {"start": v(-2, 29.15) * mm, "end": v(0, 29.15) * mm});
            skLineSegment(sketch, "E8.14.3.3", {"start": v(-2, 31.15) * mm, "end": v(0, 31.15) * mm});
            skLineSegment(sketch, "E8.14.4.0", {"start": v(0, 27.15) * mm, "end": v(0, 25.15) * mm});
            skLineSegment(sketch, "E8.14.4.1", {"start": v(-2, 27.15) * mm, "end": v(-2, 25.15) * mm});
            skLineSegment(sketch, "E8.14.4.2", {"start": v(-2, 25.15) * mm, "end": v(0, 25.15) * mm});
            skLineSegment(sketch, "E8.14.4.3", {"start": v(-2, 27.15) * mm, "end": v(0, 27.15) * mm});
            skLineSegment(sketch, "E8.14.5.0", {"start": v(0, 23.15) * mm, "end": v(0, 21.15) * mm});
            skLineSegment(sketch, "E8.14.5.1", {"start": v(-2, 23.15) * mm, "end": v(-2, 21.15) * mm});
            skLineSegment(sketch, "E8.14.5.2", {"start": v(-2, 21.15) * mm, "end": v(0, 21.15) * mm});
            skLineSegment(sketch, "E8.14.5.3", {"start": v(-2, 23.15) * mm, "end": v(0, 23.15) * mm});
            skLineSegment(sketch, "E8.14.6.0", {"start": v(0, 19.15) * mm, "end": v(0, 17.15) * mm});
            skLineSegment(sketch, "E8.14.6.1", {"start": v(-2, 19.15) * mm, "end": v(-2, 17.15) * mm});
            skLineSegment(sketch, "E8.14.6.2", {"start": v(-2, 17.15) * mm, "end": v(0, 17.15) * mm});
            skLineSegment(sketch, "E8.14.6.3", {"start": v(-2, 19.15) * mm, "end": v(0, 19.15) * mm});
            skLineSegment(sketch, "E8.14.7.0", {"start": v(0, 15.15) * mm, "end": v(0, 13.15) * mm});
            skLineSegment(sketch, "E8.14.7.1", {"start": v(-2, 15.15) * mm, "end": v(-2, 13.15) * mm});
            skLineSegment(sketch, "E8.14.7.2", {"start": v(-2, 13.15) * mm, "end": v(0, 13.15) * mm});
            skLineSegment(sketch, "E8.14.7.3", {"start": v(-2, 15.15) * mm, "end": v(0, 15.15) * mm});
            skLineSegment(sketch, "E8.14.8.0", {"start": v(0, 11.15) * mm, "end": v(0, 9.15) * mm});
            skLineSegment(sketch, "E8.14.8.1", {"start": v(-2, 11.15) * mm, "end": v(-2, 9.15) * mm});
            skLineSegment(sketch, "E8.14.8.2", {"start": v(-2, 9.15) * mm, "end": v(0, 9.15) * mm});
            skLineSegment(sketch, "E8.14.8.3", {"start": v(-2, 11.15) * mm, "end": v(0, 11.15) * mm});
            skLineSegment(sketch, "E8.14.9.0", {"start": v(0, 7.15) * mm, "end": v(0, 5.15) * mm});
            skLineSegment(sketch, "E8.14.9.1", {"start": v(-2, 7.15) * mm, "end": v(-2, 5.15) * mm});
            skLineSegment(sketch, "E8.14.9.2", {"start": v(-2, 5.15) * mm, "end": v(0, 5.15) * mm});
            skLineSegment(sketch, "E8.14.9.3", {"start": v(-2, 7.15) * mm, "end": v(0, 7.15) * mm});
            skLineSegment(sketch, "E8.14.10.0", {"start": v(0, 3.15) * mm, "end": v(0, 1.15) * mm});
            skLineSegment(sketch, "E8.14.10.1", {"start": v(-2, 3.15) * mm, "end": v(-2, 1.15) * mm});
            skLineSegment(sketch, "E8.14.10.2", {"start": v(-2, 1.15) * mm, "end": v(0, 1.15) * mm});
            skLineSegment(sketch, "E8.14.10.3", {"start": v(-2, 3.15) * mm, "end": v(0, 3.15) * mm});
            skLineSegment(sketch, "E8.14.11.0", {"start": v(0, -0.85) * mm, "end": v(0, -2.85) * mm});
            skLineSegment(sketch, "E8.14.11.1", {"start": v(-2, -0.85) * mm, "end": v(-2, -2.85) * mm});
            skLineSegment(sketch, "E8.14.11.2", {"start": v(-2, -2.85) * mm, "end": v(0, -2.85) * mm});
            skLineSegment(sketch, "E8.14.11.3", {"start": v(-2, -0.85) * mm, "end": v(0, -0.85) * mm});
            skLineSegment(sketch, "E8.14.12.0", {"start": v(0, -4.85) * mm, "end": v(0, -6.85) * mm});
            skLineSegment(sketch, "E8.14.12.1", {"start": v(-2, -4.85) * mm, "end": v(-2, -6.85) * mm});
            skLineSegment(sketch, "E8.14.12.2", {"start": v(-2, -6.85) * mm, "end": v(0, -6.85) * mm});
            skLineSegment(sketch, "E8.14.12.3", {"start": v(-2, -4.85) * mm, "end": v(0, -4.85) * mm});
            skLineSegment(sketch, "E8.14.13.0", {"start": v(0, -8.85) * mm, "end": v(0, -10.85) * mm});
            skLineSegment(sketch, "E8.14.13.1", {"start": v(-2, -8.85) * mm, "end": v(-2, -10.85) * mm});
            skLineSegment(sketch, "E8.14.13.2", {"start": v(-2, -10.85) * mm, "end": v(0, -10.85) * mm});
            skLineSegment(sketch, "E8.14.13.3", {"start": v(-2, -8.85) * mm, "end": v(0, -8.85) * mm});
            skLineSegment(sketch, "E8.14.14.0", {"start": v(0, -12.85) * mm, "end": v(0, -14.85) * mm});
            skLineSegment(sketch, "E8.14.14.1", {"start": v(-2, -12.85) * mm, "end": v(-2, -14.85) * mm});
            skLineSegment(sketch, "E8.14.14.2", {"start": v(-2, -14.85) * mm, "end": v(0, -14.85) * mm});
            skLineSegment(sketch, "E8.14.14.3", {"start": v(-2, -12.85) * mm, "end": v(0, -12.85) * mm});
            skLineSegment(sketch, "E8.14.15.0", {"start": v(0, -16.85) * mm, "end": v(0, -18.85) * mm});
            skLineSegment(sketch, "E8.14.15.1", {"start": v(-2, -16.85) * mm, "end": v(-2, -18.85) * mm});
            skLineSegment(sketch, "E8.14.15.2", {"start": v(-2, -18.85) * mm, "end": v(0, -18.85) * mm});
            skLineSegment(sketch, "E8.14.15.3", {"start": v(-2, -16.85) * mm, "end": v(0, -16.85) * mm});
            skLineSegment(sketch, "E8.14.16.0", {"start": v(0, -20.85) * mm, "end": v(0, -22.85) * mm});
            skLineSegment(sketch, "E8.14.16.1", {"start": v(-2, -20.85) * mm, "end": v(-2, -22.85) * mm});
            skLineSegment(sketch, "E8.14.16.2", {"start": v(-2, -22.85) * mm, "end": v(0, -22.85) * mm});
            skLineSegment(sketch, "E8.14.16.3", {"start": v(-2, -20.85) * mm, "end": v(0, -20.85) * mm});
            skLineSegment(sketch, "E8.14.17.0", {"start": v(0, -24.85) * mm, "end": v(0, -26.85) * mm});
            skLineSegment(sketch, "E8.14.17.1", {"start": v(-2, -24.85) * mm, "end": v(-2, -26.85) * mm});
            skLineSegment(sketch, "E8.14.17.2", {"start": v(-2, -26.85) * mm, "end": v(0, -26.85) * mm});
            skLineSegment(sketch, "E8.14.17.3", {"start": v(-2, -24.85) * mm, "end": v(0, -24.85) * mm});
            skLineSegment(sketch, "E8.14.18.0", {"start": v(0, -28.85) * mm, "end": v(0, -30.85) * mm});
            skLineSegment(sketch, "E8.14.18.1", {"start": v(-2, -28.85) * mm, "end": v(-2, -30.85) * mm});
            skLineSegment(sketch, "E8.14.18.2", {"start": v(-2, -30.85) * mm, "end": v(0, -30.85) * mm});
            skLineSegment(sketch, "E8.14.18.3", {"start": v(-2, -28.85) * mm, "end": v(0, -28.85) * mm});
            skLineSegment(sketch, "E8.14.19.0", {"start": v(0, -32.85) * mm, "end": v(0, -34.85) * mm});
            skLineSegment(sketch, "E8.14.19.1", {"start": v(-2, -32.85) * mm, "end": v(-2, -34.85) * mm});
            skLineSegment(sketch, "E8.14.19.2", {"start": v(-2, -34.85) * mm, "end": v(0, -34.85) * mm});
            skLineSegment(sketch, "E8.14.19.3", {"start": v(-2, -32.85) * mm, "end": v(0, -32.85) * mm});
            skLineSegment(sketch, "E8.14.20.0", {"start": v(0, -36.85) * mm, "end": v(0, -38.85) * mm});
            skLineSegment(sketch, "E8.14.20.1", {"start": v(-2, -36.85) * mm, "end": v(-2, -38.85) * mm});
            skLineSegment(sketch, "E8.14.20.2", {"start": v(-2, -38.85) * mm, "end": v(0, -38.85) * mm});
            skLineSegment(sketch, "E8.14.20.3", {"start": v(-2, -36.85) * mm, "end": v(0, -36.85) * mm});
            skLineSegment(sketch, "E8.14.21.0", {"start": v(0, -40.85) * mm, "end": v(0, -42.85) * mm});
            skLineSegment(sketch, "E8.14.21.1", {"start": v(-2, -40.85) * mm, "end": v(-2, -42.85) * mm});
            skLineSegment(sketch, "E8.14.21.2", {"start": v(-2, -42.85) * mm, "end": v(0, -42.85) * mm});
            skLineSegment(sketch, "E8.14.21.3", {"start": v(-2, -40.85) * mm, "end": v(0, -40.85) * mm});
            skLineSegment(sketch, "E8.15.0.0", {"start": v(4, 43.15) * mm, "end": v(4, 41.15) * mm});
            skLineSegment(sketch, "E8.15.0.1", {"start": v(2, 43.15) * mm, "end": v(2, 41.15) * mm});
            skLineSegment(sketch, "E8.15.0.2", {"start": v(2, 41.15) * mm, "end": v(4, 41.15) * mm});
            skLineSegment(sketch, "E8.15.0.3", {"start": v(2, 43.15) * mm, "end": v(4, 43.15) * mm});
            skLineSegment(sketch, "E8.15.1.0", {"start": v(4, 39.15) * mm, "end": v(4, 37.15) * mm});
            skLineSegment(sketch, "E8.15.1.1", {"start": v(2, 39.15) * mm, "end": v(2, 37.15) * mm});
            skLineSegment(sketch, "E8.15.1.2", {"start": v(2, 37.15) * mm, "end": v(4, 37.15) * mm});
            skLineSegment(sketch, "E8.15.1.3", {"start": v(2, 39.15) * mm, "end": v(4, 39.15) * mm});
            skLineSegment(sketch, "E8.15.2.0", {"start": v(4, 35.15) * mm, "end": v(4, 33.15) * mm});
            skLineSegment(sketch, "E8.15.2.1", {"start": v(2, 35.15) * mm, "end": v(2, 33.15) * mm});
            skLineSegment(sketch, "E8.15.2.2", {"start": v(2, 33.15) * mm, "end": v(4, 33.15) * mm});
            skLineSegment(sketch, "E8.15.2.3", {"start": v(2, 35.15) * mm, "end": v(4, 35.15) * mm});
            skLineSegment(sketch, "E8.15.3.0", {"start": v(4, 31.15) * mm, "end": v(4, 29.15) * mm});
            skLineSegment(sketch, "E8.15.3.1", {"start": v(2, 31.15) * mm, "end": v(2, 29.15) * mm});
            skLineSegment(sketch, "E8.15.3.2", {"start": v(2, 29.15) * mm, "end": v(4, 29.15) * mm});
            skLineSegment(sketch, "E8.15.3.3", {"start": v(2, 31.15) * mm, "end": v(4, 31.15) * mm});
            skLineSegment(sketch, "E8.15.4.0", {"start": v(4, 27.15) * mm, "end": v(4, 25.15) * mm});
            skLineSegment(sketch, "E8.15.4.1", {"start": v(2, 27.15) * mm, "end": v(2, 25.15) * mm});
            skLineSegment(sketch, "E8.15.4.2", {"start": v(2, 25.15) * mm, "end": v(4, 25.15) * mm});
            skLineSegment(sketch, "E8.15.4.3", {"start": v(2, 27.15) * mm, "end": v(4, 27.15) * mm});
            skLineSegment(sketch, "E8.15.5.0", {"start": v(4, 23.15) * mm, "end": v(4, 21.15) * mm});
            skLineSegment(sketch, "E8.15.5.1", {"start": v(2, 23.15) * mm, "end": v(2, 21.15) * mm});
            skLineSegment(sketch, "E8.15.5.2", {"start": v(2, 21.15) * mm, "end": v(4, 21.15) * mm});
            skLineSegment(sketch, "E8.15.5.3", {"start": v(2, 23.15) * mm, "end": v(4, 23.15) * mm});
            skLineSegment(sketch, "E8.15.6.0", {"start": v(4, 19.15) * mm, "end": v(4, 17.15) * mm});
            skLineSegment(sketch, "E8.15.6.1", {"start": v(2, 19.15) * mm, "end": v(2, 17.15) * mm});
            skLineSegment(sketch, "E8.15.6.2", {"start": v(2, 17.15) * mm, "end": v(4, 17.15) * mm});
            skLineSegment(sketch, "E8.15.6.3", {"start": v(2, 19.15) * mm, "end": v(4, 19.15) * mm});
            skLineSegment(sketch, "E8.15.7.0", {"start": v(4, 15.15) * mm, "end": v(4, 13.15) * mm});
            skLineSegment(sketch, "E8.15.7.1", {"start": v(2, 15.15) * mm, "end": v(2, 13.15) * mm});
            skLineSegment(sketch, "E8.15.7.2", {"start": v(2, 13.15) * mm, "end": v(4, 13.15) * mm});
            skLineSegment(sketch, "E8.15.7.3", {"start": v(2, 15.15) * mm, "end": v(4, 15.15) * mm});
            skLineSegment(sketch, "E8.15.8.0", {"start": v(4, 11.15) * mm, "end": v(4, 9.15) * mm});
            skLineSegment(sketch, "E8.15.8.1", {"start": v(2, 11.15) * mm, "end": v(2, 9.15) * mm});
            skLineSegment(sketch, "E8.15.8.2", {"start": v(2, 9.15) * mm, "end": v(4, 9.15) * mm});
            skLineSegment(sketch, "E8.15.8.3", {"start": v(2, 11.15) * mm, "end": v(4, 11.15) * mm});
            skLineSegment(sketch, "E8.15.9.0", {"start": v(4, 7.15) * mm, "end": v(4, 5.15) * mm});
            skLineSegment(sketch, "E8.15.9.1", {"start": v(2, 7.15) * mm, "end": v(2, 5.15) * mm});
            skLineSegment(sketch, "E8.15.9.2", {"start": v(2, 5.15) * mm, "end": v(4, 5.15) * mm});
            skLineSegment(sketch, "E8.15.9.3", {"start": v(2, 7.15) * mm, "end": v(4, 7.15) * mm});
            skLineSegment(sketch, "E8.15.10.0", {"start": v(4, 3.15) * mm, "end": v(4, 1.15) * mm});
            skLineSegment(sketch, "E8.15.10.1", {"start": v(2, 3.15) * mm, "end": v(2, 1.15) * mm});
            skLineSegment(sketch, "E8.15.10.2", {"start": v(2, 1.15) * mm, "end": v(4, 1.15) * mm});
            skLineSegment(sketch, "E8.15.10.3", {"start": v(2, 3.15) * mm, "end": v(4, 3.15) * mm});
            skLineSegment(sketch, "E8.15.11.0", {"start": v(4, -0.85) * mm, "end": v(4, -2.85) * mm});
            skLineSegment(sketch, "E8.15.11.1", {"start": v(2, -0.85) * mm, "end": v(2, -2.85) * mm});
            skLineSegment(sketch, "E8.15.11.2", {"start": v(2, -2.85) * mm, "end": v(4, -2.85) * mm});
            skLineSegment(sketch, "E8.15.11.3", {"start": v(2, -0.85) * mm, "end": v(4, -0.85) * mm});
            skLineSegment(sketch, "E8.15.12.0", {"start": v(4, -4.85) * mm, "end": v(4, -6.85) * mm});
            skLineSegment(sketch, "E8.15.12.1", {"start": v(2, -4.85) * mm, "end": v(2, -6.85) * mm});
            skLineSegment(sketch, "E8.15.12.2", {"start": v(2, -6.85) * mm, "end": v(4, -6.85) * mm});
            skLineSegment(sketch, "E8.15.12.3", {"start": v(2, -4.85) * mm, "end": v(4, -4.85) * mm});
            skLineSegment(sketch, "E8.15.13.0", {"start": v(4, -8.85) * mm, "end": v(4, -10.85) * mm});
            skLineSegment(sketch, "E8.15.13.1", {"start": v(2, -8.85) * mm, "end": v(2, -10.85) * mm});
            skLineSegment(sketch, "E8.15.13.2", {"start": v(2, -10.85) * mm, "end": v(4, -10.85) * mm});
            skLineSegment(sketch, "E8.15.13.3", {"start": v(2, -8.85) * mm, "end": v(4, -8.85) * mm});
            skLineSegment(sketch, "E8.15.14.0", {"start": v(4, -12.85) * mm, "end": v(4, -14.85) * mm});
            skLineSegment(sketch, "E8.15.14.1", {"start": v(2, -12.85) * mm, "end": v(2, -14.85) * mm});
            skLineSegment(sketch, "E8.15.14.2", {"start": v(2, -14.85) * mm, "end": v(4, -14.85) * mm});
            skLineSegment(sketch, "E8.15.14.3", {"start": v(2, -12.85) * mm, "end": v(4, -12.85) * mm});
            skLineSegment(sketch, "E8.15.15.0", {"start": v(4, -16.85) * mm, "end": v(4, -18.85) * mm});
            skLineSegment(sketch, "E8.15.15.1", {"start": v(2, -16.85) * mm, "end": v(2, -18.85) * mm});
            skLineSegment(sketch, "E8.15.15.2", {"start": v(2, -18.85) * mm, "end": v(4, -18.85) * mm});
            skLineSegment(sketch, "E8.15.15.3", {"start": v(2, -16.85) * mm, "end": v(4, -16.85) * mm});
            skLineSegment(sketch, "E8.15.16.0", {"start": v(4, -20.85) * mm, "end": v(4, -22.85) * mm});
            skLineSegment(sketch, "E8.15.16.1", {"start": v(2, -20.85) * mm, "end": v(2, -22.85) * mm});
            skLineSegment(sketch, "E8.15.16.2", {"start": v(2, -22.85) * mm, "end": v(4, -22.85) * mm});
            skLineSegment(sketch, "E8.15.16.3", {"start": v(2, -20.85) * mm, "end": v(4, -20.85) * mm});
            skLineSegment(sketch, "E8.15.17.0", {"start": v(4, -24.85) * mm, "end": v(4, -26.85) * mm});
            skLineSegment(sketch, "E8.15.17.1", {"start": v(2, -24.85) * mm, "end": v(2, -26.85) * mm});
            skLineSegment(sketch, "E8.15.17.2", {"start": v(2, -26.85) * mm, "end": v(4, -26.85) * mm});
            skLineSegment(sketch, "E8.15.17.3", {"start": v(2, -24.85) * mm, "end": v(4, -24.85) * mm});
            skLineSegment(sketch, "E8.15.18.0", {"start": v(4, -28.85) * mm, "end": v(4, -30.85) * mm});
            skLineSegment(sketch, "E8.15.18.1", {"start": v(2, -28.85) * mm, "end": v(2, -30.85) * mm});
            skLineSegment(sketch, "E8.15.18.2", {"start": v(2, -30.85) * mm, "end": v(4, -30.85) * mm});
            skLineSegment(sketch, "E8.15.18.3", {"start": v(2, -28.85) * mm, "end": v(4, -28.85) * mm});
            skLineSegment(sketch, "E8.15.19.0", {"start": v(4, -32.85) * mm, "end": v(4, -34.85) * mm});
            skLineSegment(sketch, "E8.15.19.1", {"start": v(2, -32.85) * mm, "end": v(2, -34.85) * mm});
            skLineSegment(sketch, "E8.15.19.2", {"start": v(2, -34.85) * mm, "end": v(4, -34.85) * mm});
            skLineSegment(sketch, "E8.15.19.3", {"start": v(2, -32.85) * mm, "end": v(4, -32.85) * mm});
            skLineSegment(sketch, "E8.15.20.0", {"start": v(4, -36.85) * mm, "end": v(4, -38.85) * mm});
            skLineSegment(sketch, "E8.15.20.1", {"start": v(2, -36.85) * mm, "end": v(2, -38.85) * mm});
            skLineSegment(sketch, "E8.15.20.2", {"start": v(2, -38.85) * mm, "end": v(4, -38.85) * mm});
            skLineSegment(sketch, "E8.15.20.3", {"start": v(2, -36.85) * mm, "end": v(4, -36.85) * mm});
            skLineSegment(sketch, "E8.15.21.0", {"start": v(4, -40.85) * mm, "end": v(4, -42.85) * mm});
            skLineSegment(sketch, "E8.15.21.1", {"start": v(2, -40.85) * mm, "end": v(2, -42.85) * mm});
            skLineSegment(sketch, "E8.15.21.2", {"start": v(2, -42.85) * mm, "end": v(4, -42.85) * mm});
            skLineSegment(sketch, "E8.15.21.3", {"start": v(2, -40.85) * mm, "end": v(4, -40.85) * mm});
            skLineSegment(sketch, "E8.16.0.0", {"start": v(8, 43.15) * mm, "end": v(8, 41.15) * mm});
            skLineSegment(sketch, "E8.16.0.1", {"start": v(6, 43.15) * mm, "end": v(6, 41.15) * mm});
            skLineSegment(sketch, "E8.16.0.2", {"start": v(6, 41.15) * mm, "end": v(8, 41.15) * mm});
            skLineSegment(sketch, "E8.16.0.3", {"start": v(6, 43.15) * mm, "end": v(8, 43.15) * mm});
            skLineSegment(sketch, "E8.16.1.0", {"start": v(8, 39.15) * mm, "end": v(8, 37.15) * mm});
            skLineSegment(sketch, "E8.16.1.1", {"start": v(6, 39.15) * mm, "end": v(6, 37.15) * mm});
            skLineSegment(sketch, "E8.16.1.2", {"start": v(6, 37.15) * mm, "end": v(8, 37.15) * mm});
            skLineSegment(sketch, "E8.16.1.3", {"start": v(6, 39.15) * mm, "end": v(8, 39.15) * mm});
            skLineSegment(sketch, "E8.16.2.0", {"start": v(8, 35.15) * mm, "end": v(8, 33.15) * mm});
            skLineSegment(sketch, "E8.16.2.1", {"start": v(6, 35.15) * mm, "end": v(6, 33.15) * mm});
            skLineSegment(sketch, "E8.16.2.2", {"start": v(6, 33.15) * mm, "end": v(8, 33.15) * mm});
            skLineSegment(sketch, "E8.16.2.3", {"start": v(6, 35.15) * mm, "end": v(8, 35.15) * mm});
            skLineSegment(sketch, "E8.16.3.0", {"start": v(8, 31.15) * mm, "end": v(8, 29.15) * mm});
            skLineSegment(sketch, "E8.16.3.1", {"start": v(6, 31.15) * mm, "end": v(6, 29.15) * mm});
            skLineSegment(sketch, "E8.16.3.2", {"start": v(6, 29.15) * mm, "end": v(8, 29.15) * mm});
            skLineSegment(sketch, "E8.16.3.3", {"start": v(6, 31.15) * mm, "end": v(8, 31.15) * mm});
            skLineSegment(sketch, "E8.16.4.0", {"start": v(8, 27.15) * mm, "end": v(8, 25.15) * mm});
            skLineSegment(sketch, "E8.16.4.1", {"start": v(6, 27.15) * mm, "end": v(6, 25.15) * mm});
            skLineSegment(sketch, "E8.16.4.2", {"start": v(6, 25.15) * mm, "end": v(8, 25.15) * mm});
            skLineSegment(sketch, "E8.16.4.3", {"start": v(6, 27.15) * mm, "end": v(8, 27.15) * mm});
            skLineSegment(sketch, "E8.16.5.0", {"start": v(8, 23.15) * mm, "end": v(8, 21.15) * mm});
            skLineSegment(sketch, "E8.16.5.1", {"start": v(6, 23.15) * mm, "end": v(6, 21.15) * mm});
            skLineSegment(sketch, "E8.16.5.2", {"start": v(6, 21.15) * mm, "end": v(8, 21.15) * mm});
            skLineSegment(sketch, "E8.16.5.3", {"start": v(6, 23.15) * mm, "end": v(8, 23.15) * mm});
            skLineSegment(sketch, "E8.16.6.0", {"start": v(8, 19.15) * mm, "end": v(8, 17.15) * mm});
            skLineSegment(sketch, "E8.16.6.1", {"start": v(6, 19.15) * mm, "end": v(6, 17.15) * mm});
            skLineSegment(sketch, "E8.16.6.2", {"start": v(6, 17.15) * mm, "end": v(8, 17.15) * mm});
            skLineSegment(sketch, "E8.16.6.3", {"start": v(6, 19.15) * mm, "end": v(8, 19.15) * mm});
            skLineSegment(sketch, "E8.16.7.0", {"start": v(8, 15.15) * mm, "end": v(8, 13.15) * mm});
            skLineSegment(sketch, "E8.16.7.1", {"start": v(6, 15.15) * mm, "end": v(6, 13.15) * mm});
            skLineSegment(sketch, "E8.16.7.2", {"start": v(6, 13.15) * mm, "end": v(8, 13.15) * mm});
            skLineSegment(sketch, "E8.16.7.3", {"start": v(6, 15.15) * mm, "end": v(8, 15.15) * mm});
            skLineSegment(sketch, "E8.16.8.0", {"start": v(8, 11.15) * mm, "end": v(8, 9.15) * mm});
            skLineSegment(sketch, "E8.16.8.1", {"start": v(6, 11.15) * mm, "end": v(6, 9.15) * mm});
            skLineSegment(sketch, "E8.16.8.2", {"start": v(6, 9.15) * mm, "end": v(8, 9.15) * mm});
            skLineSegment(sketch, "E8.16.8.3", {"start": v(6, 11.15) * mm, "end": v(8, 11.15) * mm});
            skLineSegment(sketch, "E8.16.9.0", {"start": v(8, 7.15) * mm, "end": v(8, 5.15) * mm});
            skLineSegment(sketch, "E8.16.9.1", {"start": v(6, 7.15) * mm, "end": v(6, 5.15) * mm});
            skLineSegment(sketch, "E8.16.9.2", {"start": v(6, 5.15) * mm, "end": v(8, 5.15) * mm});
            skLineSegment(sketch, "E8.16.9.3", {"start": v(6, 7.15) * mm, "end": v(8, 7.15) * mm});
            skLineSegment(sketch, "E8.16.10.0", {"start": v(8, 3.15) * mm, "end": v(8, 1.15) * mm});
            skLineSegment(sketch, "E8.16.10.1", {"start": v(6, 3.15) * mm, "end": v(6, 1.15) * mm});
            skLineSegment(sketch, "E8.16.10.2", {"start": v(6, 1.15) * mm, "end": v(8, 1.15) * mm});
            skLineSegment(sketch, "E8.16.10.3", {"start": v(6, 3.15) * mm, "end": v(8, 3.15) * mm});
            skLineSegment(sketch, "E8.16.11.0", {"start": v(8, -0.85) * mm, "end": v(8, -2.85) * mm});
            skLineSegment(sketch, "E8.16.11.1", {"start": v(6, -0.85) * mm, "end": v(6, -2.85) * mm});
            skLineSegment(sketch, "E8.16.11.2", {"start": v(6, -2.85) * mm, "end": v(8, -2.85) * mm});
            skLineSegment(sketch, "E8.16.11.3", {"start": v(6, -0.85) * mm, "end": v(8, -0.85) * mm});
            skLineSegment(sketch, "E8.16.12.0", {"start": v(8, -4.85) * mm, "end": v(8, -6.85) * mm});
            skLineSegment(sketch, "E8.16.12.1", {"start": v(6, -4.85) * mm, "end": v(6, -6.85) * mm});
            skLineSegment(sketch, "E8.16.12.2", {"start": v(6, -6.85) * mm, "end": v(8, -6.85) * mm});
            skLineSegment(sketch, "E8.16.12.3", {"start": v(6, -4.85) * mm, "end": v(8, -4.85) * mm});
            skLineSegment(sketch, "E8.16.13.0", {"start": v(8, -8.85) * mm, "end": v(8, -10.85) * mm});
            skLineSegment(sketch, "E8.16.13.1", {"start": v(6, -8.85) * mm, "end": v(6, -10.85) * mm});
            skLineSegment(sketch, "E8.16.13.2", {"start": v(6, -10.85) * mm, "end": v(8, -10.85) * mm});
            skLineSegment(sketch, "E8.16.13.3", {"start": v(6, -8.85) * mm, "end": v(8, -8.85) * mm});
            skLineSegment(sketch, "E8.16.14.0", {"start": v(8, -12.85) * mm, "end": v(8, -14.85) * mm});
            skLineSegment(sketch, "E8.16.14.1", {"start": v(6, -12.85) * mm, "end": v(6, -14.85) * mm});
            skLineSegment(sketch, "E8.16.14.2", {"start": v(6, -14.85) * mm, "end": v(8, -14.85) * mm});
            skLineSegment(sketch, "E8.16.14.3", {"start": v(6, -12.85) * mm, "end": v(8, -12.85) * mm});
            skLineSegment(sketch, "E8.16.15.0", {"start": v(8, -16.85) * mm, "end": v(8, -18.85) * mm});
            skLineSegment(sketch, "E8.16.15.1", {"start": v(6, -16.85) * mm, "end": v(6, -18.85) * mm});
            skLineSegment(sketch, "E8.16.15.2", {"start": v(6, -18.85) * mm, "end": v(8, -18.85) * mm});
            skLineSegment(sketch, "E8.16.15.3", {"start": v(6, -16.85) * mm, "end": v(8, -16.85) * mm});
            skLineSegment(sketch, "E8.16.16.0", {"start": v(8, -20.85) * mm, "end": v(8, -22.85) * mm});
            skLineSegment(sketch, "E8.16.16.1", {"start": v(6, -20.85) * mm, "end": v(6, -22.85) * mm});
            skLineSegment(sketch, "E8.16.16.2", {"start": v(6, -22.85) * mm, "end": v(8, -22.85) * mm});
            skLineSegment(sketch, "E8.16.16.3", {"start": v(6, -20.85) * mm, "end": v(8, -20.85) * mm});
            skLineSegment(sketch, "E8.16.17.0", {"start": v(8, -24.85) * mm, "end": v(8, -26.85) * mm});
            skLineSegment(sketch, "E8.16.17.1", {"start": v(6, -24.85) * mm, "end": v(6, -26.85) * mm});
            skLineSegment(sketch, "E8.16.17.2", {"start": v(6, -26.85) * mm, "end": v(8, -26.85) * mm});
            skLineSegment(sketch, "E8.16.17.3", {"start": v(6, -24.85) * mm, "end": v(8, -24.85) * mm});
            skLineSegment(sketch, "E8.16.18.0", {"start": v(8, -28.85) * mm, "end": v(8, -30.85) * mm});
            skLineSegment(sketch, "E8.16.18.1", {"start": v(6, -28.85) * mm, "end": v(6, -30.85) * mm});
            skLineSegment(sketch, "E8.16.18.2", {"start": v(6, -30.85) * mm, "end": v(8, -30.85) * mm});
            skLineSegment(sketch, "E8.16.18.3", {"start": v(6, -28.85) * mm, "end": v(8, -28.85) * mm});
            skLineSegment(sketch, "E8.16.19.0", {"start": v(8, -32.85) * mm, "end": v(8, -34.85) * mm});
            skLineSegment(sketch, "E8.16.19.1", {"start": v(6, -32.85) * mm, "end": v(6, -34.85) * mm});
            skLineSegment(sketch, "E8.16.19.2", {"start": v(6, -34.85) * mm, "end": v(8, -34.85) * mm});
            skLineSegment(sketch, "E8.16.19.3", {"start": v(6, -32.85) * mm, "end": v(8, -32.85) * mm});
            skLineSegment(sketch, "E8.16.20.0", {"start": v(8, -36.85) * mm, "end": v(8, -38.85) * mm});
            skLineSegment(sketch, "E8.16.20.1", {"start": v(6, -36.85) * mm, "end": v(6, -38.85) * mm});
            skLineSegment(sketch, "E8.16.20.2", {"start": v(6, -38.85) * mm, "end": v(8, -38.85) * mm});
            skLineSegment(sketch, "E8.16.20.3", {"start": v(6, -36.85) * mm, "end": v(8, -36.85) * mm});
            skLineSegment(sketch, "E8.16.21.0", {"start": v(8, -40.85) * mm, "end": v(8, -42.85) * mm});
            skLineSegment(sketch, "E8.16.21.1", {"start": v(6, -40.85) * mm, "end": v(6, -42.85) * mm});
            skLineSegment(sketch, "E8.16.21.2", {"start": v(6, -42.85) * mm, "end": v(8, -42.85) * mm});
            skLineSegment(sketch, "E8.16.21.3", {"start": v(6, -40.85) * mm, "end": v(8, -40.85) * mm});
            skLineSegment(sketch, "E8.17.0.0", {"start": v(12, 43.15) * mm, "end": v(12, 41.15) * mm});
            skLineSegment(sketch, "E8.17.0.1", {"start": v(10, 43.15) * mm, "end": v(10, 41.15) * mm});
            skLineSegment(sketch, "E8.17.0.2", {"start": v(10, 41.15) * mm, "end": v(12, 41.15) * mm});
            skLineSegment(sketch, "E8.17.0.3", {"start": v(10, 43.15) * mm, "end": v(12, 43.15) * mm});
            skLineSegment(sketch, "E8.17.1.0", {"start": v(12, 39.15) * mm, "end": v(12, 37.15) * mm});
            skLineSegment(sketch, "E8.17.1.1", {"start": v(10, 39.15) * mm, "end": v(10, 37.15) * mm});
            skLineSegment(sketch, "E8.17.1.2", {"start": v(10, 37.15) * mm, "end": v(12, 37.15) * mm});
            skLineSegment(sketch, "E8.17.1.3", {"start": v(10, 39.15) * mm, "end": v(12, 39.15) * mm});
            skLineSegment(sketch, "E8.17.2.0", {"start": v(12, 35.15) * mm, "end": v(12, 33.15) * mm});
            skLineSegment(sketch, "E8.17.2.1", {"start": v(10, 35.15) * mm, "end": v(10, 33.15) * mm});
            skLineSegment(sketch, "E8.17.2.2", {"start": v(10, 33.15) * mm, "end": v(12, 33.15) * mm});
            skLineSegment(sketch, "E8.17.2.3", {"start": v(10, 35.15) * mm, "end": v(12, 35.15) * mm});
            skLineSegment(sketch, "E8.17.3.0", {"start": v(12, 31.15) * mm, "end": v(12, 29.15) * mm});
            skLineSegment(sketch, "E8.17.3.1", {"start": v(10, 31.15) * mm, "end": v(10, 29.15) * mm});
            skLineSegment(sketch, "E8.17.3.2", {"start": v(10, 29.15) * mm, "end": v(12, 29.15) * mm});
            skLineSegment(sketch, "E8.17.3.3", {"start": v(10, 31.15) * mm, "end": v(12, 31.15) * mm});
            skLineSegment(sketch, "E8.17.4.0", {"start": v(12, 27.15) * mm, "end": v(12, 25.15) * mm});
            skLineSegment(sketch, "E8.17.4.1", {"start": v(10, 27.15) * mm, "end": v(10, 25.15) * mm});
            skLineSegment(sketch, "E8.17.4.2", {"start": v(10, 25.15) * mm, "end": v(12, 25.15) * mm});
            skLineSegment(sketch, "E8.17.4.3", {"start": v(10, 27.15) * mm, "end": v(12, 27.15) * mm});
            skLineSegment(sketch, "E8.17.5.0", {"start": v(12, 23.15) * mm, "end": v(12, 21.15) * mm});
            skLineSegment(sketch, "E8.17.5.1", {"start": v(10, 23.15) * mm, "end": v(10, 21.15) * mm});
            skLineSegment(sketch, "E8.17.5.2", {"start": v(10, 21.15) * mm, "end": v(12, 21.15) * mm});
            skLineSegment(sketch, "E8.17.5.3", {"start": v(10, 23.15) * mm, "end": v(12, 23.15) * mm});
            skLineSegment(sketch, "E8.17.6.0", {"start": v(12, 19.15) * mm, "end": v(12, 17.15) * mm});
            skLineSegment(sketch, "E8.17.6.1", {"start": v(10, 19.15) * mm, "end": v(10, 17.15) * mm});
            skLineSegment(sketch, "E8.17.6.2", {"start": v(10, 17.15) * mm, "end": v(12, 17.15) * mm});
            skLineSegment(sketch, "E8.17.6.3", {"start": v(10, 19.15) * mm, "end": v(12, 19.15) * mm});
            skLineSegment(sketch, "E8.17.7.0", {"start": v(12, 15.15) * mm, "end": v(12, 13.15) * mm});
            skLineSegment(sketch, "E8.17.7.1", {"start": v(10, 15.15) * mm, "end": v(10, 13.15) * mm});
            skLineSegment(sketch, "E8.17.7.2", {"start": v(10, 13.15) * mm, "end": v(12, 13.15) * mm});
            skLineSegment(sketch, "E8.17.7.3", {"start": v(10, 15.15) * mm, "end": v(12, 15.15) * mm});
            skLineSegment(sketch, "E8.17.8.0", {"start": v(12, 11.15) * mm, "end": v(12, 9.15) * mm});
            skLineSegment(sketch, "E8.17.8.1", {"start": v(10, 11.15) * mm, "end": v(10, 9.15) * mm});
            skLineSegment(sketch, "E8.17.8.2", {"start": v(10, 9.15) * mm, "end": v(12, 9.15) * mm});
            skLineSegment(sketch, "E8.17.8.3", {"start": v(10, 11.15) * mm, "end": v(12, 11.15) * mm});
            skLineSegment(sketch, "E8.17.9.0", {"start": v(12, 7.15) * mm, "end": v(12, 5.15) * mm});
            skLineSegment(sketch, "E8.17.9.1", {"start": v(10, 7.15) * mm, "end": v(10, 5.15) * mm});
            skLineSegment(sketch, "E8.17.9.2", {"start": v(10, 5.15) * mm, "end": v(12, 5.15) * mm});
            skLineSegment(sketch, "E8.17.9.3", {"start": v(10, 7.15) * mm, "end": v(12, 7.15) * mm});
            skLineSegment(sketch, "E8.17.10.0", {"start": v(12, 3.15) * mm, "end": v(12, 1.15) * mm});
            skLineSegment(sketch, "E8.17.10.1", {"start": v(10, 3.15) * mm, "end": v(10, 1.15) * mm});
            skLineSegment(sketch, "E8.17.10.2", {"start": v(10, 1.15) * mm, "end": v(12, 1.15) * mm});
            skLineSegment(sketch, "E8.17.10.3", {"start": v(10, 3.15) * mm, "end": v(12, 3.15) * mm});
            skLineSegment(sketch, "E8.17.11.0", {"start": v(12, -0.85) * mm, "end": v(12, -2.85) * mm});
            skLineSegment(sketch, "E8.17.11.1", {"start": v(10, -0.85) * mm, "end": v(10, -2.85) * mm});
            skLineSegment(sketch, "E8.17.11.2", {"start": v(10, -2.85) * mm, "end": v(12, -2.85) * mm});
            skLineSegment(sketch, "E8.17.11.3", {"start": v(10, -0.85) * mm, "end": v(12, -0.85) * mm});
            skLineSegment(sketch, "E8.17.12.0", {"start": v(12, -4.85) * mm, "end": v(12, -6.85) * mm});
            skLineSegment(sketch, "E8.17.12.1", {"start": v(10, -4.85) * mm, "end": v(10, -6.85) * mm});
            skLineSegment(sketch, "E8.17.12.2", {"start": v(10, -6.85) * mm, "end": v(12, -6.85) * mm});
            skLineSegment(sketch, "E8.17.12.3", {"start": v(10, -4.85) * mm, "end": v(12, -4.85) * mm});
            skLineSegment(sketch, "E8.17.13.0", {"start": v(12, -8.85) * mm, "end": v(12, -10.85) * mm});
            skLineSegment(sketch, "E8.17.13.1", {"start": v(10, -8.85) * mm, "end": v(10, -10.85) * mm});
            skLineSegment(sketch, "E8.17.13.2", {"start": v(10, -10.85) * mm, "end": v(12, -10.85) * mm});
            skLineSegment(sketch, "E8.17.13.3", {"start": v(10, -8.85) * mm, "end": v(12, -8.85) * mm});
            skLineSegment(sketch, "E8.17.14.0", {"start": v(12, -12.85) * mm, "end": v(12, -14.85) * mm});
            skLineSegment(sketch, "E8.17.14.1", {"start": v(10, -12.85) * mm, "end": v(10, -14.85) * mm});
            skLineSegment(sketch, "E8.17.14.2", {"start": v(10, -14.85) * mm, "end": v(12, -14.85) * mm});
            skLineSegment(sketch, "E8.17.14.3", {"start": v(10, -12.85) * mm, "end": v(12, -12.85) * mm});
            skLineSegment(sketch, "E8.17.15.0", {"start": v(12, -16.85) * mm, "end": v(12, -18.85) * mm});
            skLineSegment(sketch, "E8.17.15.1", {"start": v(10, -16.85) * mm, "end": v(10, -18.85) * mm});
            skLineSegment(sketch, "E8.17.15.2", {"start": v(10, -18.85) * mm, "end": v(12, -18.85) * mm});
            skLineSegment(sketch, "E8.17.15.3", {"start": v(10, -16.85) * mm, "end": v(12, -16.85) * mm});
            skLineSegment(sketch, "E8.17.16.0", {"start": v(12, -20.85) * mm, "end": v(12, -22.85) * mm});
            skLineSegment(sketch, "E8.17.16.1", {"start": v(10, -20.85) * mm, "end": v(10, -22.85) * mm});
            skLineSegment(sketch, "E8.17.16.2", {"start": v(10, -22.85) * mm, "end": v(12, -22.85) * mm});
            skLineSegment(sketch, "E8.17.16.3", {"start": v(10, -20.85) * mm, "end": v(12, -20.85) * mm});
            skLineSegment(sketch, "E8.17.17.0", {"start": v(12, -24.85) * mm, "end": v(12, -26.85) * mm});
            skLineSegment(sketch, "E8.17.17.1", {"start": v(10, -24.85) * mm, "end": v(10, -26.85) * mm});
            skLineSegment(sketch, "E8.17.17.2", {"start": v(10, -26.85) * mm, "end": v(12, -26.85) * mm});
            skLineSegment(sketch, "E8.17.17.3", {"start": v(10, -24.85) * mm, "end": v(12, -24.85) * mm});
            skLineSegment(sketch, "E8.17.18.0", {"start": v(12, -28.85) * mm, "end": v(12, -30.85) * mm});
            skLineSegment(sketch, "E8.17.18.1", {"start": v(10, -28.85) * mm, "end": v(10, -30.85) * mm});
            skLineSegment(sketch, "E8.17.18.2", {"start": v(10, -30.85) * mm, "end": v(12, -30.85) * mm});
            skLineSegment(sketch, "E8.17.18.3", {"start": v(10, -28.85) * mm, "end": v(12, -28.85) * mm});
            skLineSegment(sketch, "E8.17.19.0", {"start": v(12, -32.85) * mm, "end": v(12, -34.85) * mm});
            skLineSegment(sketch, "E8.17.19.1", {"start": v(10, -32.85) * mm, "end": v(10, -34.85) * mm});
            skLineSegment(sketch, "E8.17.19.2", {"start": v(10, -34.85) * mm, "end": v(12, -34.85) * mm});
            skLineSegment(sketch, "E8.17.19.3", {"start": v(10, -32.85) * mm, "end": v(12, -32.85) * mm});
            skLineSegment(sketch, "E8.17.20.0", {"start": v(12, -36.85) * mm, "end": v(12, -38.85) * mm});
            skLineSegment(sketch, "E8.17.20.1", {"start": v(10, -36.85) * mm, "end": v(10, -38.85) * mm});
            skLineSegment(sketch, "E8.17.20.2", {"start": v(10, -38.85) * mm, "end": v(12, -38.85) * mm});
            skLineSegment(sketch, "E8.17.20.3", {"start": v(10, -36.85) * mm, "end": v(12, -36.85) * mm});
            skLineSegment(sketch, "E8.17.21.0", {"start": v(12, -40.85) * mm, "end": v(12, -42.85) * mm});
            skLineSegment(sketch, "E8.17.21.1", {"start": v(10, -40.85) * mm, "end": v(10, -42.85) * mm});
            skLineSegment(sketch, "E8.17.21.2", {"start": v(10, -42.85) * mm, "end": v(12, -42.85) * mm});
            skLineSegment(sketch, "E8.17.21.3", {"start": v(10, -40.85) * mm, "end": v(12, -40.85) * mm});
            skLineSegment(sketch, "E8.18.0.0", {"start": v(16, 43.15) * mm, "end": v(16, 41.15) * mm});
            skLineSegment(sketch, "E8.18.0.1", {"start": v(14, 43.15) * mm, "end": v(14, 41.15) * mm});
            skLineSegment(sketch, "E8.18.0.2", {"start": v(14, 41.15) * mm, "end": v(16, 41.15) * mm});
            skLineSegment(sketch, "E8.18.0.3", {"start": v(14, 43.15) * mm, "end": v(16, 43.15) * mm});
            skLineSegment(sketch, "E8.18.1.0", {"start": v(16, 39.15) * mm, "end": v(16, 37.15) * mm});
            skLineSegment(sketch, "E8.18.1.1", {"start": v(14, 39.15) * mm, "end": v(14, 37.15) * mm});
            skLineSegment(sketch, "E8.18.1.2", {"start": v(14, 37.15) * mm, "end": v(16, 37.15) * mm});
            skLineSegment(sketch, "E8.18.1.3", {"start": v(14, 39.15) * mm, "end": v(16, 39.15) * mm});
            skLineSegment(sketch, "E8.18.2.0", {"start": v(16, 35.15) * mm, "end": v(16, 33.15) * mm});
            skLineSegment(sketch, "E8.18.2.1", {"start": v(14, 35.15) * mm, "end": v(14, 33.15) * mm});
            skLineSegment(sketch, "E8.18.2.2", {"start": v(14, 33.15) * mm, "end": v(16, 33.15) * mm});
            skLineSegment(sketch, "E8.18.2.3", {"start": v(14, 35.15) * mm, "end": v(16, 35.15) * mm});
            skLineSegment(sketch, "E8.18.3.0", {"start": v(16, 31.15) * mm, "end": v(16, 29.15) * mm});
            skLineSegment(sketch, "E8.18.3.1", {"start": v(14, 31.15) * mm, "end": v(14, 29.15) * mm});
            skLineSegment(sketch, "E8.18.3.2", {"start": v(14, 29.15) * mm, "end": v(16, 29.15) * mm});
            skLineSegment(sketch, "E8.18.3.3", {"start": v(14, 31.15) * mm, "end": v(16, 31.15) * mm});
            skLineSegment(sketch, "E8.18.4.0", {"start": v(16, 27.15) * mm, "end": v(16, 25.15) * mm});
            skLineSegment(sketch, "E8.18.4.1", {"start": v(14, 27.15) * mm, "end": v(14, 25.15) * mm});
            skLineSegment(sketch, "E8.18.4.2", {"start": v(14, 25.15) * mm, "end": v(16, 25.15) * mm});
            skLineSegment(sketch, "E8.18.4.3", {"start": v(14, 27.15) * mm, "end": v(16, 27.15) * mm});
            skLineSegment(sketch, "E8.18.5.0", {"start": v(16, 23.15) * mm, "end": v(16, 21.15) * mm});
            skLineSegment(sketch, "E8.18.5.1", {"start": v(14, 23.15) * mm, "end": v(14, 21.15) * mm});
            skLineSegment(sketch, "E8.18.5.2", {"start": v(14, 21.15) * mm, "end": v(16, 21.15) * mm});
            skLineSegment(sketch, "E8.18.5.3", {"start": v(14, 23.15) * mm, "end": v(16, 23.15) * mm});
            skLineSegment(sketch, "E8.18.6.0", {"start": v(16, 19.15) * mm, "end": v(16, 17.15) * mm});
            skLineSegment(sketch, "E8.18.6.1", {"start": v(14, 19.15) * mm, "end": v(14, 17.15) * mm});
            skLineSegment(sketch, "E8.18.6.2", {"start": v(14, 17.15) * mm, "end": v(16, 17.15) * mm});
            skLineSegment(sketch, "E8.18.6.3", {"start": v(14, 19.15) * mm, "end": v(16, 19.15) * mm});
            skLineSegment(sketch, "E8.18.7.0", {"start": v(16, 15.15) * mm, "end": v(16, 13.15) * mm});
            skLineSegment(sketch, "E8.18.7.1", {"start": v(14, 15.15) * mm, "end": v(14, 13.15) * mm});
            skLineSegment(sketch, "E8.18.7.2", {"start": v(14, 13.15) * mm, "end": v(16, 13.15) * mm});
            skLineSegment(sketch, "E8.18.7.3", {"start": v(14, 15.15) * mm, "end": v(16, 15.15) * mm});
            skLineSegment(sketch, "E8.18.8.0", {"start": v(16, 11.15) * mm, "end": v(16, 9.15) * mm});
            skLineSegment(sketch, "E8.18.8.1", {"start": v(14, 11.15) * mm, "end": v(14, 9.15) * mm});
            skLineSegment(sketch, "E8.18.8.2", {"start": v(14, 9.15) * mm, "end": v(16, 9.15) * mm});
            skLineSegment(sketch, "E8.18.8.3", {"start": v(14, 11.15) * mm, "end": v(16, 11.15) * mm});
            skLineSegment(sketch, "E8.18.9.0", {"start": v(16, 7.15) * mm, "end": v(16, 5.15) * mm});
            skLineSegment(sketch, "E8.18.9.1", {"start": v(14, 7.15) * mm, "end": v(14, 5.15) * mm});
            skLineSegment(sketch, "E8.18.9.2", {"start": v(14, 5.15) * mm, "end": v(16, 5.15) * mm});
            skLineSegment(sketch, "E8.18.9.3", {"start": v(14, 7.15) * mm, "end": v(16, 7.15) * mm});
            skLineSegment(sketch, "E8.18.10.0", {"start": v(16, 3.15) * mm, "end": v(16, 1.15) * mm});
            skLineSegment(sketch, "E8.18.10.1", {"start": v(14, 3.15) * mm, "end": v(14, 1.15) * mm});
            skLineSegment(sketch, "E8.18.10.2", {"start": v(14, 1.15) * mm, "end": v(16, 1.15) * mm});
            skLineSegment(sketch, "E8.18.10.3", {"start": v(14, 3.15) * mm, "end": v(16, 3.15) * mm});
            skLineSegment(sketch, "E8.18.11.0", {"start": v(16, -0.85) * mm, "end": v(16, -2.85) * mm});
            skLineSegment(sketch, "E8.18.11.1", {"start": v(14, -0.85) * mm, "end": v(14, -2.85) * mm});
            skLineSegment(sketch, "E8.18.11.2", {"start": v(14, -2.85) * mm, "end": v(16, -2.85) * mm});
            skLineSegment(sketch, "E8.18.11.3", {"start": v(14, -0.85) * mm, "end": v(16, -0.85) * mm});
            skLineSegment(sketch, "E8.18.12.0", {"start": v(16, -4.85) * mm, "end": v(16, -6.85) * mm});
            skLineSegment(sketch, "E8.18.12.1", {"start": v(14, -4.85) * mm, "end": v(14, -6.85) * mm});
            skLineSegment(sketch, "E8.18.12.2", {"start": v(14, -6.85) * mm, "end": v(16, -6.85) * mm});
            skLineSegment(sketch, "E8.18.12.3", {"start": v(14, -4.85) * mm, "end": v(16, -4.85) * mm});
            skLineSegment(sketch, "E8.18.13.0", {"start": v(16, -8.85) * mm, "end": v(16, -10.85) * mm});
            skLineSegment(sketch, "E8.18.13.1", {"start": v(14, -8.85) * mm, "end": v(14, -10.85) * mm});
            skLineSegment(sketch, "E8.18.13.2", {"start": v(14, -10.85) * mm, "end": v(16, -10.85) * mm});
            skLineSegment(sketch, "E8.18.13.3", {"start": v(14, -8.85) * mm, "end": v(16, -8.85) * mm});
            skLineSegment(sketch, "E8.18.14.0", {"start": v(16, -12.85) * mm, "end": v(16, -14.85) * mm});
            skLineSegment(sketch, "E8.18.14.1", {"start": v(14, -12.85) * mm, "end": v(14, -14.85) * mm});
            skLineSegment(sketch, "E8.18.14.2", {"start": v(14, -14.85) * mm, "end": v(16, -14.85) * mm});
            skLineSegment(sketch, "E8.18.14.3", {"start": v(14, -12.85) * mm, "end": v(16, -12.85) * mm});
            skLineSegment(sketch, "E8.18.15.0", {"start": v(16, -16.85) * mm, "end": v(16, -18.85) * mm});
            skLineSegment(sketch, "E8.18.15.1", {"start": v(14, -16.85) * mm, "end": v(14, -18.85) * mm});
            skLineSegment(sketch, "E8.18.15.2", {"start": v(14, -18.85) * mm, "end": v(16, -18.85) * mm});
            skLineSegment(sketch, "E8.18.15.3", {"start": v(14, -16.85) * mm, "end": v(16, -16.85) * mm});
            skLineSegment(sketch, "E8.18.16.0", {"start": v(16, -20.85) * mm, "end": v(16, -22.85) * mm});
            skLineSegment(sketch, "E8.18.16.1", {"start": v(14, -20.85) * mm, "end": v(14, -22.85) * mm});
            skLineSegment(sketch, "E8.18.16.2", {"start": v(14, -22.85) * mm, "end": v(16, -22.85) * mm});
            skLineSegment(sketch, "E8.18.16.3", {"start": v(14, -20.85) * mm, "end": v(16, -20.85) * mm});
            skLineSegment(sketch, "E8.18.17.0", {"start": v(16, -24.85) * mm, "end": v(16, -26.85) * mm});
            skLineSegment(sketch, "E8.18.17.1", {"start": v(14, -24.85) * mm, "end": v(14, -26.85) * mm});
            skLineSegment(sketch, "E8.18.17.2", {"start": v(14, -26.85) * mm, "end": v(16, -26.85) * mm});
            skLineSegment(sketch, "E8.18.17.3", {"start": v(14, -24.85) * mm, "end": v(16, -24.85) * mm});
            skLineSegment(sketch, "E8.18.18.0", {"start": v(16, -28.85) * mm, "end": v(16, -30.85) * mm});
            skLineSegment(sketch, "E8.18.18.1", {"start": v(14, -28.85) * mm, "end": v(14, -30.85) * mm});
            skLineSegment(sketch, "E8.18.18.2", {"start": v(14, -30.85) * mm, "end": v(16, -30.85) * mm});
            skLineSegment(sketch, "E8.18.18.3", {"start": v(14, -28.85) * mm, "end": v(16, -28.85) * mm});
            skLineSegment(sketch, "E8.18.19.0", {"start": v(16, -32.85) * mm, "end": v(16, -34.85) * mm});
            skLineSegment(sketch, "E8.18.19.1", {"start": v(14, -32.85) * mm, "end": v(14, -34.85) * mm});
            skLineSegment(sketch, "E8.18.19.2", {"start": v(14, -34.85) * mm, "end": v(16, -34.85) * mm});
            skLineSegment(sketch, "E8.18.19.3", {"start": v(14, -32.85) * mm, "end": v(16, -32.85) * mm});
            skLineSegment(sketch, "E8.18.20.0", {"start": v(16, -36.85) * mm, "end": v(16, -38.85) * mm});
            skLineSegment(sketch, "E8.18.20.1", {"start": v(14, -36.85) * mm, "end": v(14, -38.85) * mm});
            skLineSegment(sketch, "E8.18.20.2", {"start": v(14, -38.85) * mm, "end": v(16, -38.85) * mm});
            skLineSegment(sketch, "E8.18.20.3", {"start": v(14, -36.85) * mm, "end": v(16, -36.85) * mm});
            skLineSegment(sketch, "E8.18.21.0", {"start": v(16, -40.85) * mm, "end": v(16, -42.85) * mm});
            skLineSegment(sketch, "E8.18.21.1", {"start": v(14, -40.85) * mm, "end": v(14, -42.85) * mm});
            skLineSegment(sketch, "E8.18.21.2", {"start": v(14, -42.85) * mm, "end": v(16, -42.85) * mm});
            skLineSegment(sketch, "E8.18.21.3", {"start": v(14, -40.85) * mm, "end": v(16, -40.85) * mm});
            skLineSegment(sketch, "E8.19.0.0", {"start": v(20, 43.15) * mm, "end": v(20, 41.15) * mm});
            skLineSegment(sketch, "E8.19.0.1", {"start": v(18, 43.15) * mm, "end": v(18, 41.15) * mm});
            skLineSegment(sketch, "E8.19.0.2", {"start": v(18, 41.15) * mm, "end": v(20, 41.15) * mm});
            skLineSegment(sketch, "E8.19.0.3", {"start": v(18, 43.15) * mm, "end": v(20, 43.15) * mm});
            skLineSegment(sketch, "E8.19.1.0", {"start": v(20, 39.15) * mm, "end": v(20, 37.15) * mm});
            skLineSegment(sketch, "E8.19.1.1", {"start": v(18, 39.15) * mm, "end": v(18, 37.15) * mm});
            skLineSegment(sketch, "E8.19.1.2", {"start": v(18, 37.15) * mm, "end": v(20, 37.15) * mm});
            skLineSegment(sketch, "E8.19.1.3", {"start": v(18, 39.15) * mm, "end": v(20, 39.15) * mm});
            skLineSegment(sketch, "E8.19.2.0", {"start": v(20, 35.15) * mm, "end": v(20, 33.15) * mm});
            skLineSegment(sketch, "E8.19.2.1", {"start": v(18, 35.15) * mm, "end": v(18, 33.15) * mm});
            skLineSegment(sketch, "E8.19.2.2", {"start": v(18, 33.15) * mm, "end": v(20, 33.15) * mm});
            skLineSegment(sketch, "E8.19.2.3", {"start": v(18, 35.15) * mm, "end": v(20, 35.15) * mm});
            skLineSegment(sketch, "E8.19.3.0", {"start": v(20, 31.15) * mm, "end": v(20, 29.15) * mm});
            skLineSegment(sketch, "E8.19.3.1", {"start": v(18, 31.15) * mm, "end": v(18, 29.15) * mm});
            skLineSegment(sketch, "E8.19.3.2", {"start": v(18, 29.15) * mm, "end": v(20, 29.15) * mm});
            skLineSegment(sketch, "E8.19.3.3", {"start": v(18, 31.15) * mm, "end": v(20, 31.15) * mm});
            skLineSegment(sketch, "E8.19.4.0", {"start": v(20, 27.15) * mm, "end": v(20, 25.15) * mm});
            skLineSegment(sketch, "E8.19.4.1", {"start": v(18, 27.15) * mm, "end": v(18, 25.15) * mm});
            skLineSegment(sketch, "E8.19.4.2", {"start": v(18, 25.15) * mm, "end": v(20, 25.15) * mm});
            skLineSegment(sketch, "E8.19.4.3", {"start": v(18, 27.15) * mm, "end": v(20, 27.15) * mm});
            skLineSegment(sketch, "E8.19.5.0", {"start": v(20, 23.15) * mm, "end": v(20, 21.15) * mm});
            skLineSegment(sketch, "E8.19.5.1", {"start": v(18, 23.15) * mm, "end": v(18, 21.15) * mm});
            skLineSegment(sketch, "E8.19.5.2", {"start": v(18, 21.15) * mm, "end": v(20, 21.15) * mm});
            skLineSegment(sketch, "E8.19.5.3", {"start": v(18, 23.15) * mm, "end": v(20, 23.15) * mm});
            skLineSegment(sketch, "E8.19.6.0", {"start": v(20, 19.15) * mm, "end": v(20, 17.15) * mm});
            skLineSegment(sketch, "E8.19.6.1", {"start": v(18, 19.15) * mm, "end": v(18, 17.15) * mm});
            skLineSegment(sketch, "E8.19.6.2", {"start": v(18, 17.15) * mm, "end": v(20, 17.15) * mm});
            skLineSegment(sketch, "E8.19.6.3", {"start": v(18, 19.15) * mm, "end": v(20, 19.15) * mm});
            skLineSegment(sketch, "E8.19.7.0", {"start": v(20, 15.15) * mm, "end": v(20, 13.15) * mm});
            skLineSegment(sketch, "E8.19.7.1", {"start": v(18, 15.15) * mm, "end": v(18, 13.15) * mm});
            skLineSegment(sketch, "E8.19.7.2", {"start": v(18, 13.15) * mm, "end": v(20, 13.15) * mm});
            skLineSegment(sketch, "E8.19.7.3", {"start": v(18, 15.15) * mm, "end": v(20, 15.15) * mm});
            skLineSegment(sketch, "E8.19.8.0", {"start": v(20, 11.15) * mm, "end": v(20, 9.15) * mm});
            skLineSegment(sketch, "E8.19.8.1", {"start": v(18, 11.15) * mm, "end": v(18, 9.15) * mm});
            skLineSegment(sketch, "E8.19.8.2", {"start": v(18, 9.15) * mm, "end": v(20, 9.15) * mm});
            skLineSegment(sketch, "E8.19.8.3", {"start": v(18, 11.15) * mm, "end": v(20, 11.15) * mm});
            skLineSegment(sketch, "E8.19.9.0", {"start": v(20, 7.15) * mm, "end": v(20, 5.15) * mm});
            skLineSegment(sketch, "E8.19.9.1", {"start": v(18, 7.15) * mm, "end": v(18, 5.15) * mm});
            skLineSegment(sketch, "E8.19.9.2", {"start": v(18, 5.15) * mm, "end": v(20, 5.15) * mm});
            skLineSegment(sketch, "E8.19.9.3", {"start": v(18, 7.15) * mm, "end": v(20, 7.15) * mm});
            skLineSegment(sketch, "E8.19.10.0", {"start": v(20, 3.15) * mm, "end": v(20, 1.15) * mm});
            skLineSegment(sketch, "E8.19.10.1", {"start": v(18, 3.15) * mm, "end": v(18, 1.15) * mm});
            skLineSegment(sketch, "E8.19.10.2", {"start": v(18, 1.15) * mm, "end": v(20, 1.15) * mm});
            skLineSegment(sketch, "E8.19.10.3", {"start": v(18, 3.15) * mm, "end": v(20, 3.15) * mm});
            skLineSegment(sketch, "E8.19.11.0", {"start": v(20, -0.85) * mm, "end": v(20, -2.85) * mm});
            skLineSegment(sketch, "E8.19.11.1", {"start": v(18, -0.85) * mm, "end": v(18, -2.85) * mm});
            skLineSegment(sketch, "E8.19.11.2", {"start": v(18, -2.85) * mm, "end": v(20, -2.85) * mm});
            skLineSegment(sketch, "E8.19.11.3", {"start": v(18, -0.85) * mm, "end": v(20, -0.85) * mm});
            skLineSegment(sketch, "E8.19.12.0", {"start": v(20, -4.85) * mm, "end": v(20, -6.85) * mm});
            skLineSegment(sketch, "E8.19.12.1", {"start": v(18, -4.85) * mm, "end": v(18, -6.85) * mm});
            skLineSegment(sketch, "E8.19.12.2", {"start": v(18, -6.85) * mm, "end": v(20, -6.85) * mm});
            skLineSegment(sketch, "E8.19.12.3", {"start": v(18, -4.85) * mm, "end": v(20, -4.85) * mm});
            skLineSegment(sketch, "E8.19.13.0", {"start": v(20, -8.85) * mm, "end": v(20, -10.85) * mm});
            skLineSegment(sketch, "E8.19.13.1", {"start": v(18, -8.85) * mm, "end": v(18, -10.85) * mm});
            skLineSegment(sketch, "E8.19.13.2", {"start": v(18, -10.85) * mm, "end": v(20, -10.85) * mm});
            skLineSegment(sketch, "E8.19.13.3", {"start": v(18, -8.85) * mm, "end": v(20, -8.85) * mm});
            skLineSegment(sketch, "E8.19.14.0", {"start": v(20, -12.85) * mm, "end": v(20, -14.85) * mm});
            skLineSegment(sketch, "E8.19.14.1", {"start": v(18, -12.85) * mm, "end": v(18, -14.85) * mm});
            skLineSegment(sketch, "E8.19.14.2", {"start": v(18, -14.85) * mm, "end": v(20, -14.85) * mm});
            skLineSegment(sketch, "E8.19.14.3", {"start": v(18, -12.85) * mm, "end": v(20, -12.85) * mm});
            skLineSegment(sketch, "E8.19.15.0", {"start": v(20, -16.85) * mm, "end": v(20, -18.85) * mm});
            skLineSegment(sketch, "E8.19.15.1", {"start": v(18, -16.85) * mm, "end": v(18, -18.85) * mm});
            skLineSegment(sketch, "E8.19.15.2", {"start": v(18, -18.85) * mm, "end": v(20, -18.85) * mm});
            skLineSegment(sketch, "E8.19.15.3", {"start": v(18, -16.85) * mm, "end": v(20, -16.85) * mm});
            skLineSegment(sketch, "E8.19.16.0", {"start": v(20, -20.85) * mm, "end": v(20, -22.85) * mm});
            skLineSegment(sketch, "E8.19.16.1", {"start": v(18, -20.85) * mm, "end": v(18, -22.85) * mm});
            skLineSegment(sketch, "E8.19.16.2", {"start": v(18, -22.85) * mm, "end": v(20, -22.85) * mm});
            skLineSegment(sketch, "E8.19.16.3", {"start": v(18, -20.85) * mm, "end": v(20, -20.85) * mm});
            skLineSegment(sketch, "E8.19.17.0", {"start": v(20, -24.85) * mm, "end": v(20, -26.85) * mm});
            skLineSegment(sketch, "E8.19.17.1", {"start": v(18, -24.85) * mm, "end": v(18, -26.85) * mm});
            skLineSegment(sketch, "E8.19.17.2", {"start": v(18, -26.85) * mm, "end": v(20, -26.85) * mm});
            skLineSegment(sketch, "E8.19.17.3", {"start": v(18, -24.85) * mm, "end": v(20, -24.85) * mm});
            skLineSegment(sketch, "E8.19.18.0", {"start": v(20, -28.85) * mm, "end": v(20, -30.85) * mm});
            skLineSegment(sketch, "E8.19.18.1", {"start": v(18, -28.85) * mm, "end": v(18, -30.85) * mm});
            skLineSegment(sketch, "E8.19.18.2", {"start": v(18, -30.85) * mm, "end": v(20, -30.85) * mm});
            skLineSegment(sketch, "E8.19.18.3", {"start": v(18, -28.85) * mm, "end": v(20, -28.85) * mm});
            skLineSegment(sketch, "E8.19.19.0", {"start": v(20, -32.85) * mm, "end": v(20, -34.85) * mm});
            skLineSegment(sketch, "E8.19.19.1", {"start": v(18, -32.85) * mm, "end": v(18, -34.85) * mm});
            skLineSegment(sketch, "E8.19.19.2", {"start": v(18, -34.85) * mm, "end": v(20, -34.85) * mm});
            skLineSegment(sketch, "E8.19.19.3", {"start": v(18, -32.85) * mm, "end": v(20, -32.85) * mm});
            skLineSegment(sketch, "E8.19.20.0", {"start": v(20, -36.85) * mm, "end": v(20, -38.85) * mm});
            skLineSegment(sketch, "E8.19.20.1", {"start": v(18, -36.85) * mm, "end": v(18, -38.85) * mm});
            skLineSegment(sketch, "E8.19.20.2", {"start": v(18, -38.85) * mm, "end": v(20, -38.85) * mm});
            skLineSegment(sketch, "E8.19.20.3", {"start": v(18, -36.85) * mm, "end": v(20, -36.85) * mm});
            skLineSegment(sketch, "E8.19.21.0", {"start": v(20, -40.85) * mm, "end": v(20, -42.85) * mm});
            skLineSegment(sketch, "E8.19.21.1", {"start": v(18, -40.85) * mm, "end": v(18, -42.85) * mm});
            skLineSegment(sketch, "E8.19.21.2", {"start": v(18, -42.85) * mm, "end": v(20, -42.85) * mm});
            skLineSegment(sketch, "E8.19.21.3", {"start": v(18, -40.85) * mm, "end": v(20, -40.85) * mm});
            skLineSegment(sketch, "E8.20.0.0", {"start": v(24, 43.15) * mm, "end": v(24, 41.15) * mm});
            skLineSegment(sketch, "E8.20.0.1", {"start": v(22, 43.15) * mm, "end": v(22, 41.15) * mm});
            skLineSegment(sketch, "E8.20.0.2", {"start": v(22, 41.15) * mm, "end": v(24, 41.15) * mm});
            skLineSegment(sketch, "E8.20.0.3", {"start": v(22, 43.15) * mm, "end": v(24, 43.15) * mm});
            skLineSegment(sketch, "E8.20.1.0", {"start": v(24, 39.15) * mm, "end": v(24, 37.15) * mm});
            skLineSegment(sketch, "E8.20.1.1", {"start": v(22, 39.15) * mm, "end": v(22, 37.15) * mm});
            skLineSegment(sketch, "E8.20.1.2", {"start": v(22, 37.15) * mm, "end": v(24, 37.15) * mm});
            skLineSegment(sketch, "E8.20.1.3", {"start": v(22, 39.15) * mm, "end": v(24, 39.15) * mm});
            skLineSegment(sketch, "E8.20.2.0", {"start": v(24, 35.15) * mm, "end": v(24, 33.15) * mm});
            skLineSegment(sketch, "E8.20.2.1", {"start": v(22, 35.15) * mm, "end": v(22, 33.15) * mm});
            skLineSegment(sketch, "E8.20.2.2", {"start": v(22, 33.15) * mm, "end": v(24, 33.15) * mm});
            skLineSegment(sketch, "E8.20.2.3", {"start": v(22, 35.15) * mm, "end": v(24, 35.15) * mm});
            skLineSegment(sketch, "E8.20.3.0", {"start": v(24, 31.15) * mm, "end": v(24, 29.15) * mm});
            skLineSegment(sketch, "E8.20.3.1", {"start": v(22, 31.15) * mm, "end": v(22, 29.15) * mm});
            skLineSegment(sketch, "E8.20.3.2", {"start": v(22, 29.15) * mm, "end": v(24, 29.15) * mm});
            skLineSegment(sketch, "E8.20.3.3", {"start": v(22, 31.15) * mm, "end": v(24, 31.15) * mm});
            skLineSegment(sketch, "E8.20.4.0", {"start": v(24, 27.15) * mm, "end": v(24, 25.15) * mm});
            skLineSegment(sketch, "E8.20.4.1", {"start": v(22, 27.15) * mm, "end": v(22, 25.15) * mm});
            skLineSegment(sketch, "E8.20.4.2", {"start": v(22, 25.15) * mm, "end": v(24, 25.15) * mm});
            skLineSegment(sketch, "E8.20.4.3", {"start": v(22, 27.15) * mm, "end": v(24, 27.15) * mm});
            skLineSegment(sketch, "E8.20.5.0", {"start": v(24, 23.15) * mm, "end": v(24, 21.15) * mm});
            skLineSegment(sketch, "E8.20.5.1", {"start": v(22, 23.15) * mm, "end": v(22, 21.15) * mm});
            skLineSegment(sketch, "E8.20.5.2", {"start": v(22, 21.15) * mm, "end": v(24, 21.15) * mm});
            skLineSegment(sketch, "E8.20.5.3", {"start": v(22, 23.15) * mm, "end": v(24, 23.15) * mm});
            skLineSegment(sketch, "E8.20.6.0", {"start": v(24, 19.15) * mm, "end": v(24, 17.15) * mm});
            skLineSegment(sketch, "E8.20.6.1", {"start": v(22, 19.15) * mm, "end": v(22, 17.15) * mm});
            skLineSegment(sketch, "E8.20.6.2", {"start": v(22, 17.15) * mm, "end": v(24, 17.15) * mm});
            skLineSegment(sketch, "E8.20.6.3", {"start": v(22, 19.15) * mm, "end": v(24, 19.15) * mm});
            skLineSegment(sketch, "E8.20.7.0", {"start": v(24, 15.15) * mm, "end": v(24, 13.15) * mm});
            skLineSegment(sketch, "E8.20.7.1", {"start": v(22, 15.15) * mm, "end": v(22, 13.15) * mm});
            skLineSegment(sketch, "E8.20.7.2", {"start": v(22, 13.15) * mm, "end": v(24, 13.15) * mm});
            skLineSegment(sketch, "E8.20.7.3", {"start": v(22, 15.15) * mm, "end": v(24, 15.15) * mm});
            skLineSegment(sketch, "E8.20.8.0", {"start": v(24, 11.15) * mm, "end": v(24, 9.15) * mm});
            skLineSegment(sketch, "E8.20.8.1", {"start": v(22, 11.15) * mm, "end": v(22, 9.15) * mm});
            skLineSegment(sketch, "E8.20.8.2", {"start": v(22, 9.15) * mm, "end": v(24, 9.15) * mm});
            skLineSegment(sketch, "E8.20.8.3", {"start": v(22, 11.15) * mm, "end": v(24, 11.15) * mm});
            skLineSegment(sketch, "E8.20.9.0", {"start": v(24, 7.15) * mm, "end": v(24, 5.15) * mm});
            skLineSegment(sketch, "E8.20.9.1", {"start": v(22, 7.15) * mm, "end": v(22, 5.15) * mm});
            skLineSegment(sketch, "E8.20.9.2", {"start": v(22, 5.15) * mm, "end": v(24, 5.15) * mm});
            skLineSegment(sketch, "E8.20.9.3", {"start": v(22, 7.15) * mm, "end": v(24, 7.15) * mm});
            skLineSegment(sketch, "E8.20.10.0", {"start": v(24, 3.15) * mm, "end": v(24, 1.15) * mm});
            skLineSegment(sketch, "E8.20.10.1", {"start": v(22, 3.15) * mm, "end": v(22, 1.15) * mm});
            skLineSegment(sketch, "E8.20.10.2", {"start": v(22, 1.15) * mm, "end": v(24, 1.15) * mm});
            skLineSegment(sketch, "E8.20.10.3", {"start": v(22, 3.15) * mm, "end": v(24, 3.15) * mm});
            skLineSegment(sketch, "E8.20.11.0", {"start": v(24, -0.85) * mm, "end": v(24, -2.85) * mm});
            skLineSegment(sketch, "E8.20.11.1", {"start": v(22, -0.85) * mm, "end": v(22, -2.85) * mm});
            skLineSegment(sketch, "E8.20.11.2", {"start": v(22, -2.85) * mm, "end": v(24, -2.85) * mm});
            skLineSegment(sketch, "E8.20.11.3", {"start": v(22, -0.85) * mm, "end": v(24, -0.85) * mm});
            skLineSegment(sketch, "E8.20.12.0", {"start": v(24, -4.85) * mm, "end": v(24, -6.85) * mm});
            skLineSegment(sketch, "E8.20.12.1", {"start": v(22, -4.85) * mm, "end": v(22, -6.85) * mm});
            skLineSegment(sketch, "E8.20.12.2", {"start": v(22, -6.85) * mm, "end": v(24, -6.85) * mm});
            skLineSegment(sketch, "E8.20.12.3", {"start": v(22, -4.85) * mm, "end": v(24, -4.85) * mm});
            skLineSegment(sketch, "E8.20.13.0", {"start": v(24, -8.85) * mm, "end": v(24, -10.85) * mm});
            skLineSegment(sketch, "E8.20.13.1", {"start": v(22, -8.85) * mm, "end": v(22, -10.85) * mm});
            skLineSegment(sketch, "E8.20.13.2", {"start": v(22, -10.85) * mm, "end": v(24, -10.85) * mm});
            skLineSegment(sketch, "E8.20.13.3", {"start": v(22, -8.85) * mm, "end": v(24, -8.85) * mm});
            skLineSegment(sketch, "E8.20.14.0", {"start": v(24, -12.85) * mm, "end": v(24, -14.85) * mm});
            skLineSegment(sketch, "E8.20.14.1", {"start": v(22, -12.85) * mm, "end": v(22, -14.85) * mm});
            skLineSegment(sketch, "E8.20.14.2", {"start": v(22, -14.85) * mm, "end": v(24, -14.85) * mm});
            skLineSegment(sketch, "E8.20.14.3", {"start": v(22, -12.85) * mm, "end": v(24, -12.85) * mm});
            skLineSegment(sketch, "E8.20.15.0", {"start": v(24, -16.85) * mm, "end": v(24, -18.85) * mm});
            skLineSegment(sketch, "E8.20.15.1", {"start": v(22, -16.85) * mm, "end": v(22, -18.85) * mm});
            skLineSegment(sketch, "E8.20.15.2", {"start": v(22, -18.85) * mm, "end": v(24, -18.85) * mm});
            skLineSegment(sketch, "E8.20.15.3", {"start": v(22, -16.85) * mm, "end": v(24, -16.85) * mm});
            skLineSegment(sketch, "E8.20.16.0", {"start": v(24, -20.85) * mm, "end": v(24, -22.85) * mm});
            skLineSegment(sketch, "E8.20.16.1", {"start": v(22, -20.85) * mm, "end": v(22, -22.85) * mm});
            skLineSegment(sketch, "E8.20.16.2", {"start": v(22, -22.85) * mm, "end": v(24, -22.85) * mm});
            skLineSegment(sketch, "E8.20.16.3", {"start": v(22, -20.85) * mm, "end": v(24, -20.85) * mm});
            skLineSegment(sketch, "E8.20.17.0", {"start": v(24, -24.85) * mm, "end": v(24, -26.85) * mm});
            skLineSegment(sketch, "E8.20.17.1", {"start": v(22, -24.85) * mm, "end": v(22, -26.85) * mm});
            skLineSegment(sketch, "E8.20.17.2", {"start": v(22, -26.85) * mm, "end": v(24, -26.85) * mm});
            skLineSegment(sketch, "E8.20.17.3", {"start": v(22, -24.85) * mm, "end": v(24, -24.85) * mm});
            skLineSegment(sketch, "E8.20.18.0", {"start": v(24, -28.85) * mm, "end": v(24, -30.85) * mm});
            skLineSegment(sketch, "E8.20.18.1", {"start": v(22, -28.85) * mm, "end": v(22, -30.85) * mm});
            skLineSegment(sketch, "E8.20.18.2", {"start": v(22, -30.85) * mm, "end": v(24, -30.85) * mm});
            skLineSegment(sketch, "E8.20.18.3", {"start": v(22, -28.85) * mm, "end": v(24, -28.85) * mm});
            skLineSegment(sketch, "E8.20.19.0", {"start": v(24, -32.85) * mm, "end": v(24, -34.85) * mm});
            skLineSegment(sketch, "E8.20.19.1", {"start": v(22, -32.85) * mm, "end": v(22, -34.85) * mm});
            skLineSegment(sketch, "E8.20.19.2", {"start": v(22, -34.85) * mm, "end": v(24, -34.85) * mm});
            skLineSegment(sketch, "E8.20.19.3", {"start": v(22, -32.85) * mm, "end": v(24, -32.85) * mm});
            skLineSegment(sketch, "E8.20.20.0", {"start": v(24, -36.85) * mm, "end": v(24, -38.85) * mm});
            skLineSegment(sketch, "E8.20.20.1", {"start": v(22, -36.85) * mm, "end": v(22, -38.85) * mm});
            skLineSegment(sketch, "E8.20.20.2", {"start": v(22, -38.85) * mm, "end": v(24, -38.85) * mm});
            skLineSegment(sketch, "E8.20.20.3", {"start": v(22, -36.85) * mm, "end": v(24, -36.85) * mm});
            skLineSegment(sketch, "E8.20.21.0", {"start": v(24, -40.85) * mm, "end": v(24, -42.85) * mm});
            skLineSegment(sketch, "E8.20.21.1", {"start": v(22, -40.85) * mm, "end": v(22, -42.85) * mm});
            skLineSegment(sketch, "E8.20.21.2", {"start": v(22, -42.85) * mm, "end": v(24, -42.85) * mm});
            skLineSegment(sketch, "E8.20.21.3", {"start": v(22, -40.85) * mm, "end": v(24, -40.85) * mm});
            skLineSegment(sketch, "E8.21.0.0", {"start": v(28, 43.15) * mm, "end": v(28, 41.15) * mm});
            skLineSegment(sketch, "E8.21.0.1", {"start": v(26, 43.15) * mm, "end": v(26, 41.15) * mm});
            skLineSegment(sketch, "E8.21.0.2", {"start": v(26, 41.15) * mm, "end": v(28, 41.15) * mm});
            skLineSegment(sketch, "E8.21.0.3", {"start": v(26, 43.15) * mm, "end": v(28, 43.15) * mm});
            skLineSegment(sketch, "E8.21.1.0", {"start": v(28, 39.15) * mm, "end": v(28, 37.15) * mm});
            skLineSegment(sketch, "E8.21.1.1", {"start": v(26, 39.15) * mm, "end": v(26, 37.15) * mm});
            skLineSegment(sketch, "E8.21.1.2", {"start": v(26, 37.15) * mm, "end": v(28, 37.15) * mm});
            skLineSegment(sketch, "E8.21.1.3", {"start": v(26, 39.15) * mm, "end": v(28, 39.15) * mm});
            skLineSegment(sketch, "E8.21.2.0", {"start": v(28, 35.15) * mm, "end": v(28, 33.15) * mm});
            skLineSegment(sketch, "E8.21.2.1", {"start": v(26, 35.15) * mm, "end": v(26, 33.15) * mm});
            skLineSegment(sketch, "E8.21.2.2", {"start": v(26, 33.15) * mm, "end": v(28, 33.15) * mm});
            skLineSegment(sketch, "E8.21.2.3", {"start": v(26, 35.15) * mm, "end": v(28, 35.15) * mm});
            skLineSegment(sketch, "E8.21.3.0", {"start": v(28, 31.15) * mm, "end": v(28, 29.15) * mm});
            skLineSegment(sketch, "E8.21.3.1", {"start": v(26, 31.15) * mm, "end": v(26, 29.15) * mm});
            skLineSegment(sketch, "E8.21.3.2", {"start": v(26, 29.15) * mm, "end": v(28, 29.15) * mm});
            skLineSegment(sketch, "E8.21.3.3", {"start": v(26, 31.15) * mm, "end": v(28, 31.15) * mm});
            skLineSegment(sketch, "E8.21.4.0", {"start": v(28, 27.15) * mm, "end": v(28, 25.15) * mm});
            skLineSegment(sketch, "E8.21.4.1", {"start": v(26, 27.15) * mm, "end": v(26, 25.15) * mm});
            skLineSegment(sketch, "E8.21.4.2", {"start": v(26, 25.15) * mm, "end": v(28, 25.15) * mm});
            skLineSegment(sketch, "E8.21.4.3", {"start": v(26, 27.15) * mm, "end": v(28, 27.15) * mm});
            skLineSegment(sketch, "E8.21.5.0", {"start": v(28, 23.15) * mm, "end": v(28, 21.15) * mm});
            skLineSegment(sketch, "E8.21.5.1", {"start": v(26, 23.15) * mm, "end": v(26, 21.15) * mm});
            skLineSegment(sketch, "E8.21.5.2", {"start": v(26, 21.15) * mm, "end": v(28, 21.15) * mm});
            skLineSegment(sketch, "E8.21.5.3", {"start": v(26, 23.15) * mm, "end": v(28, 23.15) * mm});
            skLineSegment(sketch, "E8.21.6.0", {"start": v(28, 19.15) * mm, "end": v(28, 17.15) * mm});
            skLineSegment(sketch, "E8.21.6.1", {"start": v(26, 19.15) * mm, "end": v(26, 17.15) * mm});
            skLineSegment(sketch, "E8.21.6.2", {"start": v(26, 17.15) * mm, "end": v(28, 17.15) * mm});
            skLineSegment(sketch, "E8.21.6.3", {"start": v(26, 19.15) * mm, "end": v(28, 19.15) * mm});
            skLineSegment(sketch, "E8.21.7.0", {"start": v(28, 15.15) * mm, "end": v(28, 13.15) * mm});
            skLineSegment(sketch, "E8.21.7.1", {"start": v(26, 15.15) * mm, "end": v(26, 13.15) * mm});
            skLineSegment(sketch, "E8.21.7.2", {"start": v(26, 13.15) * mm, "end": v(28, 13.15) * mm});
            skLineSegment(sketch, "E8.21.7.3", {"start": v(26, 15.15) * mm, "end": v(28, 15.15) * mm});
            skLineSegment(sketch, "E8.21.8.0", {"start": v(28, 11.15) * mm, "end": v(28, 9.15) * mm});
            skLineSegment(sketch, "E8.21.8.1", {"start": v(26, 11.15) * mm, "end": v(26, 9.15) * mm});
            skLineSegment(sketch, "E8.21.8.2", {"start": v(26, 9.15) * mm, "end": v(28, 9.15) * mm});
            skLineSegment(sketch, "E8.21.8.3", {"start": v(26, 11.15) * mm, "end": v(28, 11.15) * mm});
            skLineSegment(sketch, "E8.21.9.0", {"start": v(28, 7.15) * mm, "end": v(28, 5.15) * mm});
            skLineSegment(sketch, "E8.21.9.1", {"start": v(26, 7.15) * mm, "end": v(26, 5.15) * mm});
            skLineSegment(sketch, "E8.21.9.2", {"start": v(26, 5.15) * mm, "end": v(28, 5.15) * mm});
            skLineSegment(sketch, "E8.21.9.3", {"start": v(26, 7.15) * mm, "end": v(28, 7.15) * mm});
            skLineSegment(sketch, "E8.21.10.0", {"start": v(28, 3.15) * mm, "end": v(28, 1.15) * mm});
            skLineSegment(sketch, "E8.21.10.1", {"start": v(26, 3.15) * mm, "end": v(26, 1.15) * mm});
            skLineSegment(sketch, "E8.21.10.2", {"start": v(26, 1.15) * mm, "end": v(28, 1.15) * mm});
            skLineSegment(sketch, "E8.21.10.3", {"start": v(26, 3.15) * mm, "end": v(28, 3.15) * mm});
            skLineSegment(sketch, "E8.21.11.0", {"start": v(28, -0.85) * mm, "end": v(28, -2.85) * mm});
            skLineSegment(sketch, "E8.21.11.1", {"start": v(26, -0.85) * mm, "end": v(26, -2.85) * mm});
            skLineSegment(sketch, "E8.21.11.2", {"start": v(26, -2.85) * mm, "end": v(28, -2.85) * mm});
            skLineSegment(sketch, "E8.21.11.3", {"start": v(26, -0.85) * mm, "end": v(28, -0.85) * mm});
            skLineSegment(sketch, "E8.21.12.0", {"start": v(28, -4.85) * mm, "end": v(28, -6.85) * mm});
            skLineSegment(sketch, "E8.21.12.1", {"start": v(26, -4.85) * mm, "end": v(26, -6.85) * mm});
            skLineSegment(sketch, "E8.21.12.2", {"start": v(26, -6.85) * mm, "end": v(28, -6.85) * mm});
            skLineSegment(sketch, "E8.21.12.3", {"start": v(26, -4.85) * mm, "end": v(28, -4.85) * mm});
            skLineSegment(sketch, "E8.21.13.0", {"start": v(28, -8.85) * mm, "end": v(28, -10.85) * mm});
            skLineSegment(sketch, "E8.21.13.1", {"start": v(26, -8.85) * mm, "end": v(26, -10.85) * mm});
            skLineSegment(sketch, "E8.21.13.2", {"start": v(26, -10.85) * mm, "end": v(28, -10.85) * mm});
            skLineSegment(sketch, "E8.21.13.3", {"start": v(26, -8.85) * mm, "end": v(28, -8.85) * mm});
            skLineSegment(sketch, "E8.21.14.0", {"start": v(28, -12.85) * mm, "end": v(28, -14.85) * mm});
            skLineSegment(sketch, "E8.21.14.1", {"start": v(26, -12.85) * mm, "end": v(26, -14.85) * mm});
            skLineSegment(sketch, "E8.21.14.2", {"start": v(26, -14.85) * mm, "end": v(28, -14.85) * mm});
            skLineSegment(sketch, "E8.21.14.3", {"start": v(26, -12.85) * mm, "end": v(28, -12.85) * mm});
            skLineSegment(sketch, "E8.21.15.0", {"start": v(28, -16.85) * mm, "end": v(28, -18.85) * mm});
            skLineSegment(sketch, "E8.21.15.1", {"start": v(26, -16.85) * mm, "end": v(26, -18.85) * mm});
            skLineSegment(sketch, "E8.21.15.2", {"start": v(26, -18.85) * mm, "end": v(28, -18.85) * mm});
            skLineSegment(sketch, "E8.21.15.3", {"start": v(26, -16.85) * mm, "end": v(28, -16.85) * mm});
            skLineSegment(sketch, "E8.21.16.0", {"start": v(28, -20.85) * mm, "end": v(28, -22.85) * mm});
            skLineSegment(sketch, "E8.21.16.1", {"start": v(26, -20.85) * mm, "end": v(26, -22.85) * mm});
            skLineSegment(sketch, "E8.21.16.2", {"start": v(26, -22.85) * mm, "end": v(28, -22.85) * mm});
            skLineSegment(sketch, "E8.21.16.3", {"start": v(26, -20.85) * mm, "end": v(28, -20.85) * mm});
            skLineSegment(sketch, "E8.21.17.0", {"start": v(28, -24.85) * mm, "end": v(28, -26.85) * mm});
            skLineSegment(sketch, "E8.21.17.1", {"start": v(26, -24.85) * mm, "end": v(26, -26.85) * mm});
            skLineSegment(sketch, "E8.21.17.2", {"start": v(26, -26.85) * mm, "end": v(28, -26.85) * mm});
            skLineSegment(sketch, "E8.21.17.3", {"start": v(26, -24.85) * mm, "end": v(28, -24.85) * mm});
            skLineSegment(sketch, "E8.21.18.0", {"start": v(28, -28.85) * mm, "end": v(28, -30.85) * mm});
            skLineSegment(sketch, "E8.21.18.1", {"start": v(26, -28.85) * mm, "end": v(26, -30.85) * mm});
            skLineSegment(sketch, "E8.21.18.2", {"start": v(26, -30.85) * mm, "end": v(28, -30.85) * mm});
            skLineSegment(sketch, "E8.21.18.3", {"start": v(26, -28.85) * mm, "end": v(28, -28.85) * mm});
            skLineSegment(sketch, "E8.21.19.0", {"start": v(28, -32.85) * mm, "end": v(28, -34.85) * mm});
            skLineSegment(sketch, "E8.21.19.1", {"start": v(26, -32.85) * mm, "end": v(26, -34.85) * mm});
            skLineSegment(sketch, "E8.21.19.2", {"start": v(26, -34.85) * mm, "end": v(28, -34.85) * mm});
            skLineSegment(sketch, "E8.21.19.3", {"start": v(26, -32.85) * mm, "end": v(28, -32.85) * mm});
            skLineSegment(sketch, "E8.21.20.0", {"start": v(28, -36.85) * mm, "end": v(28, -38.85) * mm});
            skLineSegment(sketch, "E8.21.20.1", {"start": v(26, -36.85) * mm, "end": v(26, -38.85) * mm});
            skLineSegment(sketch, "E8.21.20.2", {"start": v(26, -38.85) * mm, "end": v(28, -38.85) * mm});
            skLineSegment(sketch, "E8.21.20.3", {"start": v(26, -36.85) * mm, "end": v(28, -36.85) * mm});
            skLineSegment(sketch, "E8.21.21.0", {"start": v(28, -40.85) * mm, "end": v(28, -42.85) * mm});
            skLineSegment(sketch, "E8.21.21.1", {"start": v(26, -40.85) * mm, "end": v(26, -42.85) * mm});
            skLineSegment(sketch, "E8.21.21.2", {"start": v(26, -42.85) * mm, "end": v(28, -42.85) * mm});
            skLineSegment(sketch, "E8.21.21.3", {"start": v(26, -40.85) * mm, "end": v(28, -40.85) * mm});
            skLineSegment(sketch, "E8.22.0.0", {"start": v(32, 43.15) * mm, "end": v(32, 41.15) * mm});
            skLineSegment(sketch, "E8.22.0.1", {"start": v(30, 43.15) * mm, "end": v(30, 41.15) * mm});
            skLineSegment(sketch, "E8.22.0.2", {"start": v(30, 41.15) * mm, "end": v(32, 41.15) * mm});
            skLineSegment(sketch, "E8.22.0.3", {"start": v(30, 43.15) * mm, "end": v(32, 43.15) * mm});
            skLineSegment(sketch, "E8.22.1.0", {"start": v(32, 39.15) * mm, "end": v(32, 37.15) * mm});
            skLineSegment(sketch, "E8.22.1.1", {"start": v(30, 39.15) * mm, "end": v(30, 37.15) * mm});
            skLineSegment(sketch, "E8.22.1.2", {"start": v(30, 37.15) * mm, "end": v(32, 37.15) * mm});
            skLineSegment(sketch, "E8.22.1.3", {"start": v(30, 39.15) * mm, "end": v(32, 39.15) * mm});
            skLineSegment(sketch, "E8.22.2.0", {"start": v(32, 35.15) * mm, "end": v(32, 33.15) * mm});
            skLineSegment(sketch, "E8.22.2.1", {"start": v(30, 35.15) * mm, "end": v(30, 33.15) * mm});
            skLineSegment(sketch, "E8.22.2.2", {"start": v(30, 33.15) * mm, "end": v(32, 33.15) * mm});
            skLineSegment(sketch, "E8.22.2.3", {"start": v(30, 35.15) * mm, "end": v(32, 35.15) * mm});
            skLineSegment(sketch, "E8.22.3.0", {"start": v(32, 31.15) * mm, "end": v(32, 29.15) * mm});
            skLineSegment(sketch, "E8.22.3.1", {"start": v(30, 31.15) * mm, "end": v(30, 29.15) * mm});
            skLineSegment(sketch, "E8.22.3.2", {"start": v(30, 29.15) * mm, "end": v(32, 29.15) * mm});
            skLineSegment(sketch, "E8.22.3.3", {"start": v(30, 31.15) * mm, "end": v(32, 31.15) * mm});
            skLineSegment(sketch, "E8.22.4.0", {"start": v(32, 27.15) * mm, "end": v(32, 25.15) * mm});
            skLineSegment(sketch, "E8.22.4.1", {"start": v(30, 27.15) * mm, "end": v(30, 25.15) * mm});
            skLineSegment(sketch, "E8.22.4.2", {"start": v(30, 25.15) * mm, "end": v(32, 25.15) * mm});
            skLineSegment(sketch, "E8.22.4.3", {"start": v(30, 27.15) * mm, "end": v(32, 27.15) * mm});
            skLineSegment(sketch, "E8.22.5.0", {"start": v(32, 23.15) * mm, "end": v(32, 21.15) * mm});
            skLineSegment(sketch, "E8.22.5.1", {"start": v(30, 23.15) * mm, "end": v(30, 21.15) * mm});
            skLineSegment(sketch, "E8.22.5.2", {"start": v(30, 21.15) * mm, "end": v(32, 21.15) * mm});
            skLineSegment(sketch, "E8.22.5.3", {"start": v(30, 23.15) * mm, "end": v(32, 23.15) * mm});
            skLineSegment(sketch, "E8.22.6.0", {"start": v(32, 19.15) * mm, "end": v(32, 17.15) * mm});
            skLineSegment(sketch, "E8.22.6.1", {"start": v(30, 19.15) * mm, "end": v(30, 17.15) * mm});
            skLineSegment(sketch, "E8.22.6.2", {"start": v(30, 17.15) * mm, "end": v(32, 17.15) * mm});
            skLineSegment(sketch, "E8.22.6.3", {"start": v(30, 19.15) * mm, "end": v(32, 19.15) * mm});
            skLineSegment(sketch, "E8.22.7.0", {"start": v(32, 15.15) * mm, "end": v(32, 13.15) * mm});
            skLineSegment(sketch, "E8.22.7.1", {"start": v(30, 15.15) * mm, "end": v(30, 13.15) * mm});
            skLineSegment(sketch, "E8.22.7.2", {"start": v(30, 13.15) * mm, "end": v(32, 13.15) * mm});
            skLineSegment(sketch, "E8.22.7.3", {"start": v(30, 15.15) * mm, "end": v(32, 15.15) * mm});
            skLineSegment(sketch, "E8.22.8.0", {"start": v(32, 11.15) * mm, "end": v(32, 9.15) * mm});
            skLineSegment(sketch, "E8.22.8.1", {"start": v(30, 11.15) * mm, "end": v(30, 9.15) * mm});
            skLineSegment(sketch, "E8.22.8.2", {"start": v(30, 9.15) * mm, "end": v(32, 9.15) * mm});
            skLineSegment(sketch, "E8.22.8.3", {"start": v(30, 11.15) * mm, "end": v(32, 11.15) * mm});
            skLineSegment(sketch, "E8.22.9.0", {"start": v(32, 7.15) * mm, "end": v(32, 5.15) * mm});
            skLineSegment(sketch, "E8.22.9.1", {"start": v(30, 7.15) * mm, "end": v(30, 5.15) * mm});
            skLineSegment(sketch, "E8.22.9.2", {"start": v(30, 5.15) * mm, "end": v(32, 5.15) * mm});
            skLineSegment(sketch, "E8.22.9.3", {"start": v(30, 7.15) * mm, "end": v(32, 7.15) * mm});
            skLineSegment(sketch, "E8.22.10.0", {"start": v(32, 3.15) * mm, "end": v(32, 1.15) * mm});
            skLineSegment(sketch, "E8.22.10.1", {"start": v(30, 3.15) * mm, "end": v(30, 1.15) * mm});
            skLineSegment(sketch, "E8.22.10.2", {"start": v(30, 1.15) * mm, "end": v(32, 1.15) * mm});
            skLineSegment(sketch, "E8.22.10.3", {"start": v(30, 3.15) * mm, "end": v(32, 3.15) * mm});
            skLineSegment(sketch, "E8.22.11.0", {"start": v(32, -0.85) * mm, "end": v(32, -2.85) * mm});
            skLineSegment(sketch, "E8.22.11.1", {"start": v(30, -0.85) * mm, "end": v(30, -2.85) * mm});
            skLineSegment(sketch, "E8.22.11.2", {"start": v(30, -2.85) * mm, "end": v(32, -2.85) * mm});
            skLineSegment(sketch, "E8.22.11.3", {"start": v(30, -0.85) * mm, "end": v(32, -0.85) * mm});
            skLineSegment(sketch, "E8.22.12.0", {"start": v(32, -4.85) * mm, "end": v(32, -6.85) * mm});
            skLineSegment(sketch, "E8.22.12.1", {"start": v(30, -4.85) * mm, "end": v(30, -6.85) * mm});
            skLineSegment(sketch, "E8.22.12.2", {"start": v(30, -6.85) * mm, "end": v(32, -6.85) * mm});
            skLineSegment(sketch, "E8.22.12.3", {"start": v(30, -4.85) * mm, "end": v(32, -4.85) * mm});
            skLineSegment(sketch, "E8.22.13.0", {"start": v(32, -8.85) * mm, "end": v(32, -10.85) * mm});
            skLineSegment(sketch, "E8.22.13.1", {"start": v(30, -8.85) * mm, "end": v(30, -10.85) * mm});
            skLineSegment(sketch, "E8.22.13.2", {"start": v(30, -10.85) * mm, "end": v(32, -10.85) * mm});
            skLineSegment(sketch, "E8.22.13.3", {"start": v(30, -8.85) * mm, "end": v(32, -8.85) * mm});
            skLineSegment(sketch, "E8.22.14.0", {"start": v(32, -12.85) * mm, "end": v(32, -14.85) * mm});
            skLineSegment(sketch, "E8.22.14.1", {"start": v(30, -12.85) * mm, "end": v(30, -14.85) * mm});
            skLineSegment(sketch, "E8.22.14.2", {"start": v(30, -14.85) * mm, "end": v(32, -14.85) * mm});
            skLineSegment(sketch, "E8.22.14.3", {"start": v(30, -12.85) * mm, "end": v(32, -12.85) * mm});
            skLineSegment(sketch, "E8.22.15.0", {"start": v(32, -16.85) * mm, "end": v(32, -18.85) * mm});
            skLineSegment(sketch, "E8.22.15.1", {"start": v(30, -16.85) * mm, "end": v(30, -18.85) * mm});
            skLineSegment(sketch, "E8.22.15.2", {"start": v(30, -18.85) * mm, "end": v(32, -18.85) * mm});
            skLineSegment(sketch, "E8.22.15.3", {"start": v(30, -16.85) * mm, "end": v(32, -16.85) * mm});
            skLineSegment(sketch, "E8.22.16.0", {"start": v(32, -20.85) * mm, "end": v(32, -22.85) * mm});
            skLineSegment(sketch, "E8.22.16.1", {"start": v(30, -20.85) * mm, "end": v(30, -22.85) * mm});
            skLineSegment(sketch, "E8.22.16.2", {"start": v(30, -22.85) * mm, "end": v(32, -22.85) * mm});
            skLineSegment(sketch, "E8.22.16.3", {"start": v(30, -20.85) * mm, "end": v(32, -20.85) * mm});
            skLineSegment(sketch, "E8.22.17.0", {"start": v(32, -24.85) * mm, "end": v(32, -26.85) * mm});
            skLineSegment(sketch, "E8.22.17.1", {"start": v(30, -24.85) * mm, "end": v(30, -26.85) * mm});
            skLineSegment(sketch, "E8.22.17.2", {"start": v(30, -26.85) * mm, "end": v(32, -26.85) * mm});
            skLineSegment(sketch, "E8.22.17.3", {"start": v(30, -24.85) * mm, "end": v(32, -24.85) * mm});
            skLineSegment(sketch, "E8.22.18.0", {"start": v(32, -28.85) * mm, "end": v(32, -30.85) * mm});
            skLineSegment(sketch, "E8.22.18.1", {"start": v(30, -28.85) * mm, "end": v(30, -30.85) * mm});
            skLineSegment(sketch, "E8.22.18.2", {"start": v(30, -30.85) * mm, "end": v(32, -30.85) * mm});
            skLineSegment(sketch, "E8.22.18.3", {"start": v(30, -28.85) * mm, "end": v(32, -28.85) * mm});
            skLineSegment(sketch, "E8.22.19.0", {"start": v(32, -32.85) * mm, "end": v(32, -34.85) * mm});
            skLineSegment(sketch, "E8.22.19.1", {"start": v(30, -32.85) * mm, "end": v(30, -34.85) * mm});
            skLineSegment(sketch, "E8.22.19.2", {"start": v(30, -34.85) * mm, "end": v(32, -34.85) * mm});
            skLineSegment(sketch, "E8.22.19.3", {"start": v(30, -32.85) * mm, "end": v(32, -32.85) * mm});
            skLineSegment(sketch, "E8.22.20.0", {"start": v(32, -36.85) * mm, "end": v(32, -38.85) * mm});
            skLineSegment(sketch, "E8.22.20.1", {"start": v(30, -36.85) * mm, "end": v(30, -38.85) * mm});
            skLineSegment(sketch, "E8.22.20.2", {"start": v(30, -38.85) * mm, "end": v(32, -38.85) * mm});
            skLineSegment(sketch, "E8.22.20.3", {"start": v(30, -36.85) * mm, "end": v(32, -36.85) * mm});
            skLineSegment(sketch, "E8.22.21.0", {"start": v(32, -40.85) * mm, "end": v(32, -42.85) * mm});
            skLineSegment(sketch, "E8.22.21.1", {"start": v(30, -40.85) * mm, "end": v(30, -42.85) * mm});
            skLineSegment(sketch, "E8.22.21.2", {"start": v(30, -42.85) * mm, "end": v(32, -42.85) * mm});
            skLineSegment(sketch, "E8.22.21.3", {"start": v(30, -40.85) * mm, "end": v(32, -40.85) * mm});
            skLineSegment(sketch, "E8.23.0.0", {"start": v(36, 43.15) * mm, "end": v(36, 41.15) * mm});
            skLineSegment(sketch, "E8.23.0.1", {"start": v(34, 43.15) * mm, "end": v(34, 41.15) * mm});
            skLineSegment(sketch, "E8.23.0.2", {"start": v(34, 41.15) * mm, "end": v(36, 41.15) * mm});
            skLineSegment(sketch, "E8.23.0.3", {"start": v(34, 43.15) * mm, "end": v(36, 43.15) * mm});
            skLineSegment(sketch, "E8.23.1.0", {"start": v(36, 39.15) * mm, "end": v(36, 37.15) * mm});
            skLineSegment(sketch, "E8.23.1.1", {"start": v(34, 39.15) * mm, "end": v(34, 37.15) * mm});
            skLineSegment(sketch, "E8.23.1.2", {"start": v(34, 37.15) * mm, "end": v(36, 37.15) * mm});
            skLineSegment(sketch, "E8.23.1.3", {"start": v(34, 39.15) * mm, "end": v(36, 39.15) * mm});
            skLineSegment(sketch, "E8.23.2.0", {"start": v(36, 35.15) * mm, "end": v(36, 33.15) * mm});
            skLineSegment(sketch, "E8.23.2.1", {"start": v(34, 35.15) * mm, "end": v(34, 33.15) * mm});
            skLineSegment(sketch, "E8.23.2.2", {"start": v(34, 33.15) * mm, "end": v(36, 33.15) * mm});
            skLineSegment(sketch, "E8.23.2.3", {"start": v(34, 35.15) * mm, "end": v(36, 35.15) * mm});
            skLineSegment(sketch, "E8.23.3.0", {"start": v(36, 31.15) * mm, "end": v(36, 29.15) * mm});
            skLineSegment(sketch, "E8.23.3.1", {"start": v(34, 31.15) * mm, "end": v(34, 29.15) * mm});
            skLineSegment(sketch, "E8.23.3.2", {"start": v(34, 29.15) * mm, "end": v(36, 29.15) * mm});
            skLineSegment(sketch, "E8.23.3.3", {"start": v(34, 31.15) * mm, "end": v(36, 31.15) * mm});
            skLineSegment(sketch, "E8.23.4.0", {"start": v(36, 27.15) * mm, "end": v(36, 25.15) * mm});
            skLineSegment(sketch, "E8.23.4.1", {"start": v(34, 27.15) * mm, "end": v(34, 25.15) * mm});
            skLineSegment(sketch, "E8.23.4.2", {"start": v(34, 25.15) * mm, "end": v(36, 25.15) * mm});
            skLineSegment(sketch, "E8.23.4.3", {"start": v(34, 27.15) * mm, "end": v(36, 27.15) * mm});
            skLineSegment(sketch, "E8.23.5.0", {"start": v(36, 23.15) * mm, "end": v(36, 21.15) * mm});
            skLineSegment(sketch, "E8.23.5.1", {"start": v(34, 23.15) * mm, "end": v(34, 21.15) * mm});
            skLineSegment(sketch, "E8.23.5.2", {"start": v(34, 21.15) * mm, "end": v(36, 21.15) * mm});
            skLineSegment(sketch, "E8.23.5.3", {"start": v(34, 23.15) * mm, "end": v(36, 23.15) * mm});
            skLineSegment(sketch, "E8.23.6.0", {"start": v(36, 19.15) * mm, "end": v(36, 17.15) * mm});
            skLineSegment(sketch, "E8.23.6.1", {"start": v(34, 19.15) * mm, "end": v(34, 17.15) * mm});
            skLineSegment(sketch, "E8.23.6.2", {"start": v(34, 17.15) * mm, "end": v(36, 17.15) * mm});
            skLineSegment(sketch, "E8.23.6.3", {"start": v(34, 19.15) * mm, "end": v(36, 19.15) * mm});
            skLineSegment(sketch, "E8.23.7.0", {"start": v(36, 15.15) * mm, "end": v(36, 13.15) * mm});
            skLineSegment(sketch, "E8.23.7.1", {"start": v(34, 15.15) * mm, "end": v(34, 13.15) * mm});
            skLineSegment(sketch, "E8.23.7.2", {"start": v(34, 13.15) * mm, "end": v(36, 13.15) * mm});
            skLineSegment(sketch, "E8.23.7.3", {"start": v(34, 15.15) * mm, "end": v(36, 15.15) * mm});
            skLineSegment(sketch, "E8.23.8.0", {"start": v(36, 11.15) * mm, "end": v(36, 9.15) * mm});
            skLineSegment(sketch, "E8.23.8.1", {"start": v(34, 11.15) * mm, "end": v(34, 9.15) * mm});
            skLineSegment(sketch, "E8.23.8.2", {"start": v(34, 9.15) * mm, "end": v(36, 9.15) * mm});
            skLineSegment(sketch, "E8.23.8.3", {"start": v(34, 11.15) * mm, "end": v(36, 11.15) * mm});
            skLineSegment(sketch, "E8.23.9.0", {"start": v(36, 7.15) * mm, "end": v(36, 5.15) * mm});
            skLineSegment(sketch, "E8.23.9.1", {"start": v(34, 7.15) * mm, "end": v(34, 5.15) * mm});
            skLineSegment(sketch, "E8.23.9.2", {"start": v(34, 5.15) * mm, "end": v(36, 5.15) * mm});
            skLineSegment(sketch, "E8.23.9.3", {"start": v(34, 7.15) * mm, "end": v(36, 7.15) * mm});
            skLineSegment(sketch, "E8.23.10.0", {"start": v(36, 3.15) * mm, "end": v(36, 1.15) * mm});
            skLineSegment(sketch, "E8.23.10.1", {"start": v(34, 3.15) * mm, "end": v(34, 1.15) * mm});
            skLineSegment(sketch, "E8.23.10.2", {"start": v(34, 1.15) * mm, "end": v(36, 1.15) * mm});
            skLineSegment(sketch, "E8.23.10.3", {"start": v(34, 3.15) * mm, "end": v(36, 3.15) * mm});
            skLineSegment(sketch, "E8.23.11.0", {"start": v(36, -0.85) * mm, "end": v(36, -2.85) * mm});
            skLineSegment(sketch, "E8.23.11.1", {"start": v(34, -0.85) * mm, "end": v(34, -2.85) * mm});
            skLineSegment(sketch, "E8.23.11.2", {"start": v(34, -2.85) * mm, "end": v(36, -2.85) * mm});
            skLineSegment(sketch, "E8.23.11.3", {"start": v(34, -0.85) * mm, "end": v(36, -0.85) * mm});
            skLineSegment(sketch, "E8.23.12.0", {"start": v(36, -4.85) * mm, "end": v(36, -6.85) * mm});
            skLineSegment(sketch, "E8.23.12.1", {"start": v(34, -4.85) * mm, "end": v(34, -6.85) * mm});
            skLineSegment(sketch, "E8.23.12.2", {"start": v(34, -6.85) * mm, "end": v(36, -6.85) * mm});
            skLineSegment(sketch, "E8.23.12.3", {"start": v(34, -4.85) * mm, "end": v(36, -4.85) * mm});
            skLineSegment(sketch, "E8.23.13.0", {"start": v(36, -8.85) * mm, "end": v(36, -10.85) * mm});
            skLineSegment(sketch, "E8.23.13.1", {"start": v(34, -8.85) * mm, "end": v(34, -10.85) * mm});
            skLineSegment(sketch, "E8.23.13.2", {"start": v(34, -10.85) * mm, "end": v(36, -10.85) * mm});
            skLineSegment(sketch, "E8.23.13.3", {"start": v(34, -8.85) * mm, "end": v(36, -8.85) * mm});
            skLineSegment(sketch, "E8.23.14.0", {"start": v(36, -12.85) * mm, "end": v(36, -14.85) * mm});
            skLineSegment(sketch, "E8.23.14.1", {"start": v(34, -12.85) * mm, "end": v(34, -14.85) * mm});
            skLineSegment(sketch, "E8.23.14.2", {"start": v(34, -14.85) * mm, "end": v(36, -14.85) * mm});
            skLineSegment(sketch, "E8.23.14.3", {"start": v(34, -12.85) * mm, "end": v(36, -12.85) * mm});
            skLineSegment(sketch, "E8.23.15.0", {"start": v(36, -16.85) * mm, "end": v(36, -18.85) * mm});
            skLineSegment(sketch, "E8.23.15.1", {"start": v(34, -16.85) * mm, "end": v(34, -18.85) * mm});
            skLineSegment(sketch, "E8.23.15.2", {"start": v(34, -18.85) * mm, "end": v(36, -18.85) * mm});
            skLineSegment(sketch, "E8.23.15.3", {"start": v(34, -16.85) * mm, "end": v(36, -16.85) * mm});
            skLineSegment(sketch, "E8.23.16.0", {"start": v(36, -20.85) * mm, "end": v(36, -22.85) * mm});
            skLineSegment(sketch, "E8.23.16.1", {"start": v(34, -20.85) * mm, "end": v(34, -22.85) * mm});
            skLineSegment(sketch, "E8.23.16.2", {"start": v(34, -22.85) * mm, "end": v(36, -22.85) * mm});
            skLineSegment(sketch, "E8.23.16.3", {"start": v(34, -20.85) * mm, "end": v(36, -20.85) * mm});
            skLineSegment(sketch, "E8.23.17.0", {"start": v(36, -24.85) * mm, "end": v(36, -26.85) * mm});
            skLineSegment(sketch, "E8.23.17.1", {"start": v(34, -24.85) * mm, "end": v(34, -26.85) * mm});
            skLineSegment(sketch, "E8.23.17.2", {"start": v(34, -26.85) * mm, "end": v(36, -26.85) * mm});
            skLineSegment(sketch, "E8.23.17.3", {"start": v(34, -24.85) * mm, "end": v(36, -24.85) * mm});
            skLineSegment(sketch, "E8.23.18.0", {"start": v(36, -28.85) * mm, "end": v(36, -30.85) * mm});
            skLineSegment(sketch, "E8.23.18.1", {"start": v(34, -28.85) * mm, "end": v(34, -30.85) * mm});
            skLineSegment(sketch, "E8.23.18.2", {"start": v(34, -30.85) * mm, "end": v(36, -30.85) * mm});
            skLineSegment(sketch, "E8.23.18.3", {"start": v(34, -28.85) * mm, "end": v(36, -28.85) * mm});
            skLineSegment(sketch, "E8.23.19.0", {"start": v(36, -32.85) * mm, "end": v(36, -34.85) * mm});
            skLineSegment(sketch, "E8.23.19.1", {"start": v(34, -32.85) * mm, "end": v(34, -34.85) * mm});
            skLineSegment(sketch, "E8.23.19.2", {"start": v(34, -34.85) * mm, "end": v(36, -34.85) * mm});
            skLineSegment(sketch, "E8.23.19.3", {"start": v(34, -32.85) * mm, "end": v(36, -32.85) * mm});
            skLineSegment(sketch, "E8.23.20.0", {"start": v(36, -36.85) * mm, "end": v(36, -38.85) * mm});
            skLineSegment(sketch, "E8.23.20.1", {"start": v(34, -36.85) * mm, "end": v(34, -38.85) * mm});
            skLineSegment(sketch, "E8.23.20.2", {"start": v(34, -38.85) * mm, "end": v(36, -38.85) * mm});
            skLineSegment(sketch, "E8.23.20.3", {"start": v(34, -36.85) * mm, "end": v(36, -36.85) * mm});
            skLineSegment(sketch, "E8.23.21.0", {"start": v(36, -40.85) * mm, "end": v(36, -42.85) * mm});
            skLineSegment(sketch, "E8.23.21.1", {"start": v(34, -40.85) * mm, "end": v(34, -42.85) * mm});
            skLineSegment(sketch, "E8.23.21.2", {"start": v(34, -42.85) * mm, "end": v(36, -42.85) * mm});
            skLineSegment(sketch, "E8.23.21.3", {"start": v(34, -40.85) * mm, "end": v(36, -40.85) * mm});
            skLineSegment(sketch, "E8.24.0.0", {"start": v(40, 43.15) * mm, "end": v(40, 41.15) * mm});
            skLineSegment(sketch, "E8.24.0.1", {"start": v(38, 43.15) * mm, "end": v(38, 41.15) * mm});
            skLineSegment(sketch, "E8.24.0.2", {"start": v(38, 41.15) * mm, "end": v(40, 41.15) * mm});
            skLineSegment(sketch, "E8.24.0.3", {"start": v(38, 43.15) * mm, "end": v(40, 43.15) * mm});
            skLineSegment(sketch, "E8.24.1.0", {"start": v(40, 39.15) * mm, "end": v(40, 37.15) * mm});
            skLineSegment(sketch, "E8.24.1.1", {"start": v(38, 39.15) * mm, "end": v(38, 37.15) * mm});
            skLineSegment(sketch, "E8.24.1.2", {"start": v(38, 37.15) * mm, "end": v(40, 37.15) * mm});
            skLineSegment(sketch, "E8.24.1.3", {"start": v(38, 39.15) * mm, "end": v(40, 39.15) * mm});
            skLineSegment(sketch, "E8.24.2.0", {"start": v(40, 35.15) * mm, "end": v(40, 33.15) * mm});
            skLineSegment(sketch, "E8.24.2.1", {"start": v(38, 35.15) * mm, "end": v(38, 33.15) * mm});
            skLineSegment(sketch, "E8.24.2.2", {"start": v(38, 33.15) * mm, "end": v(40, 33.15) * mm});
            skLineSegment(sketch, "E8.24.2.3", {"start": v(38, 35.15) * mm, "end": v(40, 35.15) * mm});
            skLineSegment(sketch, "E8.24.3.0", {"start": v(40, 31.15) * mm, "end": v(40, 29.15) * mm});
            skLineSegment(sketch, "E8.24.3.1", {"start": v(38, 31.15) * mm, "end": v(38, 29.15) * mm});
            skLineSegment(sketch, "E8.24.3.2", {"start": v(38, 29.15) * mm, "end": v(40, 29.15) * mm});
            skLineSegment(sketch, "E8.24.3.3", {"start": v(38, 31.15) * mm, "end": v(40, 31.15) * mm});
            skLineSegment(sketch, "E8.24.4.0", {"start": v(40, 27.15) * mm, "end": v(40, 25.15) * mm});
            skLineSegment(sketch, "E8.24.4.1", {"start": v(38, 27.15) * mm, "end": v(38, 25.15) * mm});
            skLineSegment(sketch, "E8.24.4.2", {"start": v(38, 25.15) * mm, "end": v(40, 25.15) * mm});
            skLineSegment(sketch, "E8.24.4.3", {"start": v(38, 27.15) * mm, "end": v(40, 27.15) * mm});
            skLineSegment(sketch, "E8.24.5.0", {"start": v(40, 23.15) * mm, "end": v(40, 21.15) * mm});
            skLineSegment(sketch, "E8.24.5.1", {"start": v(38, 23.15) * mm, "end": v(38, 21.15) * mm});
            skLineSegment(sketch, "E8.24.5.2", {"start": v(38, 21.15) * mm, "end": v(40, 21.15) * mm});
            skLineSegment(sketch, "E8.24.5.3", {"start": v(38, 23.15) * mm, "end": v(40, 23.15) * mm});
            skLineSegment(sketch, "E8.24.6.0", {"start": v(40, 19.15) * mm, "end": v(40, 17.15) * mm});
            skLineSegment(sketch, "E8.24.6.1", {"start": v(38, 19.15) * mm, "end": v(38, 17.15) * mm});
            skLineSegment(sketch, "E8.24.6.2", {"start": v(38, 17.15) * mm, "end": v(40, 17.15) * mm});
            skLineSegment(sketch, "E8.24.6.3", {"start": v(38, 19.15) * mm, "end": v(40, 19.15) * mm});
            skLineSegment(sketch, "E8.24.7.0", {"start": v(40, 15.15) * mm, "end": v(40, 13.15) * mm});
            skLineSegment(sketch, "E8.24.7.1", {"start": v(38, 15.15) * mm, "end": v(38, 13.15) * mm});
            skLineSegment(sketch, "E8.24.7.2", {"start": v(38, 13.15) * mm, "end": v(40, 13.15) * mm});
            skLineSegment(sketch, "E8.24.7.3", {"start": v(38, 15.15) * mm, "end": v(40, 15.15) * mm});
            skLineSegment(sketch, "E8.24.8.0", {"start": v(40, 11.15) * mm, "end": v(40, 9.15) * mm});
            skLineSegment(sketch, "E8.24.8.1", {"start": v(38, 11.15) * mm, "end": v(38, 9.15) * mm});
            skLineSegment(sketch, "E8.24.8.2", {"start": v(38, 9.15) * mm, "end": v(40, 9.15) * mm});
            skLineSegment(sketch, "E8.24.8.3", {"start": v(38, 11.15) * mm, "end": v(40, 11.15) * mm});
            skLineSegment(sketch, "E8.24.9.0", {"start": v(40, 7.15) * mm, "end": v(40, 5.15) * mm});
            skLineSegment(sketch, "E8.24.9.1", {"start": v(38, 7.15) * mm, "end": v(38, 5.15) * mm});
            skLineSegment(sketch, "E8.24.9.2", {"start": v(38, 5.15) * mm, "end": v(40, 5.15) * mm});
            skLineSegment(sketch, "E8.24.9.3", {"start": v(38, 7.15) * mm, "end": v(40, 7.15) * mm});
            skLineSegment(sketch, "E8.24.10.0", {"start": v(40, 3.15) * mm, "end": v(40, 1.15) * mm});
            skLineSegment(sketch, "E8.24.10.1", {"start": v(38, 3.15) * mm, "end": v(38, 1.15) * mm});
            skLineSegment(sketch, "E8.24.10.2", {"start": v(38, 1.15) * mm, "end": v(40, 1.15) * mm});
            skLineSegment(sketch, "E8.24.10.3", {"start": v(38, 3.15) * mm, "end": v(40, 3.15) * mm});
            skLineSegment(sketch, "E8.24.11.0", {"start": v(40, -0.85) * mm, "end": v(40, -2.85) * mm});
            skLineSegment(sketch, "E8.24.11.1", {"start": v(38, -0.85) * mm, "end": v(38, -2.85) * mm});
            skLineSegment(sketch, "E8.24.11.2", {"start": v(38, -2.85) * mm, "end": v(40, -2.85) * mm});
            skLineSegment(sketch, "E8.24.11.3", {"start": v(38, -0.85) * mm, "end": v(40, -0.85) * mm});
            skLineSegment(sketch, "E8.24.12.0", {"start": v(40, -4.85) * mm, "end": v(40, -6.85) * mm});
            skLineSegment(sketch, "E8.24.12.1", {"start": v(38, -4.85) * mm, "end": v(38, -6.85) * mm});
            skLineSegment(sketch, "E8.24.12.2", {"start": v(38, -6.85) * mm, "end": v(40, -6.85) * mm});
            skLineSegment(sketch, "E8.24.12.3", {"start": v(38, -4.85) * mm, "end": v(40, -4.85) * mm});
            skLineSegment(sketch, "E8.24.13.0", {"start": v(40, -8.85) * mm, "end": v(40, -10.85) * mm});
            skLineSegment(sketch, "E8.24.13.1", {"start": v(38, -8.85) * mm, "end": v(38, -10.85) * mm});
            skLineSegment(sketch, "E8.24.13.2", {"start": v(38, -10.85) * mm, "end": v(40, -10.85) * mm});
            skLineSegment(sketch, "E8.24.13.3", {"start": v(38, -8.85) * mm, "end": v(40, -8.85) * mm});
            skLineSegment(sketch, "E8.24.14.0", {"start": v(40, -12.85) * mm, "end": v(40, -14.85) * mm});
            skLineSegment(sketch, "E8.24.14.1", {"start": v(38, -12.85) * mm, "end": v(38, -14.85) * mm});
            skLineSegment(sketch, "E8.24.14.2", {"start": v(38, -14.85) * mm, "end": v(40, -14.85) * mm});
            skLineSegment(sketch, "E8.24.14.3", {"start": v(38, -12.85) * mm, "end": v(40, -12.85) * mm});
            skLineSegment(sketch, "E8.24.15.0", {"start": v(40, -16.85) * mm, "end": v(40, -18.85) * mm});
            skLineSegment(sketch, "E8.24.15.1", {"start": v(38, -16.85) * mm, "end": v(38, -18.85) * mm});
            skLineSegment(sketch, "E8.24.15.2", {"start": v(38, -18.85) * mm, "end": v(40, -18.85) * mm});
            skLineSegment(sketch, "E8.24.15.3", {"start": v(38, -16.85) * mm, "end": v(40, -16.85) * mm});
            skLineSegment(sketch, "E8.24.16.0", {"start": v(40, -20.85) * mm, "end": v(40, -22.85) * mm});
            skLineSegment(sketch, "E8.24.16.1", {"start": v(38, -20.85) * mm, "end": v(38, -22.85) * mm});
            skLineSegment(sketch, "E8.24.16.2", {"start": v(38, -22.85) * mm, "end": v(40, -22.85) * mm});
            skLineSegment(sketch, "E8.24.16.3", {"start": v(38, -20.85) * mm, "end": v(40, -20.85) * mm});
            skLineSegment(sketch, "E8.24.17.0", {"start": v(40, -24.85) * mm, "end": v(40, -26.85) * mm});
            skLineSegment(sketch, "E8.24.17.1", {"start": v(38, -24.85) * mm, "end": v(38, -26.85) * mm});
            skLineSegment(sketch, "E8.24.17.2", {"start": v(38, -26.85) * mm, "end": v(40, -26.85) * mm});
            skLineSegment(sketch, "E8.24.17.3", {"start": v(38, -24.85) * mm, "end": v(40, -24.85) * mm});
            skLineSegment(sketch, "E8.24.18.0", {"start": v(40, -28.85) * mm, "end": v(40, -30.85) * mm});
            skLineSegment(sketch, "E8.24.18.1", {"start": v(38, -28.85) * mm, "end": v(38, -30.85) * mm});
            skLineSegment(sketch, "E8.24.18.2", {"start": v(38, -30.85) * mm, "end": v(40, -30.85) * mm});
            skLineSegment(sketch, "E8.24.18.3", {"start": v(38, -28.85) * mm, "end": v(40, -28.85) * mm});
            skLineSegment(sketch, "E8.24.19.0", {"start": v(40, -32.85) * mm, "end": v(40, -34.85) * mm});
            skLineSegment(sketch, "E8.24.19.1", {"start": v(38, -32.85) * mm, "end": v(38, -34.85) * mm});
            skLineSegment(sketch, "E8.24.19.2", {"start": v(38, -34.85) * mm, "end": v(40, -34.85) * mm});
            skLineSegment(sketch, "E8.24.19.3", {"start": v(38, -32.85) * mm, "end": v(40, -32.85) * mm});
            skLineSegment(sketch, "E8.24.20.0", {"start": v(40, -36.85) * mm, "end": v(40, -38.85) * mm});
            skLineSegment(sketch, "E8.24.20.1", {"start": v(38, -36.85) * mm, "end": v(38, -38.85) * mm});
            skLineSegment(sketch, "E8.24.20.2", {"start": v(38, -38.85) * mm, "end": v(40, -38.85) * mm});
            skLineSegment(sketch, "E8.24.20.3", {"start": v(38, -36.85) * mm, "end": v(40, -36.85) * mm});
            skLineSegment(sketch, "E8.24.21.0", {"start": v(40, -40.85) * mm, "end": v(40, -42.85) * mm});
            skLineSegment(sketch, "E8.24.21.1", {"start": v(38, -40.85) * mm, "end": v(38, -42.85) * mm});
            skLineSegment(sketch, "E8.24.21.2", {"start": v(38, -42.85) * mm, "end": v(40, -42.85) * mm});
            skLineSegment(sketch, "E8.24.21.3", {"start": v(38, -40.85) * mm, "end": v(40, -40.85) * mm});
            skLineSegment(sketch, "E8.25.0.0", {"start": v(44, 43.15) * mm, "end": v(44, 41.15) * mm});
            skLineSegment(sketch, "E8.25.0.1", {"start": v(42, 43.15) * mm, "end": v(42, 41.15) * mm});
            skLineSegment(sketch, "E8.25.0.2", {"start": v(42, 41.15) * mm, "end": v(44, 41.15) * mm});
            skLineSegment(sketch, "E8.25.0.3", {"start": v(42, 43.15) * mm, "end": v(44, 43.15) * mm});
            skLineSegment(sketch, "E8.25.1.0", {"start": v(44, 39.15) * mm, "end": v(44, 37.15) * mm});
            skLineSegment(sketch, "E8.25.1.1", {"start": v(42, 39.15) * mm, "end": v(42, 37.15) * mm});
            skLineSegment(sketch, "E8.25.1.2", {"start": v(42, 37.15) * mm, "end": v(44, 37.15) * mm});
            skLineSegment(sketch, "E8.25.1.3", {"start": v(42, 39.15) * mm, "end": v(44, 39.15) * mm});
            skLineSegment(sketch, "E8.25.2.0", {"start": v(44, 35.15) * mm, "end": v(44, 33.15) * mm});
            skLineSegment(sketch, "E8.25.2.1", {"start": v(42, 35.15) * mm, "end": v(42, 33.15) * mm});
            skLineSegment(sketch, "E8.25.2.2", {"start": v(42, 33.15) * mm, "end": v(44, 33.15) * mm});
            skLineSegment(sketch, "E8.25.2.3", {"start": v(42, 35.15) * mm, "end": v(44, 35.15) * mm});
            skLineSegment(sketch, "E8.25.3.0", {"start": v(44, 31.15) * mm, "end": v(44, 29.15) * mm});
            skLineSegment(sketch, "E8.25.3.1", {"start": v(42, 31.15) * mm, "end": v(42, 29.15) * mm});
            skLineSegment(sketch, "E8.25.3.2", {"start": v(42, 29.15) * mm, "end": v(44, 29.15) * mm});
            skLineSegment(sketch, "E8.25.3.3", {"start": v(42, 31.15) * mm, "end": v(44, 31.15) * mm});
            skLineSegment(sketch, "E8.25.4.0", {"start": v(44, 27.15) * mm, "end": v(44, 25.15) * mm});
            skLineSegment(sketch, "E8.25.4.1", {"start": v(42, 27.15) * mm, "end": v(42, 25.15) * mm});
            skLineSegment(sketch, "E8.25.4.2", {"start": v(42, 25.15) * mm, "end": v(44, 25.15) * mm});
            skLineSegment(sketch, "E8.25.4.3", {"start": v(42, 27.15) * mm, "end": v(44, 27.15) * mm});
            skLineSegment(sketch, "E8.25.5.0", {"start": v(44, 23.15) * mm, "end": v(44, 21.15) * mm});
            skLineSegment(sketch, "E8.25.5.1", {"start": v(42, 23.15) * mm, "end": v(42, 21.15) * mm});
            skLineSegment(sketch, "E8.25.5.2", {"start": v(42, 21.15) * mm, "end": v(44, 21.15) * mm});
            skLineSegment(sketch, "E8.25.5.3", {"start": v(42, 23.15) * mm, "end": v(44, 23.15) * mm});
            skLineSegment(sketch, "E8.25.6.0", {"start": v(44, 19.15) * mm, "end": v(44, 17.15) * mm});
            skLineSegment(sketch, "E8.25.6.1", {"start": v(42, 19.15) * mm, "end": v(42, 17.15) * mm});
            skLineSegment(sketch, "E8.25.6.2", {"start": v(42, 17.15) * mm, "end": v(44, 17.15) * mm});
            skLineSegment(sketch, "E8.25.6.3", {"start": v(42, 19.15) * mm, "end": v(44, 19.15) * mm});
            skLineSegment(sketch, "E8.25.7.0", {"start": v(44, 15.15) * mm, "end": v(44, 13.15) * mm});
            skLineSegment(sketch, "E8.25.7.1", {"start": v(42, 15.15) * mm, "end": v(42, 13.15) * mm});
            skLineSegment(sketch, "E8.25.7.2", {"start": v(42, 13.15) * mm, "end": v(44, 13.15) * mm});
            skLineSegment(sketch, "E8.25.7.3", {"start": v(42, 15.15) * mm, "end": v(44, 15.15) * mm});
            skLineSegment(sketch, "E8.25.8.0", {"start": v(44, 11.15) * mm, "end": v(44, 9.15) * mm});
            skLineSegment(sketch, "E8.25.8.1", {"start": v(42, 11.15) * mm, "end": v(42, 9.15) * mm});
            skLineSegment(sketch, "E8.25.8.2", {"start": v(42, 9.15) * mm, "end": v(44, 9.15) * mm});
            skLineSegment(sketch, "E8.25.8.3", {"start": v(42, 11.15) * mm, "end": v(44, 11.15) * mm});
            skLineSegment(sketch, "E8.25.9.0", {"start": v(44, 7.15) * mm, "end": v(44, 5.15) * mm});
            skLineSegment(sketch, "E8.25.9.1", {"start": v(42, 7.15) * mm, "end": v(42, 5.15) * mm});
            skLineSegment(sketch, "E8.25.9.2", {"start": v(42, 5.15) * mm, "end": v(44, 5.15) * mm});
            skLineSegment(sketch, "E8.25.9.3", {"start": v(42, 7.15) * mm, "end": v(44, 7.15) * mm});
            skLineSegment(sketch, "E8.25.10.0", {"start": v(44, 3.15) * mm, "end": v(44, 1.15) * mm});
            skLineSegment(sketch, "E8.25.10.1", {"start": v(42, 3.15) * mm, "end": v(42, 1.15) * mm});
            skLineSegment(sketch, "E8.25.10.2", {"start": v(42, 1.15) * mm, "end": v(44, 1.15) * mm});
            skLineSegment(sketch, "E8.25.10.3", {"start": v(42, 3.15) * mm, "end": v(44, 3.15) * mm});
            skLineSegment(sketch, "E8.25.11.0", {"start": v(44, -0.85) * mm, "end": v(44, -2.85) * mm});
            skLineSegment(sketch, "E8.25.11.1", {"start": v(42, -0.85) * mm, "end": v(42, -2.85) * mm});
            skLineSegment(sketch, "E8.25.11.2", {"start": v(42, -2.85) * mm, "end": v(44, -2.85) * mm});
            skLineSegment(sketch, "E8.25.11.3", {"start": v(42, -0.85) * mm, "end": v(44, -0.85) * mm});
            skLineSegment(sketch, "E8.25.12.0", {"start": v(44, -4.85) * mm, "end": v(44, -6.85) * mm});
            skLineSegment(sketch, "E8.25.12.1", {"start": v(42, -4.85) * mm, "end": v(42, -6.85) * mm});
            skLineSegment(sketch, "E8.25.12.2", {"start": v(42, -6.85) * mm, "end": v(44, -6.85) * mm});
            skLineSegment(sketch, "E8.25.12.3", {"start": v(42, -4.85) * mm, "end": v(44, -4.85) * mm});
            skLineSegment(sketch, "E8.25.13.0", {"start": v(44, -8.85) * mm, "end": v(44, -10.85) * mm});
            skLineSegment(sketch, "E8.25.13.1", {"start": v(42, -8.85) * mm, "end": v(42, -10.85) * mm});
            skLineSegment(sketch, "E8.25.13.2", {"start": v(42, -10.85) * mm, "end": v(44, -10.85) * mm});
            skLineSegment(sketch, "E8.25.13.3", {"start": v(42, -8.85) * mm, "end": v(44, -8.85) * mm});
            skLineSegment(sketch, "E8.25.14.0", {"start": v(44, -12.85) * mm, "end": v(44, -14.85) * mm});
            skLineSegment(sketch, "E8.25.14.1", {"start": v(42, -12.85) * mm, "end": v(42, -14.85) * mm});
            skLineSegment(sketch, "E8.25.14.2", {"start": v(42, -14.85) * mm, "end": v(44, -14.85) * mm});
            skLineSegment(sketch, "E8.25.14.3", {"start": v(42, -12.85) * mm, "end": v(44, -12.85) * mm});
            skLineSegment(sketch, "E8.25.15.0", {"start": v(44, -16.85) * mm, "end": v(44, -18.85) * mm});
            skLineSegment(sketch, "E8.25.15.1", {"start": v(42, -16.85) * mm, "end": v(42, -18.85) * mm});
            skLineSegment(sketch, "E8.25.15.2", {"start": v(42, -18.85) * mm, "end": v(44, -18.85) * mm});
            skLineSegment(sketch, "E8.25.15.3", {"start": v(42, -16.85) * mm, "end": v(44, -16.85) * mm});
            skLineSegment(sketch, "E8.25.16.0", {"start": v(44, -20.85) * mm, "end": v(44, -22.85) * mm});
            skLineSegment(sketch, "E8.25.16.1", {"start": v(42, -20.85) * mm, "end": v(42, -22.85) * mm});
            skLineSegment(sketch, "E8.25.16.2", {"start": v(42, -22.85) * mm, "end": v(44, -22.85) * mm});
            skLineSegment(sketch, "E8.25.16.3", {"start": v(42, -20.85) * mm, "end": v(44, -20.85) * mm});
            skLineSegment(sketch, "E8.25.17.0", {"start": v(44, -24.85) * mm, "end": v(44, -26.85) * mm});
            skLineSegment(sketch, "E8.25.17.1", {"start": v(42, -24.85) * mm, "end": v(42, -26.85) * mm});
            skLineSegment(sketch, "E8.25.17.2", {"start": v(42, -26.85) * mm, "end": v(44, -26.85) * mm});
            skLineSegment(sketch, "E8.25.17.3", {"start": v(42, -24.85) * mm, "end": v(44, -24.85) * mm});
            skLineSegment(sketch, "E8.25.18.0", {"start": v(44, -28.85) * mm, "end": v(44, -30.85) * mm});
            skLineSegment(sketch, "E8.25.18.1", {"start": v(42, -28.85) * mm, "end": v(42, -30.85) * mm});
            skLineSegment(sketch, "E8.25.18.2", {"start": v(42, -30.85) * mm, "end": v(44, -30.85) * mm});
            skLineSegment(sketch, "E8.25.18.3", {"start": v(42, -28.85) * mm, "end": v(44, -28.85) * mm});
            skLineSegment(sketch, "E8.25.19.0", {"start": v(44, -32.85) * mm, "end": v(44, -34.85) * mm});
            skLineSegment(sketch, "E8.25.19.1", {"start": v(42, -32.85) * mm, "end": v(42, -34.85) * mm});
            skLineSegment(sketch, "E8.25.19.2", {"start": v(42, -34.85) * mm, "end": v(44, -34.85) * mm});
            skLineSegment(sketch, "E8.25.19.3", {"start": v(42, -32.85) * mm, "end": v(44, -32.85) * mm});
            skLineSegment(sketch, "E8.25.20.0", {"start": v(44, -36.85) * mm, "end": v(44, -38.85) * mm});
            skLineSegment(sketch, "E8.25.20.1", {"start": v(42, -36.85) * mm, "end": v(42, -38.85) * mm});
            skLineSegment(sketch, "E8.25.20.2", {"start": v(42, -38.85) * mm, "end": v(44, -38.85) * mm});
            skLineSegment(sketch, "E8.25.20.3", {"start": v(42, -36.85) * mm, "end": v(44, -36.85) * mm});
            skLineSegment(sketch, "E8.25.21.0", {"start": v(44, -40.85) * mm, "end": v(44, -42.85) * mm});
            skLineSegment(sketch, "E8.25.21.1", {"start": v(42, -40.85) * mm, "end": v(42, -42.85) * mm});
            skLineSegment(sketch, "E8.25.21.2", {"start": v(42, -42.85) * mm, "end": v(44, -42.85) * mm});
            skLineSegment(sketch, "E8.25.21.3", {"start": v(42, -40.85) * mm, "end": v(44, -40.85) * mm});
            skLineSegment(sketch, "E8.26.0.0", {"start": v(48, 43.15) * mm, "end": v(48, 41.15) * mm});
            skLineSegment(sketch, "E8.26.0.1", {"start": v(46, 43.15) * mm, "end": v(46, 41.15) * mm});
            skLineSegment(sketch, "E8.26.0.2", {"start": v(46, 41.15) * mm, "end": v(48, 41.15) * mm});
            skLineSegment(sketch, "E8.26.0.3", {"start": v(46, 43.15) * mm, "end": v(48, 43.15) * mm});
            skLineSegment(sketch, "E8.26.1.0", {"start": v(48, 39.15) * mm, "end": v(48, 37.15) * mm});
            skLineSegment(sketch, "E8.26.1.1", {"start": v(46, 39.15) * mm, "end": v(46, 37.15) * mm});
            skLineSegment(sketch, "E8.26.1.2", {"start": v(46, 37.15) * mm, "end": v(48, 37.15) * mm});
            skLineSegment(sketch, "E8.26.1.3", {"start": v(46, 39.15) * mm, "end": v(48, 39.15) * mm});
            skLineSegment(sketch, "E8.26.2.0", {"start": v(48, 35.15) * mm, "end": v(48, 33.15) * mm});
            skLineSegment(sketch, "E8.26.2.1", {"start": v(46, 35.15) * mm, "end": v(46, 33.15) * mm});
            skLineSegment(sketch, "E8.26.2.2", {"start": v(46, 33.15) * mm, "end": v(48, 33.15) * mm});
            skLineSegment(sketch, "E8.26.2.3", {"start": v(46, 35.15) * mm, "end": v(48, 35.15) * mm});
            skLineSegment(sketch, "E8.26.3.0", {"start": v(48, 31.15) * mm, "end": v(48, 29.15) * mm});
            skLineSegment(sketch, "E8.26.3.1", {"start": v(46, 31.15) * mm, "end": v(46, 29.15) * mm});
            skLineSegment(sketch, "E8.26.3.2", {"start": v(46, 29.15) * mm, "end": v(48, 29.15) * mm});
            skLineSegment(sketch, "E8.26.3.3", {"start": v(46, 31.15) * mm, "end": v(48, 31.15) * mm});
            skLineSegment(sketch, "E8.26.4.0", {"start": v(48, 27.15) * mm, "end": v(48, 25.15) * mm});
            skLineSegment(sketch, "E8.26.4.1", {"start": v(46, 27.15) * mm, "end": v(46, 25.15) * mm});
            skLineSegment(sketch, "E8.26.4.2", {"start": v(46, 25.15) * mm, "end": v(48, 25.15) * mm});
            skLineSegment(sketch, "E8.26.4.3", {"start": v(46, 27.15) * mm, "end": v(48, 27.15) * mm});
            skLineSegment(sketch, "E8.26.5.0", {"start": v(48, 23.15) * mm, "end": v(48, 21.15) * mm});
            skLineSegment(sketch, "E8.26.5.1", {"start": v(46, 23.15) * mm, "end": v(46, 21.15) * mm});
            skLineSegment(sketch, "E8.26.5.2", {"start": v(46, 21.15) * mm, "end": v(48, 21.15) * mm});
            skLineSegment(sketch, "E8.26.5.3", {"start": v(46, 23.15) * mm, "end": v(48, 23.15) * mm});
            skLineSegment(sketch, "E8.26.6.0", {"start": v(48, 19.15) * mm, "end": v(48, 17.15) * mm});
            skLineSegment(sketch, "E8.26.6.1", {"start": v(46, 19.15) * mm, "end": v(46, 17.15) * mm});
            skLineSegment(sketch, "E8.26.6.2", {"start": v(46, 17.15) * mm, "end": v(48, 17.15) * mm});
            skLineSegment(sketch, "E8.26.6.3", {"start": v(46, 19.15) * mm, "end": v(48, 19.15) * mm});
            skLineSegment(sketch, "E8.26.7.0", {"start": v(48, 15.15) * mm, "end": v(48, 13.15) * mm});
            skLineSegment(sketch, "E8.26.7.1", {"start": v(46, 15.15) * mm, "end": v(46, 13.15) * mm});
            skLineSegment(sketch, "E8.26.7.2", {"start": v(46, 13.15) * mm, "end": v(48, 13.15) * mm});
            skLineSegment(sketch, "E8.26.7.3", {"start": v(46, 15.15) * mm, "end": v(48, 15.15) * mm});
            skLineSegment(sketch, "E8.26.8.0", {"start": v(48, 11.15) * mm, "end": v(48, 9.15) * mm});
            skLineSegment(sketch, "E8.26.8.1", {"start": v(46, 11.15) * mm, "end": v(46, 9.15) * mm});
            skLineSegment(sketch, "E8.26.8.2", {"start": v(46, 9.15) * mm, "end": v(48, 9.15) * mm});
            skLineSegment(sketch, "E8.26.8.3", {"start": v(46, 11.15) * mm, "end": v(48, 11.15) * mm});
            skLineSegment(sketch, "E8.26.9.0", {"start": v(48, 7.15) * mm, "end": v(48, 5.15) * mm});
            skLineSegment(sketch, "E8.26.9.1", {"start": v(46, 7.15) * mm, "end": v(46, 5.15) * mm});
            skLineSegment(sketch, "E8.26.9.2", {"start": v(46, 5.15) * mm, "end": v(48, 5.15) * mm});
            skLineSegment(sketch, "E8.26.9.3", {"start": v(46, 7.15) * mm, "end": v(48, 7.15) * mm});
            skLineSegment(sketch, "E8.26.10.0", {"start": v(48, 3.15) * mm, "end": v(48, 1.15) * mm});
            skLineSegment(sketch, "E8.26.10.1", {"start": v(46, 3.15) * mm, "end": v(46, 1.15) * mm});
            skLineSegment(sketch, "E8.26.10.2", {"start": v(46, 1.15) * mm, "end": v(48, 1.15) * mm});
            skLineSegment(sketch, "E8.26.10.3", {"start": v(46, 3.15) * mm, "end": v(48, 3.15) * mm});
            skLineSegment(sketch, "E8.26.11.0", {"start": v(48, -0.85) * mm, "end": v(48, -2.85) * mm});
            skLineSegment(sketch, "E8.26.11.1", {"start": v(46, -0.85) * mm, "end": v(46, -2.85) * mm});
            skLineSegment(sketch, "E8.26.11.2", {"start": v(46, -2.85) * mm, "end": v(48, -2.85) * mm});
            skLineSegment(sketch, "E8.26.11.3", {"start": v(46, -0.85) * mm, "end": v(48, -0.85) * mm});
            skLineSegment(sketch, "E8.26.12.0", {"start": v(48, -4.85) * mm, "end": v(48, -6.85) * mm});
            skLineSegment(sketch, "E8.26.12.1", {"start": v(46, -4.85) * mm, "end": v(46, -6.85) * mm});
            skLineSegment(sketch, "E8.26.12.2", {"start": v(46, -6.85) * mm, "end": v(48, -6.85) * mm});
            skLineSegment(sketch, "E8.26.12.3", {"start": v(46, -4.85) * mm, "end": v(48, -4.85) * mm});
            skLineSegment(sketch, "E8.26.13.0", {"start": v(48, -8.85) * mm, "end": v(48, -10.85) * mm});
            skLineSegment(sketch, "E8.26.13.1", {"start": v(46, -8.85) * mm, "end": v(46, -10.85) * mm});
            skLineSegment(sketch, "E8.26.13.2", {"start": v(46, -10.85) * mm, "end": v(48, -10.85) * mm});
            skLineSegment(sketch, "E8.26.13.3", {"start": v(46, -8.85) * mm, "end": v(48, -8.85) * mm});
            skLineSegment(sketch, "E8.26.14.0", {"start": v(48, -12.85) * mm, "end": v(48, -14.85) * mm});
            skLineSegment(sketch, "E8.26.14.1", {"start": v(46, -12.85) * mm, "end": v(46, -14.85) * mm});
            skLineSegment(sketch, "E8.26.14.2", {"start": v(46, -14.85) * mm, "end": v(48, -14.85) * mm});
            skLineSegment(sketch, "E8.26.14.3", {"start": v(46, -12.85) * mm, "end": v(48, -12.85) * mm});
            skLineSegment(sketch, "E8.26.15.0", {"start": v(48, -16.85) * mm, "end": v(48, -18.85) * mm});
            skLineSegment(sketch, "E8.26.15.1", {"start": v(46, -16.85) * mm, "end": v(46, -18.85) * mm});
            skLineSegment(sketch, "E8.26.15.2", {"start": v(46, -18.85) * mm, "end": v(48, -18.85) * mm});
            skLineSegment(sketch, "E8.26.15.3", {"start": v(46, -16.85) * mm, "end": v(48, -16.85) * mm});
            skLineSegment(sketch, "E8.26.16.0", {"start": v(48, -20.85) * mm, "end": v(48, -22.85) * mm});
            skLineSegment(sketch, "E8.26.16.1", {"start": v(46, -20.85) * mm, "end": v(46, -22.85) * mm});
            skLineSegment(sketch, "E8.26.16.2", {"start": v(46, -22.85) * mm, "end": v(48, -22.85) * mm});
            skLineSegment(sketch, "E8.26.16.3", {"start": v(46, -20.85) * mm, "end": v(48, -20.85) * mm});
            skLineSegment(sketch, "E8.26.17.0", {"start": v(48, -24.85) * mm, "end": v(48, -26.85) * mm});
            skLineSegment(sketch, "E8.26.17.1", {"start": v(46, -24.85) * mm, "end": v(46, -26.85) * mm});
            skLineSegment(sketch, "E8.26.17.2", {"start": v(46, -26.85) * mm, "end": v(48, -26.85) * mm});
            skLineSegment(sketch, "E8.26.17.3", {"start": v(46, -24.85) * mm, "end": v(48, -24.85) * mm});
            skLineSegment(sketch, "E8.26.18.0", {"start": v(48, -28.85) * mm, "end": v(48, -30.85) * mm});
            skLineSegment(sketch, "E8.26.18.1", {"start": v(46, -28.85) * mm, "end": v(46, -30.85) * mm});
            skLineSegment(sketch, "E8.26.18.2", {"start": v(46, -30.85) * mm, "end": v(48, -30.85) * mm});
            skLineSegment(sketch, "E8.26.18.3", {"start": v(46, -28.85) * mm, "end": v(48, -28.85) * mm});
            skLineSegment(sketch, "E8.26.19.0", {"start": v(48, -32.85) * mm, "end": v(48, -34.85) * mm});
            skLineSegment(sketch, "E8.26.19.1", {"start": v(46, -32.85) * mm, "end": v(46, -34.85) * mm});
            skLineSegment(sketch, "E8.26.19.2", {"start": v(46, -34.85) * mm, "end": v(48, -34.85) * mm});
            skLineSegment(sketch, "E8.26.19.3", {"start": v(46, -32.85) * mm, "end": v(48, -32.85) * mm});
            skLineSegment(sketch, "E8.26.20.0", {"start": v(48, -36.85) * mm, "end": v(48, -38.85) * mm});
            skLineSegment(sketch, "E8.26.20.1", {"start": v(46, -36.85) * mm, "end": v(46, -38.85) * mm});
            skLineSegment(sketch, "E8.26.20.2", {"start": v(46, -38.85) * mm, "end": v(48, -38.85) * mm});
            skLineSegment(sketch, "E8.26.20.3", {"start": v(46, -36.85) * mm, "end": v(48, -36.85) * mm});
            skLineSegment(sketch, "E8.26.21.0", {"start": v(48, -40.85) * mm, "end": v(48, -42.85) * mm});
            skLineSegment(sketch, "E8.26.21.1", {"start": v(46, -40.85) * mm, "end": v(46, -42.85) * mm});
            skLineSegment(sketch, "E8.26.21.2", {"start": v(46, -42.85) * mm, "end": v(48, -42.85) * mm});
            skLineSegment(sketch, "E8.26.21.3", {"start": v(46, -40.85) * mm, "end": v(48, -40.85) * mm});
            skLineSegment(sketch, "E8.27.0.0", {"start": v(52, 43.15) * mm, "end": v(52, 41.15) * mm});
            skLineSegment(sketch, "E8.27.0.1", {"start": v(50, 43.15) * mm, "end": v(50, 41.15) * mm});
            skLineSegment(sketch, "E8.27.0.2", {"start": v(50, 41.15) * mm, "end": v(52, 41.15) * mm});
            skLineSegment(sketch, "E8.27.0.3", {"start": v(50, 43.15) * mm, "end": v(52, 43.15) * mm});
            skLineSegment(sketch, "E8.27.1.0", {"start": v(52, 39.15) * mm, "end": v(52, 37.15) * mm});
            skLineSegment(sketch, "E8.27.1.1", {"start": v(50, 39.15) * mm, "end": v(50, 37.15) * mm});
            skLineSegment(sketch, "E8.27.1.2", {"start": v(50, 37.15) * mm, "end": v(52, 37.15) * mm});
            skLineSegment(sketch, "E8.27.1.3", {"start": v(50, 39.15) * mm, "end": v(52, 39.15) * mm});
            skLineSegment(sketch, "E8.27.2.0", {"start": v(52, 35.15) * mm, "end": v(52, 33.15) * mm});
            skLineSegment(sketch, "E8.27.2.1", {"start": v(50, 35.15) * mm, "end": v(50, 33.15) * mm});
            skLineSegment(sketch, "E8.27.2.2", {"start": v(50, 33.15) * mm, "end": v(52, 33.15) * mm});
            skLineSegment(sketch, "E8.27.2.3", {"start": v(50, 35.15) * mm, "end": v(52, 35.15) * mm});
            skLineSegment(sketch, "E8.27.3.0", {"start": v(52, 31.15) * mm, "end": v(52, 29.15) * mm});
            skLineSegment(sketch, "E8.27.3.1", {"start": v(50, 31.15) * mm, "end": v(50, 29.15) * mm});
            skLineSegment(sketch, "E8.27.3.2", {"start": v(50, 29.15) * mm, "end": v(52, 29.15) * mm});
            skLineSegment(sketch, "E8.27.3.3", {"start": v(50, 31.15) * mm, "end": v(52, 31.15) * mm});
            skLineSegment(sketch, "E8.27.4.0", {"start": v(52, 27.15) * mm, "end": v(52, 25.15) * mm});
            skLineSegment(sketch, "E8.27.4.1", {"start": v(50, 27.15) * mm, "end": v(50, 25.15) * mm});
            skLineSegment(sketch, "E8.27.4.2", {"start": v(50, 25.15) * mm, "end": v(52, 25.15) * mm});
            skLineSegment(sketch, "E8.27.4.3", {"start": v(50, 27.15) * mm, "end": v(52, 27.15) * mm});
            skLineSegment(sketch, "E8.27.5.0", {"start": v(52, 23.15) * mm, "end": v(52, 21.15) * mm});
            skLineSegment(sketch, "E8.27.5.1", {"start": v(50, 23.15) * mm, "end": v(50, 21.15) * mm});
            skLineSegment(sketch, "E8.27.5.2", {"start": v(50, 21.15) * mm, "end": v(52, 21.15) * mm});
            skLineSegment(sketch, "E8.27.5.3", {"start": v(50, 23.15) * mm, "end": v(52, 23.15) * mm});
            skLineSegment(sketch, "E8.27.6.0", {"start": v(52, 19.15) * mm, "end": v(52, 17.15) * mm});
            skLineSegment(sketch, "E8.27.6.1", {"start": v(50, 19.15) * mm, "end": v(50, 17.15) * mm});
            skLineSegment(sketch, "E8.27.6.2", {"start": v(50, 17.15) * mm, "end": v(52, 17.15) * mm});
            skLineSegment(sketch, "E8.27.6.3", {"start": v(50, 19.15) * mm, "end": v(52, 19.15) * mm});
            skLineSegment(sketch, "E8.27.7.0", {"start": v(52, 15.15) * mm, "end": v(52, 13.15) * mm});
            skLineSegment(sketch, "E8.27.7.1", {"start": v(50, 15.15) * mm, "end": v(50, 13.15) * mm});
            skLineSegment(sketch, "E8.27.7.2", {"start": v(50, 13.15) * mm, "end": v(52, 13.15) * mm});
            skLineSegment(sketch, "E8.27.7.3", {"start": v(50, 15.15) * mm, "end": v(52, 15.15) * mm});
            skLineSegment(sketch, "E8.27.8.0", {"start": v(52, 11.15) * mm, "end": v(52, 9.15) * mm});
            skLineSegment(sketch, "E8.27.8.1", {"start": v(50, 11.15) * mm, "end": v(50, 9.15) * mm});
            skLineSegment(sketch, "E8.27.8.2", {"start": v(50, 9.15) * mm, "end": v(52, 9.15) * mm});
            skLineSegment(sketch, "E8.27.8.3", {"start": v(50, 11.15) * mm, "end": v(52, 11.15) * mm});
            skLineSegment(sketch, "E8.27.9.0", {"start": v(52, 7.15) * mm, "end": v(52, 5.15) * mm});
            skLineSegment(sketch, "E8.27.9.1", {"start": v(50, 7.15) * mm, "end": v(50, 5.15) * mm});
            skLineSegment(sketch, "E8.27.9.2", {"start": v(50, 5.15) * mm, "end": v(52, 5.15) * mm});
            skLineSegment(sketch, "E8.27.9.3", {"start": v(50, 7.15) * mm, "end": v(52, 7.15) * mm});
            skLineSegment(sketch, "E8.27.10.0", {"start": v(52, 3.15) * mm, "end": v(52, 1.15) * mm});
            skLineSegment(sketch, "E8.27.10.1", {"start": v(50, 3.15) * mm, "end": v(50, 1.15) * mm});
            skLineSegment(sketch, "E8.27.10.2", {"start": v(50, 1.15) * mm, "end": v(52, 1.15) * mm});
            skLineSegment(sketch, "E8.27.10.3", {"start": v(50, 3.15) * mm, "end": v(52, 3.15) * mm});
            skLineSegment(sketch, "E8.27.11.0", {"start": v(52, -0.85) * mm, "end": v(52, -2.85) * mm});
            skLineSegment(sketch, "E8.27.11.1", {"start": v(50, -0.85) * mm, "end": v(50, -2.85) * mm});
            skLineSegment(sketch, "E8.27.11.2", {"start": v(50, -2.85) * mm, "end": v(52, -2.85) * mm});
            skLineSegment(sketch, "E8.27.11.3", {"start": v(50, -0.85) * mm, "end": v(52, -0.85) * mm});
            skLineSegment(sketch, "E8.27.12.0", {"start": v(52, -4.85) * mm, "end": v(52, -6.85) * mm});
            skLineSegment(sketch, "E8.27.12.1", {"start": v(50, -4.85) * mm, "end": v(50, -6.85) * mm});
            skLineSegment(sketch, "E8.27.12.2", {"start": v(50, -6.85) * mm, "end": v(52, -6.85) * mm});
            skLineSegment(sketch, "E8.27.12.3", {"start": v(50, -4.85) * mm, "end": v(52, -4.85) * mm});
            skLineSegment(sketch, "E8.27.13.0", {"start": v(52, -8.85) * mm, "end": v(52, -10.85) * mm});
            skLineSegment(sketch, "E8.27.13.1", {"start": v(50, -8.85) * mm, "end": v(50, -10.85) * mm});
            skLineSegment(sketch, "E8.27.13.2", {"start": v(50, -10.85) * mm, "end": v(52, -10.85) * mm});
            skLineSegment(sketch, "E8.27.13.3", {"start": v(50, -8.85) * mm, "end": v(52, -8.85) * mm});
            skLineSegment(sketch, "E8.27.14.0", {"start": v(52, -12.85) * mm, "end": v(52, -14.85) * mm});
            skLineSegment(sketch, "E8.27.14.1", {"start": v(50, -12.85) * mm, "end": v(50, -14.85) * mm});
            skLineSegment(sketch, "E8.27.14.2", {"start": v(50, -14.85) * mm, "end": v(52, -14.85) * mm});
            skLineSegment(sketch, "E8.27.14.3", {"start": v(50, -12.85) * mm, "end": v(52, -12.85) * mm});
            skLineSegment(sketch, "E8.27.15.0", {"start": v(52, -16.85) * mm, "end": v(52, -18.85) * mm});
            skLineSegment(sketch, "E8.27.15.1", {"start": v(50, -16.85) * mm, "end": v(50, -18.85) * mm});
            skLineSegment(sketch, "E8.27.15.2", {"start": v(50, -18.85) * mm, "end": v(52, -18.85) * mm});
            skLineSegment(sketch, "E8.27.15.3", {"start": v(50, -16.85) * mm, "end": v(52, -16.85) * mm});
            skLineSegment(sketch, "E8.27.16.0", {"start": v(52, -20.85) * mm, "end": v(52, -22.85) * mm});
            skLineSegment(sketch, "E8.27.16.1", {"start": v(50, -20.85) * mm, "end": v(50, -22.85) * mm});
            skLineSegment(sketch, "E8.27.16.2", {"start": v(50, -22.85) * mm, "end": v(52, -22.85) * mm});
            skLineSegment(sketch, "E8.27.16.3", {"start": v(50, -20.85) * mm, "end": v(52, -20.85) * mm});
            skLineSegment(sketch, "E8.27.17.0", {"start": v(52, -24.85) * mm, "end": v(52, -26.85) * mm});
            skLineSegment(sketch, "E8.27.17.1", {"start": v(50, -24.85) * mm, "end": v(50, -26.85) * mm});
            skLineSegment(sketch, "E8.27.17.2", {"start": v(50, -26.85) * mm, "end": v(52, -26.85) * mm});
            skLineSegment(sketch, "E8.27.17.3", {"start": v(50, -24.85) * mm, "end": v(52, -24.85) * mm});
            skLineSegment(sketch, "E8.27.18.0", {"start": v(52, -28.85) * mm, "end": v(52, -30.85) * mm});
            skLineSegment(sketch, "E8.27.18.1", {"start": v(50, -28.85) * mm, "end": v(50, -30.85) * mm});
            skLineSegment(sketch, "E8.27.18.2", {"start": v(50, -30.85) * mm, "end": v(52, -30.85) * mm});
            skLineSegment(sketch, "E8.27.18.3", {"start": v(50, -28.85) * mm, "end": v(52, -28.85) * mm});
            skLineSegment(sketch, "E8.27.19.0", {"start": v(52, -32.85) * mm, "end": v(52, -34.85) * mm});
            skLineSegment(sketch, "E8.27.19.1", {"start": v(50, -32.85) * mm, "end": v(50, -34.85) * mm});
            skLineSegment(sketch, "E8.27.19.2", {"start": v(50, -34.85) * mm, "end": v(52, -34.85) * mm});
            skLineSegment(sketch, "E8.27.19.3", {"start": v(50, -32.85) * mm, "end": v(52, -32.85) * mm});
            skLineSegment(sketch, "E8.27.20.0", {"start": v(52, -36.85) * mm, "end": v(52, -38.85) * mm});
            skLineSegment(sketch, "E8.27.20.1", {"start": v(50, -36.85) * mm, "end": v(50, -38.85) * mm});
            skLineSegment(sketch, "E8.27.20.2", {"start": v(50, -38.85) * mm, "end": v(52, -38.85) * mm});
            skLineSegment(sketch, "E8.27.20.3", {"start": v(50, -36.85) * mm, "end": v(52, -36.85) * mm});
            skLineSegment(sketch, "E8.27.21.0", {"start": v(52, -40.85) * mm, "end": v(52, -42.85) * mm});
            skLineSegment(sketch, "E8.27.21.1", {"start": v(50, -40.85) * mm, "end": v(50, -42.85) * mm});
            skLineSegment(sketch, "E8.27.21.2", {"start": v(50, -42.85) * mm, "end": v(52, -42.85) * mm});
            skLineSegment(sketch, "E8.27.21.3", {"start": v(50, -40.85) * mm, "end": v(52, -40.85) * mm});
            skLineSegment(sketch, "E8.28.0.0", {"start": v(56, 43.15) * mm, "end": v(56, 41.15) * mm});
            skLineSegment(sketch, "E8.28.0.1", {"start": v(54, 43.15) * mm, "end": v(54, 41.15) * mm});
            skLineSegment(sketch, "E8.28.0.2", {"start": v(54, 41.15) * mm, "end": v(56, 41.15) * mm});
            skLineSegment(sketch, "E8.28.0.3", {"start": v(54, 43.15) * mm, "end": v(56, 43.15) * mm});
            skLineSegment(sketch, "E8.28.1.0", {"start": v(56, 39.15) * mm, "end": v(56, 37.15) * mm});
            skLineSegment(sketch, "E8.28.1.1", {"start": v(54, 39.15) * mm, "end": v(54, 37.15) * mm});
            skLineSegment(sketch, "E8.28.1.2", {"start": v(54, 37.15) * mm, "end": v(56, 37.15) * mm});
            skLineSegment(sketch, "E8.28.1.3", {"start": v(54, 39.15) * mm, "end": v(56, 39.15) * mm});
            skLineSegment(sketch, "E8.28.2.0", {"start": v(56, 35.15) * mm, "end": v(56, 33.15) * mm});
            skLineSegment(sketch, "E8.28.2.1", {"start": v(54, 35.15) * mm, "end": v(54, 33.15) * mm});
            skLineSegment(sketch, "E8.28.2.2", {"start": v(54, 33.15) * mm, "end": v(56, 33.15) * mm});
            skLineSegment(sketch, "E8.28.2.3", {"start": v(54, 35.15) * mm, "end": v(56, 35.15) * mm});
            skLineSegment(sketch, "E8.28.3.0", {"start": v(56, 31.15) * mm, "end": v(56, 29.15) * mm});
            skLineSegment(sketch, "E8.28.3.1", {"start": v(54, 31.15) * mm, "end": v(54, 29.15) * mm});
            skLineSegment(sketch, "E8.28.3.2", {"start": v(54, 29.15) * mm, "end": v(56, 29.15) * mm});
            skLineSegment(sketch, "E8.28.3.3", {"start": v(54, 31.15) * mm, "end": v(56, 31.15) * mm});
            skLineSegment(sketch, "E8.28.4.0", {"start": v(56, 27.15) * mm, "end": v(56, 25.15) * mm});
            skLineSegment(sketch, "E8.28.4.1", {"start": v(54, 27.15) * mm, "end": v(54, 25.15) * mm});
            skLineSegment(sketch, "E8.28.4.2", {"start": v(54, 25.15) * mm, "end": v(56, 25.15) * mm});
            skLineSegment(sketch, "E8.28.4.3", {"start": v(54, 27.15) * mm, "end": v(56, 27.15) * mm});
            skLineSegment(sketch, "E8.28.5.0", {"start": v(56, 23.15) * mm, "end": v(56, 21.15) * mm});
            skLineSegment(sketch, "E8.28.5.1", {"start": v(54, 23.15) * mm, "end": v(54, 21.15) * mm});
            skLineSegment(sketch, "E8.28.5.2", {"start": v(54, 21.15) * mm, "end": v(56, 21.15) * mm});
            skLineSegment(sketch, "E8.28.5.3", {"start": v(54, 23.15) * mm, "end": v(56, 23.15) * mm});
            skLineSegment(sketch, "E8.28.6.0", {"start": v(56, 19.15) * mm, "end": v(56, 17.15) * mm});
            skLineSegment(sketch, "E8.28.6.1", {"start": v(54, 19.15) * mm, "end": v(54, 17.15) * mm});
            skLineSegment(sketch, "E8.28.6.2", {"start": v(54, 17.15) * mm, "end": v(56, 17.15) * mm});
            skLineSegment(sketch, "E8.28.6.3", {"start": v(54, 19.15) * mm, "end": v(56, 19.15) * mm});
            skLineSegment(sketch, "E8.28.7.0", {"start": v(56, 15.15) * mm, "end": v(56, 13.15) * mm});
            skLineSegment(sketch, "E8.28.7.1", {"start": v(54, 15.15) * mm, "end": v(54, 13.15) * mm});
            skLineSegment(sketch, "E8.28.7.2", {"start": v(54, 13.15) * mm, "end": v(56, 13.15) * mm});
            skLineSegment(sketch, "E8.28.7.3", {"start": v(54, 15.15) * mm, "end": v(56, 15.15) * mm});
            skLineSegment(sketch, "E8.28.8.0", {"start": v(56, 11.15) * mm, "end": v(56, 9.15) * mm});
            skLineSegment(sketch, "E8.28.8.1", {"start": v(54, 11.15) * mm, "end": v(54, 9.15) * mm});
            skLineSegment(sketch, "E8.28.8.2", {"start": v(54, 9.15) * mm, "end": v(56, 9.15) * mm});
            skLineSegment(sketch, "E8.28.8.3", {"start": v(54, 11.15) * mm, "end": v(56, 11.15) * mm});
            skLineSegment(sketch, "E8.28.9.0", {"start": v(56, 7.15) * mm, "end": v(56, 5.15) * mm});
            skLineSegment(sketch, "E8.28.9.1", {"start": v(54, 7.15) * mm, "end": v(54, 5.15) * mm});
            skLineSegment(sketch, "E8.28.9.2", {"start": v(54, 5.15) * mm, "end": v(56, 5.15) * mm});
            skLineSegment(sketch, "E8.28.9.3", {"start": v(54, 7.15) * mm, "end": v(56, 7.15) * mm});
            skLineSegment(sketch, "E8.28.10.0", {"start": v(56, 3.15) * mm, "end": v(56, 1.15) * mm});
            skLineSegment(sketch, "E8.28.10.1", {"start": v(54, 3.15) * mm, "end": v(54, 1.15) * mm});
            skLineSegment(sketch, "E8.28.10.2", {"start": v(54, 1.15) * mm, "end": v(56, 1.15) * mm});
            skLineSegment(sketch, "E8.28.10.3", {"start": v(54, 3.15) * mm, "end": v(56, 3.15) * mm});
            skLineSegment(sketch, "E8.28.11.0", {"start": v(56, -0.85) * mm, "end": v(56, -2.85) * mm});
            skLineSegment(sketch, "E8.28.11.1", {"start": v(54, -0.85) * mm, "end": v(54, -2.85) * mm});
            skLineSegment(sketch, "E8.28.11.2", {"start": v(54, -2.85) * mm, "end": v(56, -2.85) * mm});
            skLineSegment(sketch, "E8.28.11.3", {"start": v(54, -0.85) * mm, "end": v(56, -0.85) * mm});
            skLineSegment(sketch, "E8.28.12.0", {"start": v(56, -4.85) * mm, "end": v(56, -6.85) * mm});
            skLineSegment(sketch, "E8.28.12.1", {"start": v(54, -4.85) * mm, "end": v(54, -6.85) * mm});
            skLineSegment(sketch, "E8.28.12.2", {"start": v(54, -6.85) * mm, "end": v(56, -6.85) * mm});
            skLineSegment(sketch, "E8.28.12.3", {"start": v(54, -4.85) * mm, "end": v(56, -4.85) * mm});
            skLineSegment(sketch, "E8.28.13.0", {"start": v(56, -8.85) * mm, "end": v(56, -10.85) * mm});
            skLineSegment(sketch, "E8.28.13.1", {"start": v(54, -8.85) * mm, "end": v(54, -10.85) * mm});
            skLineSegment(sketch, "E8.28.13.2", {"start": v(54, -10.85) * mm, "end": v(56, -10.85) * mm});
            skLineSegment(sketch, "E8.28.13.3", {"start": v(54, -8.85) * mm, "end": v(56, -8.85) * mm});
            skLineSegment(sketch, "E8.28.14.0", {"start": v(56, -12.85) * mm, "end": v(56, -14.85) * mm});
            skLineSegment(sketch, "E8.28.14.1", {"start": v(54, -12.85) * mm, "end": v(54, -14.85) * mm});
            skLineSegment(sketch, "E8.28.14.2", {"start": v(54, -14.85) * mm, "end": v(56, -14.85) * mm});
            skLineSegment(sketch, "E8.28.14.3", {"start": v(54, -12.85) * mm, "end": v(56, -12.85) * mm});
            skLineSegment(sketch, "E8.28.15.0", {"start": v(56, -16.85) * mm, "end": v(56, -18.85) * mm});
            skLineSegment(sketch, "E8.28.15.1", {"start": v(54, -16.85) * mm, "end": v(54, -18.85) * mm});
            skLineSegment(sketch, "E8.28.15.2", {"start": v(54, -18.85) * mm, "end": v(56, -18.85) * mm});
            skLineSegment(sketch, "E8.28.15.3", {"start": v(54, -16.85) * mm, "end": v(56, -16.85) * mm});
            skLineSegment(sketch, "E8.28.16.0", {"start": v(56, -20.85) * mm, "end": v(56, -22.85) * mm});
            skLineSegment(sketch, "E8.28.16.1", {"start": v(54, -20.85) * mm, "end": v(54, -22.85) * mm});
            skLineSegment(sketch, "E8.28.16.2", {"start": v(54, -22.85) * mm, "end": v(56, -22.85) * mm});
            skLineSegment(sketch, "E8.28.16.3", {"start": v(54, -20.85) * mm, "end": v(56, -20.85) * mm});
            skLineSegment(sketch, "E8.28.17.0", {"start": v(56, -24.85) * mm, "end": v(56, -26.85) * mm});
            skLineSegment(sketch, "E8.28.17.1", {"start": v(54, -24.85) * mm, "end": v(54, -26.85) * mm});
            skLineSegment(sketch, "E8.28.17.2", {"start": v(54, -26.85) * mm, "end": v(56, -26.85) * mm});
            skLineSegment(sketch, "E8.28.17.3", {"start": v(54, -24.85) * mm, "end": v(56, -24.85) * mm});
            skLineSegment(sketch, "E8.28.18.0", {"start": v(56, -28.85) * mm, "end": v(56, -30.85) * mm});
            skLineSegment(sketch, "E8.28.18.1", {"start": v(54, -28.85) * mm, "end": v(54, -30.85) * mm});
            skLineSegment(sketch, "E8.28.18.2", {"start": v(54, -30.85) * mm, "end": v(56, -30.85) * mm});
            skLineSegment(sketch, "E8.28.18.3", {"start": v(54, -28.85) * mm, "end": v(56, -28.85) * mm});
            skLineSegment(sketch, "E8.28.19.0", {"start": v(56, -32.85) * mm, "end": v(56, -34.85) * mm});
            skLineSegment(sketch, "E8.28.19.1", {"start": v(54, -32.85) * mm, "end": v(54, -34.85) * mm});
            skLineSegment(sketch, "E8.28.19.2", {"start": v(54, -34.85) * mm, "end": v(56, -34.85) * mm});
            skLineSegment(sketch, "E8.28.19.3", {"start": v(54, -32.85) * mm, "end": v(56, -32.85) * mm});
            skLineSegment(sketch, "E8.28.20.0", {"start": v(56, -36.85) * mm, "end": v(56, -38.85) * mm});
            skLineSegment(sketch, "E8.28.20.1", {"start": v(54, -36.85) * mm, "end": v(54, -38.85) * mm});
            skLineSegment(sketch, "E8.28.20.2", {"start": v(54, -38.85) * mm, "end": v(56, -38.85) * mm});
            skLineSegment(sketch, "E8.28.20.3", {"start": v(54, -36.85) * mm, "end": v(56, -36.85) * mm});
            skLineSegment(sketch, "E8.28.21.0", {"start": v(56, -40.85) * mm, "end": v(56, -42.85) * mm});
            skLineSegment(sketch, "E8.28.21.1", {"start": v(54, -40.85) * mm, "end": v(54, -42.85) * mm});
            skLineSegment(sketch, "E8.28.21.2", {"start": v(54, -42.85) * mm, "end": v(56, -42.85) * mm});
            skLineSegment(sketch, "E8.28.21.3", {"start": v(54, -40.85) * mm, "end": v(56, -40.85) * mm});
            skLineSegment(sketch, "E8.direction1", {"start": v(-56, 41.15) * mm, "end": v(-52, 41.15) * mm, "construction": true});
            skLineSegment(sketch, "E8.direction2", {"start": v(-56, 41.15) * mm, "end": v(-56, 37.15) * mm, "construction": true});
            skSolve(sketch);
        }
        {
            var Q0;
            Q0 = qSketchRegion(id + "F3", true);
            extrude(context, id + "F4", {"entities" : qUnion([Q0]), "operationType" : NewBodyOperationType.REMOVE, "oppositeDirection" : true, "depth" : 25 * mm});
        }
    });
